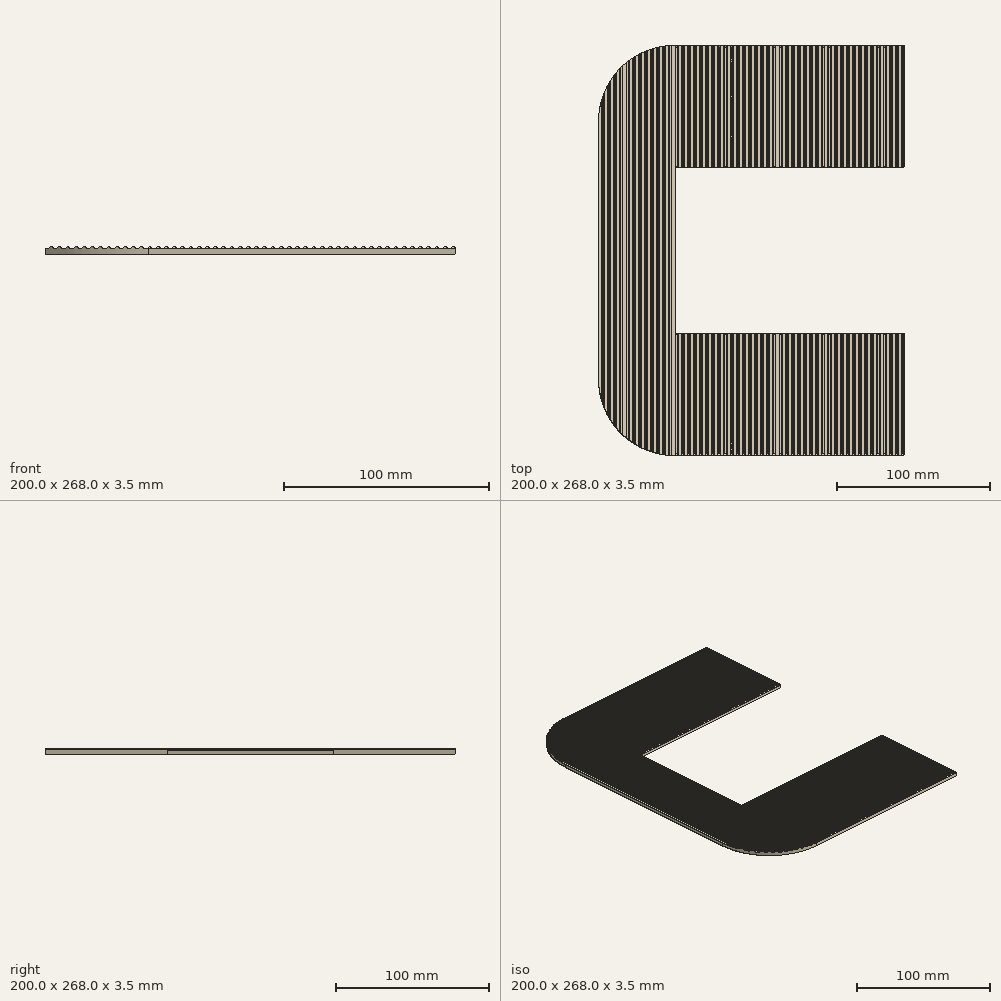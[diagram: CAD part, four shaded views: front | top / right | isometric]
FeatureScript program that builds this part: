
annotation { "Feature Type Name" : "Feature", "Feature Type Description" : "" }
export const myFeature = defineFeature(function(context is Context, id is Id, definition is map)
    precondition{}
    {
        {
            var Q0;
            Q0=qCreatedBy(makeId("Top.planeOp"),FACE);
            var sketch = newSketch(context, id + "F0", { "sketchPlane" : qUnion([Q0])});
            skLineSegment(sketch, "E0.bottom", {"start": v(-200, 134) * mm, "end": v(0, 134) * mm});
            skLineSegment(sketch, "E0.top", {"start": v(-200, -134) * mm, "end": v(0, -134) * mm});
            skLineSegment(sketch, "E0.left", {"start": v(-200, 134) * mm, "end": v(-200, -134) * mm});
            skLineSegment(sketch, "E0.right", {"start": v(0, 134) * mm, "end": v(0, -134) * mm});
            skPoint(sketch, "E1", {"position": v(0, 0) * mm});
            skLineSegment(sketch, "E2.bottom", {"start": v(-150, 54) * mm, "end": v(0, 54) * mm});
            skLineSegment(sketch, "E2.top", {"start": v(-150, -54) * mm, "end": v(0, -54) * mm});
            skLineSegment(sketch, "E2.left", {"start": v(-150, 54) * mm, "end": v(-150, -54) * mm});
            skLineSegment(sketch, "E2.right", {"start": v(0, 54) * mm, "end": v(0, -54) * mm});
            skSolve(sketch);
        }
        {
            var Q0;
            {var subQ1=sQuery(id+"F0.wireOp",EDGE,"E0.bottom");Q0=makeQuery(id+"F0.imprint","IMPRINT",FACE,{"disambiguationData":[TD([[makeQuery(id+"F0.imprint","IMPRINT",EDGE,{"derivedFrom":subQ1}),-1.0]])]});}
            extrude(context, id + "F1", {"entities" : qUnion([Q0]), "depth" : 2.5 * mm});
        }
        {
            var Q0;
            Q0=makeQuery(id+"F1.opExtrude","SWEPT_EDGE",EDGE,{"disambiguationData":[OSD([sQuery(id+"F0.wireOp",EDGE,"E0.top"),sQuery(id+"F0.wireOp",EDGE,"E0.left")])]});
            var Q1;
            Q1=makeQuery(id+"F1.opExtrude","SWEPT_EDGE",EDGE,{"disambiguationData":[OSD([sQuery(id+"F0.wireOp",EDGE,"E0.bottom"),sQuery(id+"F0.wireOp",EDGE,"E0.left")])]});
            fillet(context, id + "F2", {"entities" : qUnion([Q0, Q1]), "radius" : 50 * mm, "tangentPropagation" : true, "allowEdgeOverflow" : false});
        }
        {
            var Q0;
            Q0=makeQuery(id+"F1.opExtrude","CAP_FACE",FACE,{"disambiguationData":[OSD([sQuery(id+"F0.wireOp",EDGE,"E0.bottom"),sQuery(id+"F0.wireOp",EDGE,"E0.top"),sQuery(id+"F0.wireOp",EDGE,"E0.left"),sQuery(id+"F0.wireOp",EDGE,"E0.right"),sQuery(id+"F0.wireOp",EDGE,"E2.bottom"),sQuery(id+"F0.wireOp",EDGE,"E2.top"),sQuery(id+"F0.wireOp",EDGE,"E2.left")])],"isStart":false});
            var sketch = newSketch(context, id + "F3", { "sketchPlane" : qUnion([Q0])});
            skLineSegment(sketch, "E3.bottom", {"start": v(0, 134) * mm, "end": v(-2, 134) * mm});
            skLineSegment(sketch, "E3.top", {"start": v(0, -134) * mm, "end": v(-2, -134) * mm});
            skLineSegment(sketch, "E3.left", {"start": v(0, 134) * mm, "end": v(0, -134) * mm});
            skLineSegment(sketch, "E3.right", {"start": v(-2, 134) * mm, "end": v(-2, -134) * mm});
            skLineSegment(sketch, "E4.1.0.0", {"start": v(-4, 134) * mm, "end": v(-4, -134) * mm});
            skLineSegment(sketch, "E4.1.0.1", {"start": v(-6, 134) * mm, "end": v(-6, -134) * mm});
            skLineSegment(sketch, "E4.1.0.2", {"start": v(-4, 134) * mm, "end": v(-6, 134) * mm});
            skLineSegment(sketch, "E4.1.0.3", {"start": v(-4, -134) * mm, "end": v(-6, -134) * mm});
            skLineSegment(sketch, "E4.2.0.0", {"start": v(-8, 134) * mm, "end": v(-8, -134) * mm});
            skLineSegment(sketch, "E4.2.0.1", {"start": v(-10, 134) * mm, "end": v(-10, -134) * mm});
            skLineSegment(sketch, "E4.2.0.2", {"start": v(-8, 134) * mm, "end": v(-10, 134) * mm});
            skLineSegment(sketch, "E4.2.0.3", {"start": v(-8, -134) * mm, "end": v(-10, -134) * mm});
            skLineSegment(sketch, "E4.3.0.0", {"start": v(-12, 134) * mm, "end": v(-12, -134) * mm});
            skLineSegment(sketch, "E4.3.0.1", {"start": v(-14, 134) * mm, "end": v(-14, -134) * mm});
            skLineSegment(sketch, "E4.3.0.2", {"start": v(-12, 134) * mm, "end": v(-14, 134) * mm});
            skLineSegment(sketch, "E4.3.0.3", {"start": v(-12, -134) * mm, "end": v(-14, -134) * mm});
            skLineSegment(sketch, "E4.4.0.0", {"start": v(-16, 134) * mm, "end": v(-16, -134) * mm});
            skLineSegment(sketch, "E4.4.0.1", {"start": v(-18, 134) * mm, "end": v(-18, -134) * mm});
            skLineSegment(sketch, "E4.4.0.2", {"start": v(-16, 134) * mm, "end": v(-18, 134) * mm});
            skLineSegment(sketch, "E4.4.0.3", {"start": v(-16, -134) * mm, "end": v(-18, -134) * mm});
            skLineSegment(sketch, "E4.5.0.0", {"start": v(-20, 134) * mm, "end": v(-20, -134) * mm});
            skLineSegment(sketch, "E4.5.0.1", {"start": v(-22, 134) * mm, "end": v(-22, -134) * mm});
            skLineSegment(sketch, "E4.5.0.2", {"start": v(-20, 134) * mm, "end": v(-22, 134) * mm});
            skLineSegment(sketch, "E4.5.0.3", {"start": v(-20, -134) * mm, "end": v(-22, -134) * mm});
            skLineSegment(sketch, "E4.6.0.0", {"start": v(-24, 134) * mm, "end": v(-24, -134) * mm});
            skLineSegment(sketch, "E4.6.0.1", {"start": v(-26, 134) * mm, "end": v(-26, -134) * mm});
            skLineSegment(sketch, "E4.6.0.2", {"start": v(-24, 134) * mm, "end": v(-26, 134) * mm});
            skLineSegment(sketch, "E4.6.0.3", {"start": v(-24, -134) * mm, "end": v(-26, -134) * mm});
            skLineSegment(sketch, "E4.7.0.0", {"start": v(-28, 134) * mm, "end": v(-28, -134) * mm});
            skLineSegment(sketch, "E4.7.0.1", {"start": v(-30, 134) * mm, "end": v(-30, -134) * mm});
            skLineSegment(sketch, "E4.7.0.2", {"start": v(-28, 134) * mm, "end": v(-30, 134) * mm});
            skLineSegment(sketch, "E4.7.0.3", {"start": v(-28, -134) * mm, "end": v(-30, -134) * mm});
            skLineSegment(sketch, "E4.8.0.0", {"start": v(-32, 134) * mm, "end": v(-32, -134) * mm});
            skLineSegment(sketch, "E4.8.0.1", {"start": v(-34, 134) * mm, "end": v(-34, -134) * mm});
            skLineSegment(sketch, "E4.8.0.2", {"start": v(-32, 134) * mm, "end": v(-34, 134) * mm});
            skLineSegment(sketch, "E4.8.0.3", {"start": v(-32, -134) * mm, "end": v(-34, -134) * mm});
            skLineSegment(sketch, "E4.9.0.0", {"start": v(-36, 134) * mm, "end": v(-36, -134) * mm});
            skLineSegment(sketch, "E4.9.0.1", {"start": v(-38, 134) * mm, "end": v(-38, -134) * mm});
            skLineSegment(sketch, "E4.9.0.2", {"start": v(-36, 134) * mm, "end": v(-38, 134) * mm});
            skLineSegment(sketch, "E4.9.0.3", {"start": v(-36, -134) * mm, "end": v(-38, -134) * mm});
            skLineSegment(sketch, "E4.10.0.0", {"start": v(-40, 134) * mm, "end": v(-40, -134) * mm});
            skLineSegment(sketch, "E4.10.0.1", {"start": v(-42, 134) * mm, "end": v(-42, -134) * mm});
            skLineSegment(sketch, "E4.10.0.2", {"start": v(-40, 134) * mm, "end": v(-42, 134) * mm});
            skLineSegment(sketch, "E4.10.0.3", {"start": v(-40, -134) * mm, "end": v(-42, -134) * mm});
            skLineSegment(sketch, "E4.11.0.0", {"start": v(-44, 134) * mm, "end": v(-44, -134) * mm});
            skLineSegment(sketch, "E4.11.0.1", {"start": v(-46, 134) * mm, "end": v(-46, -134) * mm});
            skLineSegment(sketch, "E4.11.0.2", {"start": v(-44, 134) * mm, "end": v(-46, 134) * mm});
            skLineSegment(sketch, "E4.11.0.3", {"start": v(-44, -134) * mm, "end": v(-46, -134) * mm});
            skLineSegment(sketch, "E4.12.0.0", {"start": v(-48, 134) * mm, "end": v(-48, -134) * mm});
            skLineSegment(sketch, "E4.12.0.1", {"start": v(-50, 134) * mm, "end": v(-50, -134) * mm});
            skLineSegment(sketch, "E4.12.0.2", {"start": v(-48, 134) * mm, "end": v(-50, 134) * mm});
            skLineSegment(sketch, "E4.12.0.3", {"start": v(-48, -134) * mm, "end": v(-50, -134) * mm});
            skLineSegment(sketch, "E4.13.0.0", {"start": v(-52, 134) * mm, "end": v(-52, -134) * mm});
            skLineSegment(sketch, "E4.13.0.1", {"start": v(-54, 134) * mm, "end": v(-54, -134) * mm});
            skLineSegment(sketch, "E4.13.0.2", {"start": v(-52, 134) * mm, "end": v(-54, 134) * mm});
            skLineSegment(sketch, "E4.13.0.3", {"start": v(-52, -134) * mm, "end": v(-54, -134) * mm});
            skLineSegment(sketch, "E4.14.0.0", {"start": v(-56, 134) * mm, "end": v(-56, -134) * mm});
            skLineSegment(sketch, "E4.14.0.1", {"start": v(-58, 134) * mm, "end": v(-58, -134) * mm});
            skLineSegment(sketch, "E4.14.0.2", {"start": v(-56, 134) * mm, "end": v(-58, 134) * mm});
            skLineSegment(sketch, "E4.14.0.3", {"start": v(-56, -134) * mm, "end": v(-58, -134) * mm});
            skLineSegment(sketch, "E4.15.0.0", {"start": v(-60, 134) * mm, "end": v(-60, -134) * mm});
            skLineSegment(sketch, "E4.15.0.1", {"start": v(-62, 134) * mm, "end": v(-62, -134) * mm});
            skLineSegment(sketch, "E4.15.0.2", {"start": v(-60, 134) * mm, "end": v(-62, 134) * mm});
            skLineSegment(sketch, "E4.15.0.3", {"start": v(-60, -134) * mm, "end": v(-62, -134) * mm});
            skLineSegment(sketch, "E4.16.0.0", {"start": v(-64, 134) * mm, "end": v(-64, -134) * mm});
            skLineSegment(sketch, "E4.16.0.1", {"start": v(-66, 134) * mm, "end": v(-66, -134) * mm});
            skLineSegment(sketch, "E4.16.0.2", {"start": v(-64, 134) * mm, "end": v(-66, 134) * mm});
            skLineSegment(sketch, "E4.16.0.3", {"start": v(-64, -134) * mm, "end": v(-66, -134) * mm});
            skLineSegment(sketch, "E4.17.0.0", {"start": v(-68, 134) * mm, "end": v(-68, -134) * mm});
            skLineSegment(sketch, "E4.17.0.1", {"start": v(-70, 134) * mm, "end": v(-70, -134) * mm});
            skLineSegment(sketch, "E4.17.0.2", {"start": v(-68, 134) * mm, "end": v(-70, 134) * mm});
            skLineSegment(sketch, "E4.17.0.3", {"start": v(-68, -134) * mm, "end": v(-70, -134) * mm});
            skLineSegment(sketch, "E4.18.0.0", {"start": v(-72, 134) * mm, "end": v(-72, -134) * mm});
            skLineSegment(sketch, "E4.18.0.1", {"start": v(-74, 134) * mm, "end": v(-74, -134) * mm});
            skLineSegment(sketch, "E4.18.0.2", {"start": v(-72, 134) * mm, "end": v(-74, 134) * mm});
            skLineSegment(sketch, "E4.18.0.3", {"start": v(-72, -134) * mm, "end": v(-74, -134) * mm});
            skLineSegment(sketch, "E4.19.0.0", {"start": v(-76, 134) * mm, "end": v(-76, -134) * mm});
            skLineSegment(sketch, "E4.19.0.1", {"start": v(-78, 134) * mm, "end": v(-78, -134) * mm});
            skLineSegment(sketch, "E4.19.0.2", {"start": v(-76, 134) * mm, "end": v(-78, 134) * mm});
            skLineSegment(sketch, "E4.19.0.3", {"start": v(-76, -134) * mm, "end": v(-78, -134) * mm});
            skLineSegment(sketch, "E4.20.0.0", {"start": v(-80, 134) * mm, "end": v(-80, -134) * mm});
            skLineSegment(sketch, "E4.20.0.1", {"start": v(-82, 134) * mm, "end": v(-82, -134) * mm});
            skLineSegment(sketch, "E4.20.0.2", {"start": v(-80, 134) * mm, "end": v(-82, 134) * mm});
            skLineSegment(sketch, "E4.20.0.3", {"start": v(-80, -134) * mm, "end": v(-82, -134) * mm});
            skLineSegment(sketch, "E4.21.0.0", {"start": v(-84, 134) * mm, "end": v(-84, -134) * mm});
            skLineSegment(sketch, "E4.21.0.1", {"start": v(-86, 134) * mm, "end": v(-86, -134) * mm});
            skLineSegment(sketch, "E4.21.0.2", {"start": v(-84, 134) * mm, "end": v(-86, 134) * mm});
            skLineSegment(sketch, "E4.21.0.3", {"start": v(-84, -134) * mm, "end": v(-86, -134) * mm});
            skLineSegment(sketch, "E4.22.0.0", {"start": v(-88, 134) * mm, "end": v(-88, -134) * mm});
            skLineSegment(sketch, "E4.22.0.1", {"start": v(-90, 134) * mm, "end": v(-90, -134) * mm});
            skLineSegment(sketch, "E4.22.0.2", {"start": v(-88, 134) * mm, "end": v(-90, 134) * mm});
            skLineSegment(sketch, "E4.22.0.3", {"start": v(-88, -134) * mm, "end": v(-90, -134) * mm});
            skLineSegment(sketch, "E4.23.0.0", {"start": v(-92, 134) * mm, "end": v(-92, -134) * mm});
            skLineSegment(sketch, "E4.23.0.1", {"start": v(-94, 134) * mm, "end": v(-94, -134) * mm});
            skLineSegment(sketch, "E4.23.0.2", {"start": v(-92, 134) * mm, "end": v(-94, 134) * mm});
            skLineSegment(sketch, "E4.23.0.3", {"start": v(-92, -134) * mm, "end": v(-94, -134) * mm});
            skLineSegment(sketch, "E4.24.0.0", {"start": v(-96, 134) * mm, "end": v(-96, -134) * mm});
            skLineSegment(sketch, "E4.24.0.1", {"start": v(-98, 134) * mm, "end": v(-98, -134) * mm});
            skLineSegment(sketch, "E4.24.0.2", {"start": v(-96, 134) * mm, "end": v(-98, 134) * mm});
            skLineSegment(sketch, "E4.24.0.3", {"start": v(-96, -134) * mm, "end": v(-98, -134) * mm});
            skLineSegment(sketch, "E4.25.0.0", {"start": v(-100, 134) * mm, "end": v(-100, -134) * mm});
            skLineSegment(sketch, "E4.25.0.1", {"start": v(-102, 134) * mm, "end": v(-102, -134) * mm});
            skLineSegment(sketch, "E4.25.0.2", {"start": v(-100, 134) * mm, "end": v(-102, 134) * mm});
            skLineSegment(sketch, "E4.25.0.3", {"start": v(-100, -134) * mm, "end": v(-102, -134) * mm});
            skLineSegment(sketch, "E4.26.0.0", {"start": v(-104, 134) * mm, "end": v(-104, -134) * mm});
            skLineSegment(sketch, "E4.26.0.1", {"start": v(-106, 134) * mm, "end": v(-106, -134) * mm});
            skLineSegment(sketch, "E4.26.0.2", {"start": v(-104, 134) * mm, "end": v(-106, 134) * mm});
            skLineSegment(sketch, "E4.26.0.3", {"start": v(-104, -134) * mm, "end": v(-106, -134) * mm});
            skLineSegment(sketch, "E4.27.0.0", {"start": v(-108, 134) * mm, "end": v(-108, -134) * mm});
            skLineSegment(sketch, "E4.27.0.1", {"start": v(-110, 134) * mm, "end": v(-110, -134) * mm});
            skLineSegment(sketch, "E4.27.0.2", {"start": v(-108, 134) * mm, "end": v(-110, 134) * mm});
            skLineSegment(sketch, "E4.27.0.3", {"start": v(-108, -134) * mm, "end": v(-110, -134) * mm});
            skLineSegment(sketch, "E4.28.0.0", {"start": v(-112, 134) * mm, "end": v(-112, -134) * mm});
            skLineSegment(sketch, "E4.28.0.1", {"start": v(-114, 134) * mm, "end": v(-114, -134) * mm});
            skLineSegment(sketch, "E4.28.0.2", {"start": v(-112, 134) * mm, "end": v(-114, 134) * mm});
            skLineSegment(sketch, "E4.28.0.3", {"start": v(-112, -134) * mm, "end": v(-114, -134) * mm});
            skLineSegment(sketch, "E4.29.0.0", {"start": v(-116, 134) * mm, "end": v(-116, -134) * mm});
            skLineSegment(sketch, "E4.29.0.1", {"start": v(-118, 134) * mm, "end": v(-118, -134) * mm});
            skLineSegment(sketch, "E4.29.0.2", {"start": v(-116, 134) * mm, "end": v(-118, 134) * mm});
            skLineSegment(sketch, "E4.29.0.3", {"start": v(-116, -134) * mm, "end": v(-118, -134) * mm});
            skLineSegment(sketch, "E4.30.0.0", {"start": v(-120, 134) * mm, "end": v(-120, -134) * mm});
            skLineSegment(sketch, "E4.30.0.1", {"start": v(-122, 134) * mm, "end": v(-122, -134) * mm});
            skLineSegment(sketch, "E4.30.0.2", {"start": v(-120, 134) * mm, "end": v(-122, 134) * mm});
            skLineSegment(sketch, "E4.30.0.3", {"start": v(-120, -134) * mm, "end": v(-122, -134) * mm});
            skLineSegment(sketch, "E4.31.0.0", {"start": v(-124, 134) * mm, "end": v(-124, -134) * mm});
            skLineSegment(sketch, "E4.31.0.1", {"start": v(-126, 134) * mm, "end": v(-126, -134) * mm});
            skLineSegment(sketch, "E4.31.0.2", {"start": v(-124, 134) * mm, "end": v(-126, 134) * mm});
            skLineSegment(sketch, "E4.31.0.3", {"start": v(-124, -134) * mm, "end": v(-126, -134) * mm});
            skLineSegment(sketch, "E4.32.0.0", {"start": v(-128, 134) * mm, "end": v(-128, -134) * mm});
            skLineSegment(sketch, "E4.32.0.1", {"start": v(-130, 134) * mm, "end": v(-130, -134) * mm});
            skLineSegment(sketch, "E4.32.0.2", {"start": v(-128, 134) * mm, "end": v(-130, 134) * mm});
            skLineSegment(sketch, "E4.32.0.3", {"start": v(-128, -134) * mm, "end": v(-130, -134) * mm});
            skLineSegment(sketch, "E4.33.0.0", {"start": v(-132, 134) * mm, "end": v(-132, -134) * mm});
            skLineSegment(sketch, "E4.33.0.1", {"start": v(-134, 134) * mm, "end": v(-134, -134) * mm});
            skLineSegment(sketch, "E4.33.0.2", {"start": v(-132, 134) * mm, "end": v(-134, 134) * mm});
            skLineSegment(sketch, "E4.33.0.3", {"start": v(-132, -134) * mm, "end": v(-134, -134) * mm});
            skLineSegment(sketch, "E4.34.0.0", {"start": v(-136, 134) * mm, "end": v(-136, -134) * mm});
            skLineSegment(sketch, "E4.34.0.1", {"start": v(-138, 134) * mm, "end": v(-138, -134) * mm});
            skLineSegment(sketch, "E4.34.0.2", {"start": v(-136, 134) * mm, "end": v(-138, 134) * mm});
            skLineSegment(sketch, "E4.34.0.3", {"start": v(-136, -134) * mm, "end": v(-138, -134) * mm});
            skLineSegment(sketch, "E4.35.0.0", {"start": v(-140, 134) * mm, "end": v(-140, -134) * mm});
            skLineSegment(sketch, "E4.35.0.1", {"start": v(-142, 134) * mm, "end": v(-142, -134) * mm});
            skLineSegment(sketch, "E4.35.0.2", {"start": v(-140, 134) * mm, "end": v(-142, 134) * mm});
            skLineSegment(sketch, "E4.35.0.3", {"start": v(-140, -134) * mm, "end": v(-142, -134) * mm});
            skLineSegment(sketch, "E4.36.0.0", {"start": v(-144, 134) * mm, "end": v(-144, -134) * mm});
            skLineSegment(sketch, "E4.36.0.1", {"start": v(-146, 134) * mm, "end": v(-146, -134) * mm});
            skLineSegment(sketch, "E4.36.0.2", {"start": v(-144, 134) * mm, "end": v(-146, 134) * mm});
            skLineSegment(sketch, "E4.36.0.3", {"start": v(-144, -134) * mm, "end": v(-146, -134) * mm});
            skLineSegment(sketch, "E4.37.0.0", {"start": v(-148, 134) * mm, "end": v(-148, -134) * mm});
            skLineSegment(sketch, "E4.37.0.1", {"start": v(-150, 134) * mm, "end": v(-150, -134) * mm});
            skLineSegment(sketch, "E4.37.0.2", {"start": v(-148, 134) * mm, "end": v(-150, 134) * mm});
            skLineSegment(sketch, "E4.37.0.3", {"start": v(-148, -134) * mm, "end": v(-150, -134) * mm});
            skLineSegment(sketch, "E4.38.0.0", {"start": v(-152, 134) * mm, "end": v(-152, -134) * mm});
            skLineSegment(sketch, "E4.38.0.1", {"start": v(-154, 134) * mm, "end": v(-154, -134) * mm});
            skLineSegment(sketch, "E4.38.0.2", {"start": v(-152, 134) * mm, "end": v(-154, 134) * mm});
            skLineSegment(sketch, "E4.38.0.3", {"start": v(-152, -134) * mm, "end": v(-154, -134) * mm});
            skLineSegment(sketch, "E4.39.0.0", {"start": v(-156, 134) * mm, "end": v(-156, -134) * mm});
            skLineSegment(sketch, "E4.39.0.1", {"start": v(-158, 134) * mm, "end": v(-158, -134) * mm});
            skLineSegment(sketch, "E4.39.0.2", {"start": v(-156, 134) * mm, "end": v(-158, 134) * mm});
            skLineSegment(sketch, "E4.39.0.3", {"start": v(-156, -134) * mm, "end": v(-158, -134) * mm});
            skLineSegment(sketch, "E4.40.0.0", {"start": v(-160, 134) * mm, "end": v(-160, -134) * mm});
            skLineSegment(sketch, "E4.40.0.1", {"start": v(-162, 134) * mm, "end": v(-162, -134) * mm});
            skLineSegment(sketch, "E4.40.0.2", {"start": v(-160, 134) * mm, "end": v(-162, 134) * mm});
            skLineSegment(sketch, "E4.40.0.3", {"start": v(-160, -134) * mm, "end": v(-162, -134) * mm});
            skLineSegment(sketch, "E4.41.0.0", {"start": v(-164, 134) * mm, "end": v(-164, -134) * mm});
            skLineSegment(sketch, "E4.41.0.1", {"start": v(-166, 134) * mm, "end": v(-166, -134) * mm});
            skLineSegment(sketch, "E4.41.0.2", {"start": v(-164, 134) * mm, "end": v(-166, 134) * mm});
            skLineSegment(sketch, "E4.41.0.3", {"start": v(-164, -134) * mm, "end": v(-166, -134) * mm});
            skLineSegment(sketch, "E4.42.0.0", {"start": v(-168, 134) * mm, "end": v(-168, -134) * mm});
            skLineSegment(sketch, "E4.42.0.1", {"start": v(-170, 134) * mm, "end": v(-170, -134) * mm});
            skLineSegment(sketch, "E4.42.0.2", {"start": v(-168, 134) * mm, "end": v(-170, 134) * mm});
            skLineSegment(sketch, "E4.42.0.3", {"start": v(-168, -134) * mm, "end": v(-170, -134) * mm});
            skLineSegment(sketch, "E4.43.0.0", {"start": v(-172, 134) * mm, "end": v(-172, -134) * mm});
            skLineSegment(sketch, "E4.43.0.1", {"start": v(-174, 134) * mm, "end": v(-174, -134) * mm});
            skLineSegment(sketch, "E4.43.0.2", {"start": v(-172, 134) * mm, "end": v(-174, 134) * mm});
            skLineSegment(sketch, "E4.43.0.3", {"start": v(-172, -134) * mm, "end": v(-174, -134) * mm});
            skLineSegment(sketch, "E4.44.0.0", {"start": v(-176, 134) * mm, "end": v(-176, -134) * mm});
            skLineSegment(sketch, "E4.44.0.1", {"start": v(-178, 134) * mm, "end": v(-178, -134) * mm});
            skLineSegment(sketch, "E4.44.0.2", {"start": v(-176, 134) * mm, "end": v(-178, 134) * mm});
            skLineSegment(sketch, "E4.44.0.3", {"start": v(-176, -134) * mm, "end": v(-178, -134) * mm});
            skLineSegment(sketch, "E4.45.0.0", {"start": v(-180, 134) * mm, "end": v(-180, -134) * mm});
            skLineSegment(sketch, "E4.45.0.1", {"start": v(-182, 134) * mm, "end": v(-182, -134) * mm});
            skLineSegment(sketch, "E4.45.0.2", {"start": v(-180, 134) * mm, "end": v(-182, 134) * mm});
            skLineSegment(sketch, "E4.45.0.3", {"start": v(-180, -134) * mm, "end": v(-182, -134) * mm});
            skLineSegment(sketch, "E4.46.0.0", {"start": v(-184, 134) * mm, "end": v(-184, -134) * mm});
            skLineSegment(sketch, "E4.46.0.1", {"start": v(-186, 134) * mm, "end": v(-186, -134) * mm});
            skLineSegment(sketch, "E4.46.0.2", {"start": v(-184, 134) * mm, "end": v(-186, 134) * mm});
            skLineSegment(sketch, "E4.46.0.3", {"start": v(-184, -134) * mm, "end": v(-186, -134) * mm});
            skLineSegment(sketch, "E4.47.0.0", {"start": v(-188, 134) * mm, "end": v(-188, -134) * mm});
            skLineSegment(sketch, "E4.47.0.1", {"start": v(-190, 134) * mm, "end": v(-190, -134) * mm});
            skLineSegment(sketch, "E4.47.0.2", {"start": v(-188, 134) * mm, "end": v(-190, 134) * mm});
            skLineSegment(sketch, "E4.47.0.3", {"start": v(-188, -134) * mm, "end": v(-190, -134) * mm});
            skLineSegment(sketch, "E4.48.0.0", {"start": v(-192, 134) * mm, "end": v(-192, -134) * mm});
            skLineSegment(sketch, "E4.48.0.1", {"start": v(-194, 134) * mm, "end": v(-194, -134) * mm});
            skLineSegment(sketch, "E4.48.0.2", {"start": v(-192, 134) * mm, "end": v(-194, 134) * mm});
            skLineSegment(sketch, "E4.48.0.3", {"start": v(-192, -134) * mm, "end": v(-194, -134) * mm});
            skLineSegment(sketch, "E4.49.0.0", {"start": v(-196, 134) * mm, "end": v(-196, -134) * mm});
            skLineSegment(sketch, "E4.49.0.1", {"start": v(-198, 134) * mm, "end": v(-198, -134) * mm});
            skLineSegment(sketch, "E4.49.0.2", {"start": v(-196, 134) * mm, "end": v(-198, 134) * mm});
            skLineSegment(sketch, "E4.49.0.3", {"start": v(-196, -134) * mm, "end": v(-198, -134) * mm});
            skLineSegment(sketch, "E4.direction1", {"start": v(-2, -134) * mm, "end": v(-6, -134) * mm, "construction": true});
            skSolve(sketch);
        }
        {
            var Q0;
            {var subQ0=sQuery(id+"F3.wireOp",EDGE,"E4.49.0.0");var subQ1=sQuery(id+"F0.wireOp",EDGE,"E0.left");var subQ2=sQuery(id+"F0.wireOp",EDGE,"E0.top");var subQ3=sQuery(id+"F0.wireOp",EDGE,"E0.bottom");var subQ4=makeQuery(id+"F1.opExtrude","CAP_FACE",FACE,{"disambiguationData":[OSD([subQ3,subQ2,subQ1,sQuery(id+"F0.wireOp",EDGE,"E0.right"),sQuery(id+"F0.wireOp",EDGE,"E2.bottom"),sQuery(id+"F0.wireOp",EDGE,"E2.top"),sQuery(id+"F0.wireOp",EDGE,"E2.left")])],"isStart":false});var subQ5=makeQuery(id+"F2.opFillet","BLEND_EDGE",EDGE,{"blendedFrom":[makeQuery(id+"F1.opExtrude","SWEPT_EDGE",EDGE,{"disambiguationData":[OSD([subQ3,subQ1])]}),subQ4],"blendedInto":[subQ4]});var subQ6=makeQuery(id+"F3.imprint","INTERSECT",VERTEX,{"derivedFrom":[subQ5,subQ0]});Q0=makeQuery(id+"F3.imprint","IMPRINT",FACE,{"disambiguationData":[TD([[makeQuery(id+"F3.imprint","IMPRINT",EDGE,{"disambiguationData":[TD([[subQ6,-1.0]])],"derivedFrom":subQ0}),-1.0]])]});}
            var Q1;
            {var subQ0=sQuery(id+"F3.wireOp",EDGE,"E4.48.0.0");var subQ1=sQuery(id+"F0.wireOp",EDGE,"E0.left");var subQ2=sQuery(id+"F0.wireOp",EDGE,"E0.top");var subQ3=sQuery(id+"F0.wireOp",EDGE,"E0.bottom");var subQ4=makeQuery(id+"F1.opExtrude","CAP_FACE",FACE,{"disambiguationData":[OSD([subQ3,subQ2,subQ1,sQuery(id+"F0.wireOp",EDGE,"E0.right"),sQuery(id+"F0.wireOp",EDGE,"E2.bottom"),sQuery(id+"F0.wireOp",EDGE,"E2.top"),sQuery(id+"F0.wireOp",EDGE,"E2.left")])],"isStart":false});var subQ5=makeQuery(id+"F2.opFillet","BLEND_EDGE",EDGE,{"blendedFrom":[makeQuery(id+"F1.opExtrude","SWEPT_EDGE",EDGE,{"disambiguationData":[OSD([subQ3,subQ1])]}),subQ4],"blendedInto":[subQ4]});var subQ6=makeQuery(id+"F3.imprint","INTERSECT",VERTEX,{"derivedFrom":[subQ5,subQ0]});Q1=makeQuery(id+"F3.imprint","IMPRINT",FACE,{"disambiguationData":[TD([[makeQuery(id+"F3.imprint","IMPRINT",EDGE,{"disambiguationData":[TD([[subQ6,-1.0]])],"derivedFrom":subQ0}),-1.0]])]});}
            var Q2;
            {var subQ0=sQuery(id+"F3.wireOp",EDGE,"E4.47.0.0");var subQ1=sQuery(id+"F0.wireOp",EDGE,"E0.left");var subQ2=sQuery(id+"F0.wireOp",EDGE,"E0.top");var subQ3=sQuery(id+"F0.wireOp",EDGE,"E0.bottom");var subQ4=makeQuery(id+"F1.opExtrude","CAP_FACE",FACE,{"disambiguationData":[OSD([subQ3,subQ2,subQ1,sQuery(id+"F0.wireOp",EDGE,"E0.right"),sQuery(id+"F0.wireOp",EDGE,"E2.bottom"),sQuery(id+"F0.wireOp",EDGE,"E2.top"),sQuery(id+"F0.wireOp",EDGE,"E2.left")])],"isStart":false});var subQ5=makeQuery(id+"F2.opFillet","BLEND_EDGE",EDGE,{"blendedFrom":[makeQuery(id+"F1.opExtrude","SWEPT_EDGE",EDGE,{"disambiguationData":[OSD([subQ3,subQ1])]}),subQ4],"blendedInto":[subQ4]});var subQ6=makeQuery(id+"F3.imprint","INTERSECT",VERTEX,{"derivedFrom":[subQ5,subQ0]});Q2=makeQuery(id+"F3.imprint","IMPRINT",FACE,{"disambiguationData":[TD([[makeQuery(id+"F3.imprint","IMPRINT",EDGE,{"disambiguationData":[TD([[subQ6,-1.0]])],"derivedFrom":subQ0}),-1.0]])]});}
            var Q3;
            {var subQ0=sQuery(id+"F3.wireOp",EDGE,"E4.46.0.0");var subQ1=sQuery(id+"F0.wireOp",EDGE,"E0.left");var subQ2=sQuery(id+"F0.wireOp",EDGE,"E0.top");var subQ3=sQuery(id+"F0.wireOp",EDGE,"E0.bottom");var subQ4=makeQuery(id+"F1.opExtrude","CAP_FACE",FACE,{"disambiguationData":[OSD([subQ3,subQ2,subQ1,sQuery(id+"F0.wireOp",EDGE,"E0.right"),sQuery(id+"F0.wireOp",EDGE,"E2.bottom"),sQuery(id+"F0.wireOp",EDGE,"E2.top"),sQuery(id+"F0.wireOp",EDGE,"E2.left")])],"isStart":false});var subQ5=makeQuery(id+"F2.opFillet","BLEND_EDGE",EDGE,{"blendedFrom":[makeQuery(id+"F1.opExtrude","SWEPT_EDGE",EDGE,{"disambiguationData":[OSD([subQ3,subQ1])]}),subQ4],"blendedInto":[subQ4]});var subQ6=makeQuery(id+"F3.imprint","INTERSECT",VERTEX,{"derivedFrom":[subQ5,subQ0]});Q3=makeQuery(id+"F3.imprint","IMPRINT",FACE,{"disambiguationData":[TD([[makeQuery(id+"F3.imprint","IMPRINT",EDGE,{"disambiguationData":[TD([[subQ6,-1.0]])],"derivedFrom":subQ0}),-1.0]])]});}
            var Q4;
            {var subQ0=sQuery(id+"F3.wireOp",EDGE,"E4.45.0.0");var subQ1=sQuery(id+"F0.wireOp",EDGE,"E0.left");var subQ2=sQuery(id+"F0.wireOp",EDGE,"E0.top");var subQ3=sQuery(id+"F0.wireOp",EDGE,"E0.bottom");var subQ4=makeQuery(id+"F1.opExtrude","CAP_FACE",FACE,{"disambiguationData":[OSD([subQ3,subQ2,subQ1,sQuery(id+"F0.wireOp",EDGE,"E0.right"),sQuery(id+"F0.wireOp",EDGE,"E2.bottom"),sQuery(id+"F0.wireOp",EDGE,"E2.top"),sQuery(id+"F0.wireOp",EDGE,"E2.left")])],"isStart":false});var subQ5=makeQuery(id+"F2.opFillet","BLEND_EDGE",EDGE,{"blendedFrom":[makeQuery(id+"F1.opExtrude","SWEPT_EDGE",EDGE,{"disambiguationData":[OSD([subQ3,subQ1])]}),subQ4],"blendedInto":[subQ4]});var subQ6=makeQuery(id+"F3.imprint","INTERSECT",VERTEX,{"derivedFrom":[subQ5,subQ0]});Q4=makeQuery(id+"F3.imprint","IMPRINT",FACE,{"disambiguationData":[TD([[makeQuery(id+"F3.imprint","IMPRINT",EDGE,{"disambiguationData":[TD([[subQ6,-1.0]])],"derivedFrom":subQ0}),-1.0]])]});}
            var Q5;
            {var subQ0=sQuery(id+"F3.wireOp",EDGE,"E4.44.0.0");var subQ1=sQuery(id+"F0.wireOp",EDGE,"E0.left");var subQ2=sQuery(id+"F0.wireOp",EDGE,"E0.top");var subQ3=sQuery(id+"F0.wireOp",EDGE,"E0.bottom");var subQ4=makeQuery(id+"F1.opExtrude","CAP_FACE",FACE,{"disambiguationData":[OSD([subQ3,subQ2,subQ1,sQuery(id+"F0.wireOp",EDGE,"E0.right"),sQuery(id+"F0.wireOp",EDGE,"E2.bottom"),sQuery(id+"F0.wireOp",EDGE,"E2.top"),sQuery(id+"F0.wireOp",EDGE,"E2.left")])],"isStart":false});var subQ5=makeQuery(id+"F2.opFillet","BLEND_EDGE",EDGE,{"blendedFrom":[makeQuery(id+"F1.opExtrude","SWEPT_EDGE",EDGE,{"disambiguationData":[OSD([subQ3,subQ1])]}),subQ4],"blendedInto":[subQ4]});var subQ6=makeQuery(id+"F3.imprint","INTERSECT",VERTEX,{"derivedFrom":[subQ5,subQ0]});Q5=makeQuery(id+"F3.imprint","IMPRINT",FACE,{"disambiguationData":[TD([[makeQuery(id+"F3.imprint","IMPRINT",EDGE,{"disambiguationData":[TD([[subQ6,-1.0]])],"derivedFrom":subQ0}),-1.0]])]});}
            var Q6;
            {var subQ0=sQuery(id+"F3.wireOp",EDGE,"E4.43.0.0");var subQ1=sQuery(id+"F0.wireOp",EDGE,"E0.left");var subQ2=sQuery(id+"F0.wireOp",EDGE,"E0.top");var subQ3=sQuery(id+"F0.wireOp",EDGE,"E0.bottom");var subQ4=makeQuery(id+"F1.opExtrude","CAP_FACE",FACE,{"disambiguationData":[OSD([subQ3,subQ2,subQ1,sQuery(id+"F0.wireOp",EDGE,"E0.right"),sQuery(id+"F0.wireOp",EDGE,"E2.bottom"),sQuery(id+"F0.wireOp",EDGE,"E2.top"),sQuery(id+"F0.wireOp",EDGE,"E2.left")])],"isStart":false});var subQ5=makeQuery(id+"F2.opFillet","BLEND_EDGE",EDGE,{"blendedFrom":[makeQuery(id+"F1.opExtrude","SWEPT_EDGE",EDGE,{"disambiguationData":[OSD([subQ3,subQ1])]}),subQ4],"blendedInto":[subQ4]});var subQ6=makeQuery(id+"F3.imprint","INTERSECT",VERTEX,{"derivedFrom":[subQ5,subQ0]});Q6=makeQuery(id+"F3.imprint","IMPRINT",FACE,{"disambiguationData":[TD([[makeQuery(id+"F3.imprint","IMPRINT",EDGE,{"disambiguationData":[TD([[subQ6,-1.0]])],"derivedFrom":subQ0}),-1.0]])]});}
            var Q7;
            {var subQ0=sQuery(id+"F3.wireOp",EDGE,"E4.42.0.0");var subQ1=sQuery(id+"F0.wireOp",EDGE,"E0.left");var subQ2=sQuery(id+"F0.wireOp",EDGE,"E0.top");var subQ3=sQuery(id+"F0.wireOp",EDGE,"E0.bottom");var subQ4=makeQuery(id+"F1.opExtrude","CAP_FACE",FACE,{"disambiguationData":[OSD([subQ3,subQ2,subQ1,sQuery(id+"F0.wireOp",EDGE,"E0.right"),sQuery(id+"F0.wireOp",EDGE,"E2.bottom"),sQuery(id+"F0.wireOp",EDGE,"E2.top"),sQuery(id+"F0.wireOp",EDGE,"E2.left")])],"isStart":false});var subQ5=makeQuery(id+"F2.opFillet","BLEND_EDGE",EDGE,{"blendedFrom":[makeQuery(id+"F1.opExtrude","SWEPT_EDGE",EDGE,{"disambiguationData":[OSD([subQ3,subQ1])]}),subQ4],"blendedInto":[subQ4]});var subQ6=makeQuery(id+"F3.imprint","INTERSECT",VERTEX,{"derivedFrom":[subQ5,subQ0]});Q7=makeQuery(id+"F3.imprint","IMPRINT",FACE,{"disambiguationData":[TD([[makeQuery(id+"F3.imprint","IMPRINT",EDGE,{"disambiguationData":[TD([[subQ6,-1.0]])],"derivedFrom":subQ0}),-1.0]])]});}
            var Q8;
            {var subQ0=sQuery(id+"F3.wireOp",EDGE,"E4.41.0.0");var subQ1=sQuery(id+"F0.wireOp",EDGE,"E0.left");var subQ2=sQuery(id+"F0.wireOp",EDGE,"E0.top");var subQ3=sQuery(id+"F0.wireOp",EDGE,"E0.bottom");var subQ4=makeQuery(id+"F1.opExtrude","CAP_FACE",FACE,{"disambiguationData":[OSD([subQ3,subQ2,subQ1,sQuery(id+"F0.wireOp",EDGE,"E0.right"),sQuery(id+"F0.wireOp",EDGE,"E2.bottom"),sQuery(id+"F0.wireOp",EDGE,"E2.top"),sQuery(id+"F0.wireOp",EDGE,"E2.left")])],"isStart":false});var subQ5=makeQuery(id+"F2.opFillet","BLEND_EDGE",EDGE,{"blendedFrom":[makeQuery(id+"F1.opExtrude","SWEPT_EDGE",EDGE,{"disambiguationData":[OSD([subQ3,subQ1])]}),subQ4],"blendedInto":[subQ4]});var subQ6=makeQuery(id+"F3.imprint","INTERSECT",VERTEX,{"derivedFrom":[subQ5,subQ0]});Q8=makeQuery(id+"F3.imprint","IMPRINT",FACE,{"disambiguationData":[TD([[makeQuery(id+"F3.imprint","IMPRINT",EDGE,{"disambiguationData":[TD([[subQ6,-1.0]])],"derivedFrom":subQ0}),-1.0]])]});}
            var Q9;
            {var subQ0=sQuery(id+"F3.wireOp",EDGE,"E4.40.0.0");var subQ1=sQuery(id+"F0.wireOp",EDGE,"E0.left");var subQ2=sQuery(id+"F0.wireOp",EDGE,"E0.top");var subQ3=sQuery(id+"F0.wireOp",EDGE,"E0.bottom");var subQ4=makeQuery(id+"F1.opExtrude","CAP_FACE",FACE,{"disambiguationData":[OSD([subQ3,subQ2,subQ1,sQuery(id+"F0.wireOp",EDGE,"E0.right"),sQuery(id+"F0.wireOp",EDGE,"E2.bottom"),sQuery(id+"F0.wireOp",EDGE,"E2.top"),sQuery(id+"F0.wireOp",EDGE,"E2.left")])],"isStart":false});var subQ5=makeQuery(id+"F2.opFillet","BLEND_EDGE",EDGE,{"blendedFrom":[makeQuery(id+"F1.opExtrude","SWEPT_EDGE",EDGE,{"disambiguationData":[OSD([subQ3,subQ1])]}),subQ4],"blendedInto":[subQ4]});var subQ6=makeQuery(id+"F3.imprint","INTERSECT",VERTEX,{"derivedFrom":[subQ5,subQ0]});Q9=makeQuery(id+"F3.imprint","IMPRINT",FACE,{"disambiguationData":[TD([[makeQuery(id+"F3.imprint","IMPRINT",EDGE,{"disambiguationData":[TD([[subQ6,-1.0]])],"derivedFrom":subQ0}),-1.0]])]});}
            var Q10;
            {var subQ0=sQuery(id+"F3.wireOp",EDGE,"E4.39.0.0");var subQ1=sQuery(id+"F0.wireOp",EDGE,"E0.left");var subQ2=sQuery(id+"F0.wireOp",EDGE,"E0.top");var subQ3=sQuery(id+"F0.wireOp",EDGE,"E0.bottom");var subQ4=makeQuery(id+"F1.opExtrude","CAP_FACE",FACE,{"disambiguationData":[OSD([subQ3,subQ2,subQ1,sQuery(id+"F0.wireOp",EDGE,"E0.right"),sQuery(id+"F0.wireOp",EDGE,"E2.bottom"),sQuery(id+"F0.wireOp",EDGE,"E2.top"),sQuery(id+"F0.wireOp",EDGE,"E2.left")])],"isStart":false});var subQ5=makeQuery(id+"F2.opFillet","BLEND_EDGE",EDGE,{"blendedFrom":[makeQuery(id+"F1.opExtrude","SWEPT_EDGE",EDGE,{"disambiguationData":[OSD([subQ3,subQ1])]}),subQ4],"blendedInto":[subQ4]});var subQ6=makeQuery(id+"F3.imprint","INTERSECT",VERTEX,{"derivedFrom":[subQ5,subQ0]});Q10=makeQuery(id+"F3.imprint","IMPRINT",FACE,{"disambiguationData":[TD([[makeQuery(id+"F3.imprint","IMPRINT",EDGE,{"disambiguationData":[TD([[subQ6,-1.0]])],"derivedFrom":subQ0}),-1.0]])]});}
            var Q11;
            {var subQ0=sQuery(id+"F3.wireOp",EDGE,"E4.38.0.0");var subQ1=sQuery(id+"F0.wireOp",EDGE,"E0.left");var subQ2=sQuery(id+"F0.wireOp",EDGE,"E0.top");var subQ3=sQuery(id+"F0.wireOp",EDGE,"E0.bottom");var subQ4=makeQuery(id+"F1.opExtrude","CAP_FACE",FACE,{"disambiguationData":[OSD([subQ3,subQ2,subQ1,sQuery(id+"F0.wireOp",EDGE,"E0.right"),sQuery(id+"F0.wireOp",EDGE,"E2.bottom"),sQuery(id+"F0.wireOp",EDGE,"E2.top"),sQuery(id+"F0.wireOp",EDGE,"E2.left")])],"isStart":false});var subQ5=makeQuery(id+"F2.opFillet","BLEND_EDGE",EDGE,{"blendedFrom":[makeQuery(id+"F1.opExtrude","SWEPT_EDGE",EDGE,{"disambiguationData":[OSD([subQ3,subQ1])]}),subQ4],"blendedInto":[subQ4]});var subQ6=makeQuery(id+"F3.imprint","INTERSECT",VERTEX,{"derivedFrom":[subQ5,subQ0]});Q11=makeQuery(id+"F3.imprint","IMPRINT",FACE,{"disambiguationData":[TD([[makeQuery(id+"F3.imprint","IMPRINT",EDGE,{"disambiguationData":[TD([[subQ6,-1.0]])],"derivedFrom":subQ0}),-1.0]])]});}
            var Q12;
            {var subQ0=sQuery(id+"F3.wireOp",EDGE,"E4.37.0.3");Q12=makeQuery(id+"F3.imprint","IMPRINT",FACE,{"disambiguationData":[TD([[makeQuery(id+"F3.imprint","IMPRINT",EDGE,{"derivedFrom":subQ0}),1.0]])]});}
            var Q13;
            {var subQ0=sQuery(id+"F3.wireOp",EDGE,"E4.36.0.3");Q13=makeQuery(id+"F3.imprint","IMPRINT",FACE,{"disambiguationData":[TD([[makeQuery(id+"F3.imprint","IMPRINT",EDGE,{"derivedFrom":subQ0}),1.0]])]});}
            var Q14;
            {var subQ0=sQuery(id+"F3.wireOp",EDGE,"E4.35.0.3");Q14=makeQuery(id+"F3.imprint","IMPRINT",FACE,{"disambiguationData":[TD([[makeQuery(id+"F3.imprint","IMPRINT",EDGE,{"derivedFrom":subQ0}),1.0]])]});}
            var Q15;
            {var subQ0=sQuery(id+"F3.wireOp",EDGE,"E4.34.0.3");Q15=makeQuery(id+"F3.imprint","IMPRINT",FACE,{"disambiguationData":[TD([[makeQuery(id+"F3.imprint","IMPRINT",EDGE,{"derivedFrom":subQ0}),1.0]])]});}
            var Q16;
            {var subQ0=sQuery(id+"F3.wireOp",EDGE,"E4.33.0.3");Q16=makeQuery(id+"F3.imprint","IMPRINT",FACE,{"disambiguationData":[TD([[makeQuery(id+"F3.imprint","IMPRINT",EDGE,{"derivedFrom":subQ0}),1.0]])]});}
            var Q17;
            {var subQ0=sQuery(id+"F3.wireOp",EDGE,"E4.32.0.3");Q17=makeQuery(id+"F3.imprint","IMPRINT",FACE,{"disambiguationData":[TD([[makeQuery(id+"F3.imprint","IMPRINT",EDGE,{"derivedFrom":subQ0}),1.0]])]});}
            var Q18;
            {var subQ0=sQuery(id+"F3.wireOp",EDGE,"E4.31.0.3");Q18=makeQuery(id+"F3.imprint","IMPRINT",FACE,{"disambiguationData":[TD([[makeQuery(id+"F3.imprint","IMPRINT",EDGE,{"derivedFrom":subQ0}),1.0]])]});}
            var Q19;
            {var subQ0=sQuery(id+"F3.wireOp",EDGE,"E4.30.0.3");Q19=makeQuery(id+"F3.imprint","IMPRINT",FACE,{"disambiguationData":[TD([[makeQuery(id+"F3.imprint","IMPRINT",EDGE,{"derivedFrom":subQ0}),1.0]])]});}
            var Q20;
            {var subQ0=sQuery(id+"F3.wireOp",EDGE,"E4.29.0.3");Q20=makeQuery(id+"F3.imprint","IMPRINT",FACE,{"disambiguationData":[TD([[makeQuery(id+"F3.imprint","IMPRINT",EDGE,{"derivedFrom":subQ0}),1.0]])]});}
            var Q21;
            {var subQ0=sQuery(id+"F3.wireOp",EDGE,"E4.28.0.3");Q21=makeQuery(id+"F3.imprint","IMPRINT",FACE,{"disambiguationData":[TD([[makeQuery(id+"F3.imprint","IMPRINT",EDGE,{"derivedFrom":subQ0}),1.0]])]});}
            var Q22;
            {var subQ0=sQuery(id+"F3.wireOp",EDGE,"E4.27.0.3");Q22=makeQuery(id+"F3.imprint","IMPRINT",FACE,{"disambiguationData":[TD([[makeQuery(id+"F3.imprint","IMPRINT",EDGE,{"derivedFrom":subQ0}),1.0]])]});}
            var Q23;
            {var subQ0=sQuery(id+"F3.wireOp",EDGE,"E4.26.0.3");Q23=makeQuery(id+"F3.imprint","IMPRINT",FACE,{"disambiguationData":[TD([[makeQuery(id+"F3.imprint","IMPRINT",EDGE,{"derivedFrom":subQ0}),1.0]])]});}
            var Q24;
            {var subQ0=sQuery(id+"F3.wireOp",EDGE,"E4.25.0.3");Q24=makeQuery(id+"F3.imprint","IMPRINT",FACE,{"disambiguationData":[TD([[makeQuery(id+"F3.imprint","IMPRINT",EDGE,{"derivedFrom":subQ0}),1.0]])]});}
            var Q25;
            {var subQ0=sQuery(id+"F3.wireOp",EDGE,"E4.24.0.3");Q25=makeQuery(id+"F3.imprint","IMPRINT",FACE,{"disambiguationData":[TD([[makeQuery(id+"F3.imprint","IMPRINT",EDGE,{"derivedFrom":subQ0}),1.0]])]});}
            var Q26;
            {var subQ0=sQuery(id+"F3.wireOp",EDGE,"E4.23.0.3");Q26=makeQuery(id+"F3.imprint","IMPRINT",FACE,{"disambiguationData":[TD([[makeQuery(id+"F3.imprint","IMPRINT",EDGE,{"derivedFrom":subQ0}),1.0]])]});}
            var Q27;
            {var subQ0=sQuery(id+"F3.wireOp",EDGE,"E4.22.0.3");Q27=makeQuery(id+"F3.imprint","IMPRINT",FACE,{"disambiguationData":[TD([[makeQuery(id+"F3.imprint","IMPRINT",EDGE,{"derivedFrom":subQ0}),1.0]])]});}
            var Q28;
            {var subQ0=sQuery(id+"F3.wireOp",EDGE,"E4.21.0.3");Q28=makeQuery(id+"F3.imprint","IMPRINT",FACE,{"disambiguationData":[TD([[makeQuery(id+"F3.imprint","IMPRINT",EDGE,{"derivedFrom":subQ0}),1.0]])]});}
            var Q29;
            {var subQ0=sQuery(id+"F3.wireOp",EDGE,"E4.20.0.3");Q29=makeQuery(id+"F3.imprint","IMPRINT",FACE,{"disambiguationData":[TD([[makeQuery(id+"F3.imprint","IMPRINT",EDGE,{"derivedFrom":subQ0}),1.0]])]});}
            var Q30;
            {var subQ0=sQuery(id+"F3.wireOp",EDGE,"E4.19.0.3");Q30=makeQuery(id+"F3.imprint","IMPRINT",FACE,{"disambiguationData":[TD([[makeQuery(id+"F3.imprint","IMPRINT",EDGE,{"derivedFrom":subQ0}),1.0]])]});}
            var Q31;
            {var subQ0=sQuery(id+"F3.wireOp",EDGE,"E4.18.0.3");Q31=makeQuery(id+"F3.imprint","IMPRINT",FACE,{"disambiguationData":[TD([[makeQuery(id+"F3.imprint","IMPRINT",EDGE,{"derivedFrom":subQ0}),1.0]])]});}
            var Q32;
            {var subQ0=sQuery(id+"F3.wireOp",EDGE,"E4.17.0.3");Q32=makeQuery(id+"F3.imprint","IMPRINT",FACE,{"disambiguationData":[TD([[makeQuery(id+"F3.imprint","IMPRINT",EDGE,{"derivedFrom":subQ0}),1.0]])]});}
            var Q33;
            {var subQ0=sQuery(id+"F3.wireOp",EDGE,"E4.16.0.3");Q33=makeQuery(id+"F3.imprint","IMPRINT",FACE,{"disambiguationData":[TD([[makeQuery(id+"F3.imprint","IMPRINT",EDGE,{"derivedFrom":subQ0}),1.0]])]});}
            var Q34;
            {var subQ0=sQuery(id+"F3.wireOp",EDGE,"E4.15.0.3");Q34=makeQuery(id+"F3.imprint","IMPRINT",FACE,{"disambiguationData":[TD([[makeQuery(id+"F3.imprint","IMPRINT",EDGE,{"derivedFrom":subQ0}),1.0]])]});}
            var Q35;
            {var subQ0=sQuery(id+"F3.wireOp",EDGE,"E4.14.0.3");Q35=makeQuery(id+"F3.imprint","IMPRINT",FACE,{"disambiguationData":[TD([[makeQuery(id+"F3.imprint","IMPRINT",EDGE,{"derivedFrom":subQ0}),1.0]])]});}
            var Q36;
            {var subQ0=sQuery(id+"F3.wireOp",EDGE,"E4.13.0.3");Q36=makeQuery(id+"F3.imprint","IMPRINT",FACE,{"disambiguationData":[TD([[makeQuery(id+"F3.imprint","IMPRINT",EDGE,{"derivedFrom":subQ0}),1.0]])]});}
            var Q37;
            {var subQ0=sQuery(id+"F3.wireOp",EDGE,"E4.12.0.3");Q37=makeQuery(id+"F3.imprint","IMPRINT",FACE,{"disambiguationData":[TD([[makeQuery(id+"F3.imprint","IMPRINT",EDGE,{"derivedFrom":subQ0}),1.0]])]});}
            var Q38;
            {var subQ0=sQuery(id+"F3.wireOp",EDGE,"E4.11.0.3");Q38=makeQuery(id+"F3.imprint","IMPRINT",FACE,{"disambiguationData":[TD([[makeQuery(id+"F3.imprint","IMPRINT",EDGE,{"derivedFrom":subQ0}),1.0]])]});}
            var Q39;
            {var subQ0=sQuery(id+"F3.wireOp",EDGE,"E4.10.0.3");Q39=makeQuery(id+"F3.imprint","IMPRINT",FACE,{"disambiguationData":[TD([[makeQuery(id+"F3.imprint","IMPRINT",EDGE,{"derivedFrom":subQ0}),1.0]])]});}
            var Q40;
            {var subQ0=sQuery(id+"F3.wireOp",EDGE,"E4.9.0.3");Q40=makeQuery(id+"F3.imprint","IMPRINT",FACE,{"disambiguationData":[TD([[makeQuery(id+"F3.imprint","IMPRINT",EDGE,{"derivedFrom":subQ0}),1.0]])]});}
            var Q41;
            {var subQ0=sQuery(id+"F3.wireOp",EDGE,"E4.8.0.3");Q41=makeQuery(id+"F3.imprint","IMPRINT",FACE,{"disambiguationData":[TD([[makeQuery(id+"F3.imprint","IMPRINT",EDGE,{"derivedFrom":subQ0}),1.0]])]});}
            var Q42;
            {var subQ0=sQuery(id+"F3.wireOp",EDGE,"E4.7.0.3");Q42=makeQuery(id+"F3.imprint","IMPRINT",FACE,{"disambiguationData":[TD([[makeQuery(id+"F3.imprint","IMPRINT",EDGE,{"derivedFrom":subQ0}),1.0]])]});}
            var Q43;
            {var subQ0=sQuery(id+"F3.wireOp",EDGE,"E4.6.0.3");Q43=makeQuery(id+"F3.imprint","IMPRINT",FACE,{"disambiguationData":[TD([[makeQuery(id+"F3.imprint","IMPRINT",EDGE,{"derivedFrom":subQ0}),1.0]])]});}
            var Q44;
            {var subQ0=sQuery(id+"F3.wireOp",EDGE,"E4.5.0.3");Q44=makeQuery(id+"F3.imprint","IMPRINT",FACE,{"disambiguationData":[TD([[makeQuery(id+"F3.imprint","IMPRINT",EDGE,{"derivedFrom":subQ0}),1.0]])]});}
            var Q45;
            {var subQ0=sQuery(id+"F3.wireOp",EDGE,"E4.4.0.3");Q45=makeQuery(id+"F3.imprint","IMPRINT",FACE,{"disambiguationData":[TD([[makeQuery(id+"F3.imprint","IMPRINT",EDGE,{"derivedFrom":subQ0}),1.0]])]});}
            var Q46;
            {var subQ0=sQuery(id+"F3.wireOp",EDGE,"E4.3.0.3");Q46=makeQuery(id+"F3.imprint","IMPRINT",FACE,{"disambiguationData":[TD([[makeQuery(id+"F3.imprint","IMPRINT",EDGE,{"derivedFrom":subQ0}),1.0]])]});}
            var Q47;
            {var subQ0=sQuery(id+"F3.wireOp",EDGE,"E4.2.0.3");Q47=makeQuery(id+"F3.imprint","IMPRINT",FACE,{"disambiguationData":[TD([[makeQuery(id+"F3.imprint","IMPRINT",EDGE,{"derivedFrom":subQ0}),1.0]])]});}
            var Q48;
            {var subQ0=sQuery(id+"F3.wireOp",EDGE,"E4.1.0.3");Q48=makeQuery(id+"F3.imprint","IMPRINT",FACE,{"disambiguationData":[TD([[makeQuery(id+"F3.imprint","IMPRINT",EDGE,{"derivedFrom":subQ0}),1.0]])]});}
            var Q49;
            {var subQ0=sQuery(id+"F3.wireOp",EDGE,"E3.top");Q49=makeQuery(id+"F3.imprint","IMPRINT",FACE,{"disambiguationData":[TD([[makeQuery(id+"F3.imprint","IMPRINT",EDGE,{"derivedFrom":subQ0}),1.0]])]});}
            var Q50;
            {var subQ0=sQuery(id+"F3.wireOp",EDGE,"E4.37.0.2");Q50=makeQuery(id+"F3.imprint","IMPRINT",FACE,{"disambiguationData":[TD([[makeQuery(id+"F3.imprint","IMPRINT",EDGE,{"derivedFrom":subQ0}),-1.0]])]});}
            var Q51;
            {var subQ0=sQuery(id+"F3.wireOp",EDGE,"E4.36.0.2");Q51=makeQuery(id+"F3.imprint","IMPRINT",FACE,{"disambiguationData":[TD([[makeQuery(id+"F3.imprint","IMPRINT",EDGE,{"derivedFrom":subQ0}),-1.0]])]});}
            var Q52;
            {var subQ0=sQuery(id+"F3.wireOp",EDGE,"E4.35.0.2");Q52=makeQuery(id+"F3.imprint","IMPRINT",FACE,{"disambiguationData":[TD([[makeQuery(id+"F3.imprint","IMPRINT",EDGE,{"derivedFrom":subQ0}),-1.0]])]});}
            var Q53;
            {var subQ0=sQuery(id+"F3.wireOp",EDGE,"E4.34.0.2");Q53=makeQuery(id+"F3.imprint","IMPRINT",FACE,{"disambiguationData":[TD([[makeQuery(id+"F3.imprint","IMPRINT",EDGE,{"derivedFrom":subQ0}),-1.0]])]});}
            var Q54;
            {var subQ0=sQuery(id+"F3.wireOp",EDGE,"E4.33.0.2");Q54=makeQuery(id+"F3.imprint","IMPRINT",FACE,{"disambiguationData":[TD([[makeQuery(id+"F3.imprint","IMPRINT",EDGE,{"derivedFrom":subQ0}),-1.0]])]});}
            var Q55;
            {var subQ0=sQuery(id+"F3.wireOp",EDGE,"E4.32.0.2");Q55=makeQuery(id+"F3.imprint","IMPRINT",FACE,{"disambiguationData":[TD([[makeQuery(id+"F3.imprint","IMPRINT",EDGE,{"derivedFrom":subQ0}),-1.0]])]});}
            var Q56;
            {var subQ0=sQuery(id+"F3.wireOp",EDGE,"E4.31.0.2");Q56=makeQuery(id+"F3.imprint","IMPRINT",FACE,{"disambiguationData":[TD([[makeQuery(id+"F3.imprint","IMPRINT",EDGE,{"derivedFrom":subQ0}),-1.0]])]});}
            var Q57;
            {var subQ0=sQuery(id+"F3.wireOp",EDGE,"E4.33.0.2");Q57=makeQuery(id+"F3.imprint","IMPRINT",FACE,{"disambiguationData":[TD([[makeQuery(id+"F3.imprint","IMPRINT",EDGE,{"derivedFrom":subQ0}),-1.0]])]});}
            var Q58;
            {var subQ0=sQuery(id+"F3.wireOp",EDGE,"E4.30.0.2");Q58=makeQuery(id+"F3.imprint","IMPRINT",FACE,{"disambiguationData":[TD([[makeQuery(id+"F3.imprint","IMPRINT",EDGE,{"derivedFrom":subQ0}),-1.0]])]});}
            var Q59;
            {var subQ0=sQuery(id+"F3.wireOp",EDGE,"E4.29.0.2");Q59=makeQuery(id+"F3.imprint","IMPRINT",FACE,{"disambiguationData":[TD([[makeQuery(id+"F3.imprint","IMPRINT",EDGE,{"derivedFrom":subQ0}),-1.0]])]});}
            var Q60;
            {var subQ0=sQuery(id+"F3.wireOp",EDGE,"E4.28.0.2");Q60=makeQuery(id+"F3.imprint","IMPRINT",FACE,{"disambiguationData":[TD([[makeQuery(id+"F3.imprint","IMPRINT",EDGE,{"derivedFrom":subQ0}),-1.0]])]});}
            var Q61;
            {var subQ0=sQuery(id+"F3.wireOp",EDGE,"E4.27.0.2");Q61=makeQuery(id+"F3.imprint","IMPRINT",FACE,{"disambiguationData":[TD([[makeQuery(id+"F3.imprint","IMPRINT",EDGE,{"derivedFrom":subQ0}),-1.0]])]});}
            var Q62;
            {var subQ0=sQuery(id+"F3.wireOp",EDGE,"E4.26.0.2");Q62=makeQuery(id+"F3.imprint","IMPRINT",FACE,{"disambiguationData":[TD([[makeQuery(id+"F3.imprint","IMPRINT",EDGE,{"derivedFrom":subQ0}),-1.0]])]});}
            var Q63;
            {var subQ0=sQuery(id+"F3.wireOp",EDGE,"E4.25.0.2");Q63=makeQuery(id+"F3.imprint","IMPRINT",FACE,{"disambiguationData":[TD([[makeQuery(id+"F3.imprint","IMPRINT",EDGE,{"derivedFrom":subQ0}),-1.0]])]});}
            var Q64;
            {var subQ0=sQuery(id+"F3.wireOp",EDGE,"E4.24.0.2");Q64=makeQuery(id+"F3.imprint","IMPRINT",FACE,{"disambiguationData":[TD([[makeQuery(id+"F3.imprint","IMPRINT",EDGE,{"derivedFrom":subQ0}),-1.0]])]});}
            var Q65;
            {var subQ0=sQuery(id+"F3.wireOp",EDGE,"E4.23.0.2");Q65=makeQuery(id+"F3.imprint","IMPRINT",FACE,{"disambiguationData":[TD([[makeQuery(id+"F3.imprint","IMPRINT",EDGE,{"derivedFrom":subQ0}),-1.0]])]});}
            var Q66;
            {var subQ0=sQuery(id+"F3.wireOp",EDGE,"E4.22.0.2");Q66=makeQuery(id+"F3.imprint","IMPRINT",FACE,{"disambiguationData":[TD([[makeQuery(id+"F3.imprint","IMPRINT",EDGE,{"derivedFrom":subQ0}),-1.0]])]});}
            var Q67;
            {var subQ0=sQuery(id+"F3.wireOp",EDGE,"E4.21.0.2");Q67=makeQuery(id+"F3.imprint","IMPRINT",FACE,{"disambiguationData":[TD([[makeQuery(id+"F3.imprint","IMPRINT",EDGE,{"derivedFrom":subQ0}),-1.0]])]});}
            var Q68;
            {var subQ0=sQuery(id+"F3.wireOp",EDGE,"E4.20.0.2");Q68=makeQuery(id+"F3.imprint","IMPRINT",FACE,{"disambiguationData":[TD([[makeQuery(id+"F3.imprint","IMPRINT",EDGE,{"derivedFrom":subQ0}),-1.0]])]});}
            var Q69;
            {var subQ0=sQuery(id+"F3.wireOp",EDGE,"E4.19.0.2");Q69=makeQuery(id+"F3.imprint","IMPRINT",FACE,{"disambiguationData":[TD([[makeQuery(id+"F3.imprint","IMPRINT",EDGE,{"derivedFrom":subQ0}),-1.0]])]});}
            var Q70;
            {var subQ0=sQuery(id+"F3.wireOp",EDGE,"E4.18.0.2");Q70=makeQuery(id+"F3.imprint","IMPRINT",FACE,{"disambiguationData":[TD([[makeQuery(id+"F3.imprint","IMPRINT",EDGE,{"derivedFrom":subQ0}),-1.0]])]});}
            var Q71;
            {var subQ0=sQuery(id+"F3.wireOp",EDGE,"E4.17.0.2");Q71=makeQuery(id+"F3.imprint","IMPRINT",FACE,{"disambiguationData":[TD([[makeQuery(id+"F3.imprint","IMPRINT",EDGE,{"derivedFrom":subQ0}),-1.0]])]});}
            var Q72;
            {var subQ0=sQuery(id+"F3.wireOp",EDGE,"E4.16.0.2");Q72=makeQuery(id+"F3.imprint","IMPRINT",FACE,{"disambiguationData":[TD([[makeQuery(id+"F3.imprint","IMPRINT",EDGE,{"derivedFrom":subQ0}),-1.0]])]});}
            var Q73;
            {var subQ0=sQuery(id+"F3.wireOp",EDGE,"E4.15.0.2");Q73=makeQuery(id+"F3.imprint","IMPRINT",FACE,{"disambiguationData":[TD([[makeQuery(id+"F3.imprint","IMPRINT",EDGE,{"derivedFrom":subQ0}),-1.0]])]});}
            var Q74;
            {var subQ0=sQuery(id+"F3.wireOp",EDGE,"E4.14.0.2");Q74=makeQuery(id+"F3.imprint","IMPRINT",FACE,{"disambiguationData":[TD([[makeQuery(id+"F3.imprint","IMPRINT",EDGE,{"derivedFrom":subQ0}),-1.0]])]});}
            var Q75;
            {var subQ0=sQuery(id+"F3.wireOp",EDGE,"E4.13.0.2");Q75=makeQuery(id+"F3.imprint","IMPRINT",FACE,{"disambiguationData":[TD([[makeQuery(id+"F3.imprint","IMPRINT",EDGE,{"derivedFrom":subQ0}),-1.0]])]});}
            var Q76;
            {var subQ0=sQuery(id+"F3.wireOp",EDGE,"E4.12.0.2");Q76=makeQuery(id+"F3.imprint","IMPRINT",FACE,{"disambiguationData":[TD([[makeQuery(id+"F3.imprint","IMPRINT",EDGE,{"derivedFrom":subQ0}),-1.0]])]});}
            var Q77;
            {var subQ0=sQuery(id+"F3.wireOp",EDGE,"E4.11.0.2");Q77=makeQuery(id+"F3.imprint","IMPRINT",FACE,{"disambiguationData":[TD([[makeQuery(id+"F3.imprint","IMPRINT",EDGE,{"derivedFrom":subQ0}),-1.0]])]});}
            var Q78;
            {var subQ0=sQuery(id+"F3.wireOp",EDGE,"E4.10.0.2");Q78=makeQuery(id+"F3.imprint","IMPRINT",FACE,{"disambiguationData":[TD([[makeQuery(id+"F3.imprint","IMPRINT",EDGE,{"derivedFrom":subQ0}),-1.0]])]});}
            var Q79;
            {var subQ0=sQuery(id+"F3.wireOp",EDGE,"E4.9.0.2");Q79=makeQuery(id+"F3.imprint","IMPRINT",FACE,{"disambiguationData":[TD([[makeQuery(id+"F3.imprint","IMPRINT",EDGE,{"derivedFrom":subQ0}),-1.0]])]});}
            var Q80;
            {var subQ0=sQuery(id+"F3.wireOp",EDGE,"E4.8.0.2");Q80=makeQuery(id+"F3.imprint","IMPRINT",FACE,{"disambiguationData":[TD([[makeQuery(id+"F3.imprint","IMPRINT",EDGE,{"derivedFrom":subQ0}),-1.0]])]});}
            var Q81;
            {var subQ0=sQuery(id+"F3.wireOp",EDGE,"E4.7.0.2");Q81=makeQuery(id+"F3.imprint","IMPRINT",FACE,{"disambiguationData":[TD([[makeQuery(id+"F3.imprint","IMPRINT",EDGE,{"derivedFrom":subQ0}),-1.0]])]});}
            var Q82;
            {var subQ0=sQuery(id+"F3.wireOp",EDGE,"E4.6.0.2");Q82=makeQuery(id+"F3.imprint","IMPRINT",FACE,{"disambiguationData":[TD([[makeQuery(id+"F3.imprint","IMPRINT",EDGE,{"derivedFrom":subQ0}),-1.0]])]});}
            var Q83;
            {var subQ0=sQuery(id+"F3.wireOp",EDGE,"E4.5.0.2");Q83=makeQuery(id+"F3.imprint","IMPRINT",FACE,{"disambiguationData":[TD([[makeQuery(id+"F3.imprint","IMPRINT",EDGE,{"derivedFrom":subQ0}),-1.0]])]});}
            var Q84;
            {var subQ0=sQuery(id+"F3.wireOp",EDGE,"E4.4.0.2");Q84=makeQuery(id+"F3.imprint","IMPRINT",FACE,{"disambiguationData":[TD([[makeQuery(id+"F3.imprint","IMPRINT",EDGE,{"derivedFrom":subQ0}),-1.0]])]});}
            var Q85;
            {var subQ0=sQuery(id+"F3.wireOp",EDGE,"E4.3.0.2");Q85=makeQuery(id+"F3.imprint","IMPRINT",FACE,{"disambiguationData":[TD([[makeQuery(id+"F3.imprint","IMPRINT",EDGE,{"derivedFrom":subQ0}),-1.0]])]});}
            var Q86;
            {var subQ0=sQuery(id+"F3.wireOp",EDGE,"E4.2.0.2");Q86=makeQuery(id+"F3.imprint","IMPRINT",FACE,{"disambiguationData":[TD([[makeQuery(id+"F3.imprint","IMPRINT",EDGE,{"derivedFrom":subQ0}),-1.0]])]});}
            var Q87;
            {var subQ0=sQuery(id+"F3.wireOp",EDGE,"E4.1.0.2");Q87=makeQuery(id+"F3.imprint","IMPRINT",FACE,{"disambiguationData":[TD([[makeQuery(id+"F3.imprint","IMPRINT",EDGE,{"derivedFrom":subQ0}),-1.0]])]});}
            var Q88;
            {var subQ0=sQuery(id+"F3.wireOp",EDGE,"E3.bottom");Q88=makeQuery(id+"F3.imprint","IMPRINT",FACE,{"disambiguationData":[TD([[makeQuery(id+"F3.imprint","IMPRINT",EDGE,{"derivedFrom":subQ0}),-1.0]])]});}
            extrude(context, id + "F4", {"entities" : qUnion([Q0, Q1, Q2, Q3, Q4, Q5, Q6, Q7, Q8, Q9, Q10, Q11, Q12, Q13, Q14, Q15, Q16, Q17, Q18, Q19, Q20, Q21, Q22, Q23, Q24, Q25, Q26, Q27, Q28, Q29, Q30, Q31, Q32, Q33, Q34, Q35, Q36, Q37, Q38, Q39, Q40, Q41, Q42, Q43, Q44, Q45, Q46, Q47, Q48, Q49, Q50, Q51, Q52, Q53, Q54, Q55, Q56, Q57, Q58, Q59, Q60, Q61, Q62, Q63, Q64, Q65, Q66, Q67, Q68, Q69, Q70, Q71, Q72, Q73, Q74, Q75, Q76, Q77, Q78, Q79, Q80, Q81, Q82, Q83, Q84, Q85, Q86, Q87, Q88]), "operationType" : NewBodyOperationType.ADD, "depth" : 1 * mm});
        }
        {
            var Q0;
            {var subQ0=sQuery(id+"F0.wireOp",EDGE,"E2.top");var subQ1=makeQuery(id+"F1.opExtrude","CAP_EDGE",EDGE,{"disambiguationData":[OSD([subQ0])],"isStart":false});Q0=makeQuery(id+"F4.opExtrude","CAP_EDGE",EDGE,{"disambiguationData":[OSD([subQ0]),TDD([makeQuery(id+"F3.imprint","IMPRINT",EDGE,{"disambiguationData":[TD([[makeQuery(id+"F3.imprint","INTERSECT",VERTEX,{"derivedFrom":[subQ1,sQuery(id+"F3.wireOp",EDGE,"E4.1.0.0")]}),1.0]])],"derivedFrom":subQ1})])],"isStart":false});}
            var Q1;
            {var subQ0=sQuery(id+"F0.wireOp",EDGE,"E2.bottom");var subQ1=makeQuery(id+"F1.opExtrude","CAP_EDGE",EDGE,{"disambiguationData":[OSD([subQ0])],"isStart":false});Q1=makeQuery(id+"F4.opExtrude","CAP_EDGE",EDGE,{"disambiguationData":[OSD([subQ0]),TDD([makeQuery(id+"F3.imprint","IMPRINT",EDGE,{"disambiguationData":[TD([[makeQuery(id+"F3.imprint","INTERSECT",VERTEX,{"derivedFrom":[subQ1,sQuery(id+"F3.wireOp",EDGE,"E4.20.0.0")]}),1.0]])],"derivedFrom":subQ1})])],"isStart":false});}
            var Q2;
            Q2=makeQuery(id+"F4.opExtrude","CAP_EDGE",EDGE,{"disambiguationData":[OSD([sQuery(id+"F3.wireOp",EDGE,"E4.23.0.3")])],"isStart":false});
            var Q3;
            Q3=makeQuery(id+"F4.opExtrude","CAP_EDGE",EDGE,{"disambiguationData":[OSD([sQuery(id+"F3.wireOp",EDGE,"E4.21.0.2")])],"isStart":false});
            var Q4;
            Q4=makeQuery(id+"F4.opExtrude","CAP_EDGE",EDGE,{"disambiguationData":[OSD([sQuery(id+"F3.wireOp",EDGE,"E4.37.0.3")])],"isStart":false});
            var Q5;
            Q5=makeQuery(id+"F4.opExtrude","CAP_EDGE",EDGE,{"disambiguationData":[OSD([sQuery(id+"F3.wireOp",EDGE,"E4.36.0.3")])],"isStart":false});
            var Q6;
            Q6=makeQuery(id+"F4.opExtrude","CAP_EDGE",EDGE,{"disambiguationData":[OSD([sQuery(id+"F3.wireOp",EDGE,"E4.35.0.3")])],"isStart":false});
            var Q7;
            Q7=makeQuery(id+"F4.opExtrude","CAP_EDGE",EDGE,{"disambiguationData":[OSD([sQuery(id+"F3.wireOp",EDGE,"E4.34.0.3")])],"isStart":false});
            var Q8;
            Q8=makeQuery(id+"F4.opExtrude","CAP_EDGE",EDGE,{"disambiguationData":[OSD([sQuery(id+"F3.wireOp",EDGE,"E4.33.0.3")])],"isStart":false});
            var Q9;
            Q9=makeQuery(id+"F4.opExtrude","CAP_EDGE",EDGE,{"disambiguationData":[OSD([sQuery(id+"F3.wireOp",EDGE,"E4.32.0.3")])],"isStart":false});
            var Q10;
            Q10=makeQuery(id+"F4.opExtrude","CAP_EDGE",EDGE,{"disambiguationData":[OSD([sQuery(id+"F3.wireOp",EDGE,"E4.31.0.3")])],"isStart":false});
            var Q11;
            Q11=makeQuery(id+"F4.opExtrude","CAP_EDGE",EDGE,{"disambiguationData":[OSD([sQuery(id+"F3.wireOp",EDGE,"E4.30.0.3")])],"isStart":false});
            var Q12;
            Q12=makeQuery(id+"F4.opExtrude","CAP_EDGE",EDGE,{"disambiguationData":[OSD([sQuery(id+"F3.wireOp",EDGE,"E4.29.0.3")])],"isStart":false});
            var Q13;
            Q13=makeQuery(id+"F4.opExtrude","CAP_EDGE",EDGE,{"disambiguationData":[OSD([sQuery(id+"F3.wireOp",EDGE,"E4.28.0.3")])],"isStart":false});
            var Q14;
            Q14=makeQuery(id+"F4.opExtrude","CAP_EDGE",EDGE,{"disambiguationData":[OSD([sQuery(id+"F3.wireOp",EDGE,"E4.27.0.3")])],"isStart":false});
            var Q15;
            Q15=makeQuery(id+"F4.opExtrude","CAP_EDGE",EDGE,{"disambiguationData":[OSD([sQuery(id+"F3.wireOp",EDGE,"E4.26.0.3")])],"isStart":false});
            var Q16;
            Q16=makeQuery(id+"F4.opExtrude","CAP_EDGE",EDGE,{"disambiguationData":[OSD([sQuery(id+"F3.wireOp",EDGE,"E4.25.0.3")])],"isStart":false});
            var Q17;
            Q17=makeQuery(id+"F4.opExtrude","CAP_EDGE",EDGE,{"disambiguationData":[OSD([sQuery(id+"F3.wireOp",EDGE,"E4.24.0.3")])],"isStart":false});
            var Q18;
            Q18=makeQuery(id+"F4.opExtrude","CAP_EDGE",EDGE,{"disambiguationData":[OSD([sQuery(id+"F3.wireOp",EDGE,"E4.22.0.3")])],"isStart":false});
            var Q19;
            Q19=makeQuery(id+"F4.opExtrude","CAP_EDGE",EDGE,{"disambiguationData":[OSD([sQuery(id+"F3.wireOp",EDGE,"E4.21.0.3")])],"isStart":false});
            var Q20;
            Q20=makeQuery(id+"F4.opExtrude","CAP_EDGE",EDGE,{"disambiguationData":[OSD([sQuery(id+"F3.wireOp",EDGE,"E4.20.0.3")])],"isStart":false});
            var Q21;
            Q21=makeQuery(id+"F4.opExtrude","CAP_EDGE",EDGE,{"disambiguationData":[OSD([sQuery(id+"F3.wireOp",EDGE,"E4.19.0.3")])],"isStart":false});
            var Q22;
            Q22=makeQuery(id+"F4.opExtrude","CAP_EDGE",EDGE,{"disambiguationData":[OSD([sQuery(id+"F3.wireOp",EDGE,"E4.18.0.3")])],"isStart":false});
            var Q23;
            Q23=makeQuery(id+"F4.opExtrude","CAP_EDGE",EDGE,{"disambiguationData":[OSD([sQuery(id+"F3.wireOp",EDGE,"E4.17.0.3")])],"isStart":false});
            var Q24;
            Q24=makeQuery(id+"F4.opExtrude","CAP_EDGE",EDGE,{"disambiguationData":[OSD([sQuery(id+"F3.wireOp",EDGE,"E4.16.0.3")])],"isStart":false});
            var Q25;
            Q25=makeQuery(id+"F4.opExtrude","CAP_EDGE",EDGE,{"disambiguationData":[OSD([sQuery(id+"F3.wireOp",EDGE,"E4.15.0.3")])],"isStart":false});
            var Q26;
            Q26=makeQuery(id+"F4.opExtrude","CAP_EDGE",EDGE,{"disambiguationData":[OSD([sQuery(id+"F3.wireOp",EDGE,"E4.14.0.3")])],"isStart":false});
            var Q27;
            Q27=makeQuery(id+"F4.opExtrude","CAP_EDGE",EDGE,{"disambiguationData":[OSD([sQuery(id+"F3.wireOp",EDGE,"E4.13.0.3")])],"isStart":false});
            var Q28;
            Q28=makeQuery(id+"F4.opExtrude","CAP_EDGE",EDGE,{"disambiguationData":[OSD([sQuery(id+"F3.wireOp",EDGE,"E4.12.0.3")])],"isStart":false});
            var Q29;
            Q29=makeQuery(id+"F4.opExtrude","CAP_EDGE",EDGE,{"disambiguationData":[OSD([sQuery(id+"F3.wireOp",EDGE,"E4.11.0.3")])],"isStart":false});
            var Q30;
            Q30=makeQuery(id+"F4.opExtrude","CAP_EDGE",EDGE,{"disambiguationData":[OSD([sQuery(id+"F3.wireOp",EDGE,"E4.10.0.3")])],"isStart":false});
            var Q31;
            Q31=makeQuery(id+"F4.opExtrude","CAP_EDGE",EDGE,{"disambiguationData":[OSD([sQuery(id+"F3.wireOp",EDGE,"E4.9.0.3")])],"isStart":false});
            var Q32;
            Q32=makeQuery(id+"F4.opExtrude","CAP_EDGE",EDGE,{"disambiguationData":[OSD([sQuery(id+"F3.wireOp",EDGE,"E4.8.0.3")])],"isStart":false});
            var Q33;
            Q33=makeQuery(id+"F4.opExtrude","CAP_EDGE",EDGE,{"disambiguationData":[OSD([sQuery(id+"F3.wireOp",EDGE,"E4.7.0.3")])],"isStart":false});
            var Q34;
            Q34=makeQuery(id+"F4.opExtrude","CAP_EDGE",EDGE,{"disambiguationData":[OSD([sQuery(id+"F3.wireOp",EDGE,"E4.6.0.3")])],"isStart":false});
            var Q35;
            Q35=makeQuery(id+"F4.opExtrude","CAP_EDGE",EDGE,{"disambiguationData":[OSD([sQuery(id+"F3.wireOp",EDGE,"E4.5.0.3")])],"isStart":false});
            var Q36;
            Q36=makeQuery(id+"F4.opExtrude","CAP_EDGE",EDGE,{"disambiguationData":[OSD([sQuery(id+"F3.wireOp",EDGE,"E4.4.0.3")])],"isStart":false});
            var Q37;
            Q37=makeQuery(id+"F4.opExtrude","CAP_EDGE",EDGE,{"disambiguationData":[OSD([sQuery(id+"F3.wireOp",EDGE,"E4.3.0.3")])],"isStart":false});
            var Q38;
            Q38=makeQuery(id+"F4.opExtrude","CAP_EDGE",EDGE,{"disambiguationData":[OSD([sQuery(id+"F3.wireOp",EDGE,"E4.2.0.3")])],"isStart":false});
            var Q39;
            Q39=makeQuery(id+"F4.opExtrude","CAP_EDGE",EDGE,{"disambiguationData":[OSD([sQuery(id+"F3.wireOp",EDGE,"E4.1.0.3")])],"isStart":false});
            var Q40;
            Q40=makeQuery(id+"F4.opExtrude","CAP_EDGE",EDGE,{"disambiguationData":[OSD([sQuery(id+"F3.wireOp",EDGE,"E3.top")])],"isStart":false});
            var Q41;
            {var subQ0=sQuery(id+"F0.wireOp",EDGE,"E2.bottom");var subQ1=makeQuery(id+"F1.opExtrude","CAP_EDGE",EDGE,{"disambiguationData":[OSD([subQ0])],"isStart":false});Q41=makeQuery(id+"F4.opExtrude","CAP_EDGE",EDGE,{"disambiguationData":[OSD([subQ0]),TDD([makeQuery(id+"F3.imprint","IMPRINT",EDGE,{"disambiguationData":[TD([[makeQuery(id+"F3.imprint","INTERSECT",VERTEX,{"derivedFrom":[subQ1,sQuery(id+"F3.wireOp",EDGE,"E4.37.0.1")]}),-1.0]])],"derivedFrom":subQ1})])],"isStart":false});}
            var Q42;
            {var subQ0=sQuery(id+"F0.wireOp",EDGE,"E2.bottom");var subQ1=makeQuery(id+"F1.opExtrude","CAP_EDGE",EDGE,{"disambiguationData":[OSD([subQ0])],"isStart":false});Q42=makeQuery(id+"F4.opExtrude","CAP_EDGE",EDGE,{"disambiguationData":[OSD([subQ0]),TDD([makeQuery(id+"F3.imprint","IMPRINT",EDGE,{"disambiguationData":[TD([[makeQuery(id+"F3.imprint","INTERSECT",VERTEX,{"derivedFrom":[subQ1,sQuery(id+"F3.wireOp",EDGE,"E4.36.0.0")]}),1.0]])],"derivedFrom":subQ1})])],"isStart":false});}
            var Q43;
            {var subQ0=sQuery(id+"F0.wireOp",EDGE,"E2.bottom");var subQ1=makeQuery(id+"F1.opExtrude","CAP_EDGE",EDGE,{"disambiguationData":[OSD([subQ0])],"isStart":false});Q43=makeQuery(id+"F4.opExtrude","CAP_EDGE",EDGE,{"disambiguationData":[OSD([subQ0]),TDD([makeQuery(id+"F3.imprint","IMPRINT",EDGE,{"disambiguationData":[TD([[makeQuery(id+"F3.imprint","INTERSECT",VERTEX,{"derivedFrom":[subQ1,sQuery(id+"F3.wireOp",EDGE,"E4.35.0.0")]}),1.0]])],"derivedFrom":subQ1})])],"isStart":false});}
            var Q44;
            {var subQ0=sQuery(id+"F0.wireOp",EDGE,"E2.bottom");var subQ1=makeQuery(id+"F1.opExtrude","CAP_EDGE",EDGE,{"disambiguationData":[OSD([subQ0])],"isStart":false});Q44=makeQuery(id+"F4.opExtrude","CAP_EDGE",EDGE,{"disambiguationData":[OSD([subQ0]),TDD([makeQuery(id+"F3.imprint","IMPRINT",EDGE,{"disambiguationData":[TD([[makeQuery(id+"F3.imprint","INTERSECT",VERTEX,{"derivedFrom":[subQ1,sQuery(id+"F3.wireOp",EDGE,"E4.34.0.0")]}),1.0]])],"derivedFrom":subQ1})])],"isStart":false});}
            var Q45;
            {var subQ0=sQuery(id+"F0.wireOp",EDGE,"E2.bottom");var subQ1=makeQuery(id+"F1.opExtrude","CAP_EDGE",EDGE,{"disambiguationData":[OSD([subQ0])],"isStart":false});Q45=makeQuery(id+"F4.opExtrude","CAP_EDGE",EDGE,{"disambiguationData":[OSD([subQ0]),TDD([makeQuery(id+"F3.imprint","IMPRINT",EDGE,{"disambiguationData":[TD([[makeQuery(id+"F3.imprint","INTERSECT",VERTEX,{"derivedFrom":[subQ1,sQuery(id+"F3.wireOp",EDGE,"E4.33.0.0")]}),1.0]])],"derivedFrom":subQ1})])],"isStart":false});}
            var Q46;
            {var subQ0=sQuery(id+"F0.wireOp",EDGE,"E2.bottom");var subQ1=makeQuery(id+"F1.opExtrude","CAP_EDGE",EDGE,{"disambiguationData":[OSD([subQ0])],"isStart":false});Q46=makeQuery(id+"F4.opExtrude","CAP_EDGE",EDGE,{"disambiguationData":[OSD([subQ0]),TDD([makeQuery(id+"F3.imprint","IMPRINT",EDGE,{"disambiguationData":[TD([[makeQuery(id+"F3.imprint","INTERSECT",VERTEX,{"derivedFrom":[subQ1,sQuery(id+"F3.wireOp",EDGE,"E4.32.0.0")]}),1.0]])],"derivedFrom":subQ1})])],"isStart":false});}
            var Q47;
            {var subQ0=sQuery(id+"F0.wireOp",EDGE,"E2.bottom");var subQ1=makeQuery(id+"F1.opExtrude","CAP_EDGE",EDGE,{"disambiguationData":[OSD([subQ0])],"isStart":false});Q47=makeQuery(id+"F4.opExtrude","CAP_EDGE",EDGE,{"disambiguationData":[OSD([subQ0]),TDD([makeQuery(id+"F3.imprint","IMPRINT",EDGE,{"disambiguationData":[TD([[makeQuery(id+"F3.imprint","INTERSECT",VERTEX,{"derivedFrom":[subQ1,sQuery(id+"F3.wireOp",EDGE,"E4.31.0.0")]}),1.0]])],"derivedFrom":subQ1})])],"isStart":false});}
            var Q48;
            {var subQ0=sQuery(id+"F0.wireOp",EDGE,"E2.bottom");var subQ1=makeQuery(id+"F1.opExtrude","CAP_EDGE",EDGE,{"disambiguationData":[OSD([subQ0])],"isStart":false});Q48=makeQuery(id+"F4.opExtrude","CAP_EDGE",EDGE,{"disambiguationData":[OSD([subQ0]),TDD([makeQuery(id+"F3.imprint","IMPRINT",EDGE,{"disambiguationData":[TD([[makeQuery(id+"F3.imprint","INTERSECT",VERTEX,{"derivedFrom":[subQ1,sQuery(id+"F3.wireOp",EDGE,"E4.30.0.0")]}),1.0]])],"derivedFrom":subQ1})])],"isStart":false});}
            var Q49;
            {var subQ0=sQuery(id+"F0.wireOp",EDGE,"E2.bottom");var subQ1=makeQuery(id+"F1.opExtrude","CAP_EDGE",EDGE,{"disambiguationData":[OSD([subQ0])],"isStart":false});Q49=makeQuery(id+"F4.opExtrude","CAP_EDGE",EDGE,{"disambiguationData":[OSD([subQ0]),TDD([makeQuery(id+"F3.imprint","IMPRINT",EDGE,{"disambiguationData":[TD([[makeQuery(id+"F3.imprint","INTERSECT",VERTEX,{"derivedFrom":[subQ1,sQuery(id+"F3.wireOp",EDGE,"E4.29.0.0")]}),1.0]])],"derivedFrom":subQ1})])],"isStart":false});}
            var Q50;
            {var subQ0=sQuery(id+"F0.wireOp",EDGE,"E2.bottom");var subQ1=makeQuery(id+"F1.opExtrude","CAP_EDGE",EDGE,{"disambiguationData":[OSD([subQ0])],"isStart":false});Q50=makeQuery(id+"F4.opExtrude","CAP_EDGE",EDGE,{"disambiguationData":[OSD([subQ0]),TDD([makeQuery(id+"F3.imprint","IMPRINT",EDGE,{"disambiguationData":[TD([[makeQuery(id+"F3.imprint","INTERSECT",VERTEX,{"derivedFrom":[subQ1,sQuery(id+"F3.wireOp",EDGE,"E4.28.0.0")]}),1.0]])],"derivedFrom":subQ1})])],"isStart":false});}
            var Q51;
            {var subQ0=sQuery(id+"F0.wireOp",EDGE,"E2.bottom");var subQ1=makeQuery(id+"F1.opExtrude","CAP_EDGE",EDGE,{"disambiguationData":[OSD([subQ0])],"isStart":false});Q51=makeQuery(id+"F4.opExtrude","CAP_EDGE",EDGE,{"disambiguationData":[OSD([subQ0]),TDD([makeQuery(id+"F3.imprint","IMPRINT",EDGE,{"disambiguationData":[TD([[makeQuery(id+"F3.imprint","INTERSECT",VERTEX,{"derivedFrom":[subQ1,sQuery(id+"F3.wireOp",EDGE,"E4.27.0.0")]}),1.0]])],"derivedFrom":subQ1})])],"isStart":false});}
            var Q52;
            {var subQ0=sQuery(id+"F0.wireOp",EDGE,"E2.bottom");var subQ1=makeQuery(id+"F1.opExtrude","CAP_EDGE",EDGE,{"disambiguationData":[OSD([subQ0])],"isStart":false});Q52=makeQuery(id+"F4.opExtrude","CAP_EDGE",EDGE,{"disambiguationData":[OSD([subQ0]),TDD([makeQuery(id+"F3.imprint","IMPRINT",EDGE,{"disambiguationData":[TD([[makeQuery(id+"F3.imprint","INTERSECT",VERTEX,{"derivedFrom":[subQ1,sQuery(id+"F3.wireOp",EDGE,"E4.26.0.0")]}),1.0]])],"derivedFrom":subQ1})])],"isStart":false});}
            var Q53;
            {var subQ0=sQuery(id+"F0.wireOp",EDGE,"E2.bottom");var subQ1=makeQuery(id+"F1.opExtrude","CAP_EDGE",EDGE,{"disambiguationData":[OSD([subQ0])],"isStart":false});Q53=makeQuery(id+"F4.opExtrude","CAP_EDGE",EDGE,{"disambiguationData":[OSD([subQ0]),TDD([makeQuery(id+"F3.imprint","IMPRINT",EDGE,{"disambiguationData":[TD([[makeQuery(id+"F3.imprint","INTERSECT",VERTEX,{"derivedFrom":[subQ1,sQuery(id+"F3.wireOp",EDGE,"E4.25.0.0")]}),1.0]])],"derivedFrom":subQ1})])],"isStart":false});}
            var Q54;
            {var subQ0=sQuery(id+"F0.wireOp",EDGE,"E2.bottom");var subQ1=makeQuery(id+"F1.opExtrude","CAP_EDGE",EDGE,{"disambiguationData":[OSD([subQ0])],"isStart":false});Q54=makeQuery(id+"F4.opExtrude","CAP_EDGE",EDGE,{"disambiguationData":[OSD([subQ0]),TDD([makeQuery(id+"F3.imprint","IMPRINT",EDGE,{"disambiguationData":[TD([[makeQuery(id+"F3.imprint","INTERSECT",VERTEX,{"derivedFrom":[subQ1,sQuery(id+"F3.wireOp",EDGE,"E4.24.0.0")]}),1.0]])],"derivedFrom":subQ1})])],"isStart":false});}
            var Q55;
            {var subQ0=sQuery(id+"F0.wireOp",EDGE,"E2.bottom");var subQ1=makeQuery(id+"F1.opExtrude","CAP_EDGE",EDGE,{"disambiguationData":[OSD([subQ0])],"isStart":false});Q55=makeQuery(id+"F4.opExtrude","CAP_EDGE",EDGE,{"disambiguationData":[OSD([subQ0]),TDD([makeQuery(id+"F3.imprint","IMPRINT",EDGE,{"disambiguationData":[TD([[makeQuery(id+"F3.imprint","INTERSECT",VERTEX,{"derivedFrom":[subQ1,sQuery(id+"F3.wireOp",EDGE,"E4.23.0.0")]}),1.0]])],"derivedFrom":subQ1})])],"isStart":false});}
            var Q56;
            {var subQ0=sQuery(id+"F0.wireOp",EDGE,"E2.bottom");var subQ1=makeQuery(id+"F1.opExtrude","CAP_EDGE",EDGE,{"disambiguationData":[OSD([subQ0])],"isStart":false});Q56=makeQuery(id+"F4.opExtrude","CAP_EDGE",EDGE,{"disambiguationData":[OSD([subQ0]),TDD([makeQuery(id+"F3.imprint","IMPRINT",EDGE,{"disambiguationData":[TD([[makeQuery(id+"F3.imprint","INTERSECT",VERTEX,{"derivedFrom":[subQ1,sQuery(id+"F3.wireOp",EDGE,"E4.22.0.0")]}),1.0]])],"derivedFrom":subQ1})])],"isStart":false});}
            var Q57;
            {var subQ0=sQuery(id+"F0.wireOp",EDGE,"E2.bottom");var subQ1=makeQuery(id+"F1.opExtrude","CAP_EDGE",EDGE,{"disambiguationData":[OSD([subQ0])],"isStart":false});Q57=makeQuery(id+"F4.opExtrude","CAP_EDGE",EDGE,{"disambiguationData":[OSD([subQ0]),TDD([makeQuery(id+"F3.imprint","IMPRINT",EDGE,{"disambiguationData":[TD([[makeQuery(id+"F3.imprint","INTERSECT",VERTEX,{"derivedFrom":[subQ1,sQuery(id+"F3.wireOp",EDGE,"E4.21.0.0")]}),1.0]])],"derivedFrom":subQ1})])],"isStart":false});}
            var Q58;
            {var subQ0=sQuery(id+"F0.wireOp",EDGE,"E2.bottom");var subQ1=makeQuery(id+"F1.opExtrude","CAP_EDGE",EDGE,{"disambiguationData":[OSD([subQ0])],"isStart":false});Q58=makeQuery(id+"F4.opExtrude","CAP_EDGE",EDGE,{"disambiguationData":[OSD([subQ0]),TDD([makeQuery(id+"F3.imprint","IMPRINT",EDGE,{"disambiguationData":[TD([[makeQuery(id+"F3.imprint","INTERSECT",VERTEX,{"derivedFrom":[subQ1,sQuery(id+"F3.wireOp",EDGE,"E4.19.0.0")]}),1.0]])],"derivedFrom":subQ1})])],"isStart":false});}
            var Q59;
            {var subQ0=sQuery(id+"F0.wireOp",EDGE,"E2.bottom");var subQ1=makeQuery(id+"F1.opExtrude","CAP_EDGE",EDGE,{"disambiguationData":[OSD([subQ0])],"isStart":false});Q59=makeQuery(id+"F4.opExtrude","CAP_EDGE",EDGE,{"disambiguationData":[OSD([subQ0]),TDD([makeQuery(id+"F3.imprint","IMPRINT",EDGE,{"disambiguationData":[TD([[makeQuery(id+"F3.imprint","INTERSECT",VERTEX,{"derivedFrom":[subQ1,sQuery(id+"F3.wireOp",EDGE,"E4.18.0.0")]}),1.0]])],"derivedFrom":subQ1})])],"isStart":false});}
            var Q60;
            {var subQ0=sQuery(id+"F0.wireOp",EDGE,"E2.bottom");var subQ1=makeQuery(id+"F1.opExtrude","CAP_EDGE",EDGE,{"disambiguationData":[OSD([subQ0])],"isStart":false});Q60=makeQuery(id+"F4.opExtrude","CAP_EDGE",EDGE,{"disambiguationData":[OSD([subQ0]),TDD([makeQuery(id+"F3.imprint","IMPRINT",EDGE,{"disambiguationData":[TD([[makeQuery(id+"F3.imprint","INTERSECT",VERTEX,{"derivedFrom":[subQ1,sQuery(id+"F3.wireOp",EDGE,"E4.17.0.0")]}),1.0]])],"derivedFrom":subQ1})])],"isStart":false});}
            var Q61;
            {var subQ0=sQuery(id+"F0.wireOp",EDGE,"E2.bottom");var subQ1=makeQuery(id+"F1.opExtrude","CAP_EDGE",EDGE,{"disambiguationData":[OSD([subQ0])],"isStart":false});Q61=makeQuery(id+"F4.opExtrude","CAP_EDGE",EDGE,{"disambiguationData":[OSD([subQ0]),TDD([makeQuery(id+"F3.imprint","IMPRINT",EDGE,{"disambiguationData":[TD([[makeQuery(id+"F3.imprint","INTERSECT",VERTEX,{"derivedFrom":[subQ1,sQuery(id+"F3.wireOp",EDGE,"E4.16.0.0")]}),1.0]])],"derivedFrom":subQ1})])],"isStart":false});}
            var Q62;
            {var subQ0=sQuery(id+"F0.wireOp",EDGE,"E2.bottom");var subQ1=makeQuery(id+"F1.opExtrude","CAP_EDGE",EDGE,{"disambiguationData":[OSD([subQ0])],"isStart":false});Q62=makeQuery(id+"F4.opExtrude","CAP_EDGE",EDGE,{"disambiguationData":[OSD([subQ0]),TDD([makeQuery(id+"F3.imprint","IMPRINT",EDGE,{"disambiguationData":[TD([[makeQuery(id+"F3.imprint","INTERSECT",VERTEX,{"derivedFrom":[subQ1,sQuery(id+"F3.wireOp",EDGE,"E4.15.0.0")]}),1.0]])],"derivedFrom":subQ1})])],"isStart":false});}
            var Q63;
            {var subQ0=sQuery(id+"F0.wireOp",EDGE,"E2.bottom");var subQ1=makeQuery(id+"F1.opExtrude","CAP_EDGE",EDGE,{"disambiguationData":[OSD([subQ0])],"isStart":false});Q63=makeQuery(id+"F4.opExtrude","CAP_EDGE",EDGE,{"disambiguationData":[OSD([subQ0]),TDD([makeQuery(id+"F3.imprint","IMPRINT",EDGE,{"disambiguationData":[TD([[makeQuery(id+"F3.imprint","INTERSECT",VERTEX,{"derivedFrom":[subQ1,sQuery(id+"F3.wireOp",EDGE,"E4.14.0.0")]}),1.0]])],"derivedFrom":subQ1})])],"isStart":false});}
            var Q64;
            {var subQ0=sQuery(id+"F0.wireOp",EDGE,"E2.bottom");var subQ1=makeQuery(id+"F1.opExtrude","CAP_EDGE",EDGE,{"disambiguationData":[OSD([subQ0])],"isStart":false});Q64=makeQuery(id+"F4.opExtrude","CAP_EDGE",EDGE,{"disambiguationData":[OSD([subQ0]),TDD([makeQuery(id+"F3.imprint","IMPRINT",EDGE,{"disambiguationData":[TD([[makeQuery(id+"F3.imprint","INTERSECT",VERTEX,{"derivedFrom":[subQ1,sQuery(id+"F3.wireOp",EDGE,"E4.13.0.0")]}),1.0]])],"derivedFrom":subQ1})])],"isStart":false});}
            var Q65;
            {var subQ0=sQuery(id+"F0.wireOp",EDGE,"E2.bottom");var subQ1=makeQuery(id+"F1.opExtrude","CAP_EDGE",EDGE,{"disambiguationData":[OSD([subQ0])],"isStart":false});Q65=makeQuery(id+"F4.opExtrude","CAP_EDGE",EDGE,{"disambiguationData":[OSD([subQ0]),TDD([makeQuery(id+"F3.imprint","IMPRINT",EDGE,{"disambiguationData":[TD([[makeQuery(id+"F3.imprint","INTERSECT",VERTEX,{"derivedFrom":[subQ1,sQuery(id+"F3.wireOp",EDGE,"E4.12.0.0")]}),1.0]])],"derivedFrom":subQ1})])],"isStart":false});}
            var Q66;
            {var subQ0=sQuery(id+"F0.wireOp",EDGE,"E2.bottom");var subQ1=makeQuery(id+"F1.opExtrude","CAP_EDGE",EDGE,{"disambiguationData":[OSD([subQ0])],"isStart":false});Q66=makeQuery(id+"F4.opExtrude","CAP_EDGE",EDGE,{"disambiguationData":[OSD([subQ0]),TDD([makeQuery(id+"F3.imprint","IMPRINT",EDGE,{"disambiguationData":[TD([[makeQuery(id+"F3.imprint","INTERSECT",VERTEX,{"derivedFrom":[subQ1,sQuery(id+"F3.wireOp",EDGE,"E4.11.0.0")]}),1.0]])],"derivedFrom":subQ1})])],"isStart":false});}
            var Q67;
            {var subQ0=sQuery(id+"F0.wireOp",EDGE,"E2.bottom");var subQ1=makeQuery(id+"F1.opExtrude","CAP_EDGE",EDGE,{"disambiguationData":[OSD([subQ0])],"isStart":false});Q67=makeQuery(id+"F4.opExtrude","CAP_EDGE",EDGE,{"disambiguationData":[OSD([subQ0]),TDD([makeQuery(id+"F3.imprint","IMPRINT",EDGE,{"disambiguationData":[TD([[makeQuery(id+"F3.imprint","INTERSECT",VERTEX,{"derivedFrom":[subQ1,sQuery(id+"F3.wireOp",EDGE,"E4.10.0.0")]}),1.0]])],"derivedFrom":subQ1})])],"isStart":false});}
            var Q68;
            {var subQ0=sQuery(id+"F0.wireOp",EDGE,"E2.bottom");var subQ1=makeQuery(id+"F1.opExtrude","CAP_EDGE",EDGE,{"disambiguationData":[OSD([subQ0])],"isStart":false});Q68=makeQuery(id+"F4.opExtrude","CAP_EDGE",EDGE,{"disambiguationData":[OSD([subQ0]),TDD([makeQuery(id+"F3.imprint","IMPRINT",EDGE,{"disambiguationData":[TD([[makeQuery(id+"F3.imprint","INTERSECT",VERTEX,{"derivedFrom":[subQ1,sQuery(id+"F3.wireOp",EDGE,"E4.9.0.0")]}),1.0]])],"derivedFrom":subQ1})])],"isStart":false});}
            var Q69;
            {var subQ0=sQuery(id+"F0.wireOp",EDGE,"E2.bottom");var subQ1=makeQuery(id+"F1.opExtrude","CAP_EDGE",EDGE,{"disambiguationData":[OSD([subQ0])],"isStart":false});Q69=makeQuery(id+"F4.opExtrude","CAP_EDGE",EDGE,{"disambiguationData":[OSD([subQ0]),TDD([makeQuery(id+"F3.imprint","IMPRINT",EDGE,{"disambiguationData":[TD([[makeQuery(id+"F3.imprint","INTERSECT",VERTEX,{"derivedFrom":[subQ1,sQuery(id+"F3.wireOp",EDGE,"E4.8.0.0")]}),1.0]])],"derivedFrom":subQ1})])],"isStart":false});}
            var Q70;
            {var subQ0=sQuery(id+"F0.wireOp",EDGE,"E2.bottom");var subQ1=makeQuery(id+"F1.opExtrude","CAP_EDGE",EDGE,{"disambiguationData":[OSD([subQ0])],"isStart":false});Q70=makeQuery(id+"F4.opExtrude","CAP_EDGE",EDGE,{"disambiguationData":[OSD([subQ0]),TDD([makeQuery(id+"F3.imprint","IMPRINT",EDGE,{"disambiguationData":[TD([[makeQuery(id+"F3.imprint","INTERSECT",VERTEX,{"derivedFrom":[subQ1,sQuery(id+"F3.wireOp",EDGE,"E4.7.0.0")]}),1.0]])],"derivedFrom":subQ1})])],"isStart":false});}
            var Q71;
            {var subQ0=sQuery(id+"F0.wireOp",EDGE,"E2.bottom");var subQ1=makeQuery(id+"F1.opExtrude","CAP_EDGE",EDGE,{"disambiguationData":[OSD([subQ0])],"isStart":false});Q71=makeQuery(id+"F4.opExtrude","CAP_EDGE",EDGE,{"disambiguationData":[OSD([subQ0]),TDD([makeQuery(id+"F3.imprint","IMPRINT",EDGE,{"disambiguationData":[TD([[makeQuery(id+"F3.imprint","INTERSECT",VERTEX,{"derivedFrom":[subQ1,sQuery(id+"F3.wireOp",EDGE,"E4.5.0.0")]}),1.0]])],"derivedFrom":subQ1})])],"isStart":false});}
            var Q72;
            {var subQ0=sQuery(id+"F0.wireOp",EDGE,"E2.bottom");var subQ1=makeQuery(id+"F1.opExtrude","CAP_EDGE",EDGE,{"disambiguationData":[OSD([subQ0])],"isStart":false});Q72=makeQuery(id+"F4.opExtrude","CAP_EDGE",EDGE,{"disambiguationData":[OSD([subQ0]),TDD([makeQuery(id+"F3.imprint","IMPRINT",EDGE,{"disambiguationData":[TD([[makeQuery(id+"F3.imprint","INTERSECT",VERTEX,{"derivedFrom":[subQ1,sQuery(id+"F3.wireOp",EDGE,"E4.6.0.0")]}),1.0]])],"derivedFrom":subQ1})])],"isStart":false});}
            var Q73;
            {var subQ0=sQuery(id+"F0.wireOp",EDGE,"E2.bottom");var subQ1=makeQuery(id+"F1.opExtrude","CAP_EDGE",EDGE,{"disambiguationData":[OSD([subQ0])],"isStart":false});Q73=makeQuery(id+"F4.opExtrude","CAP_EDGE",EDGE,{"disambiguationData":[OSD([subQ0]),TDD([makeQuery(id+"F3.imprint","IMPRINT",EDGE,{"disambiguationData":[TD([[makeQuery(id+"F3.imprint","INTERSECT",VERTEX,{"derivedFrom":[subQ1,sQuery(id+"F3.wireOp",EDGE,"E4.4.0.0")]}),1.0]])],"derivedFrom":subQ1})])],"isStart":false});}
            var Q74;
            {var subQ0=sQuery(id+"F0.wireOp",EDGE,"E2.bottom");var subQ1=makeQuery(id+"F1.opExtrude","CAP_EDGE",EDGE,{"disambiguationData":[OSD([subQ0])],"isStart":false});Q74=makeQuery(id+"F4.opExtrude","CAP_EDGE",EDGE,{"disambiguationData":[OSD([subQ0]),TDD([makeQuery(id+"F3.imprint","IMPRINT",EDGE,{"disambiguationData":[TD([[makeQuery(id+"F3.imprint","INTERSECT",VERTEX,{"derivedFrom":[subQ1,sQuery(id+"F3.wireOp",EDGE,"E4.3.0.0")]}),1.0]])],"derivedFrom":subQ1})])],"isStart":false});}
            var Q75;
            {var subQ0=sQuery(id+"F0.wireOp",EDGE,"E2.bottom");var subQ1=makeQuery(id+"F1.opExtrude","CAP_EDGE",EDGE,{"disambiguationData":[OSD([subQ0])],"isStart":false});Q75=makeQuery(id+"F4.opExtrude","CAP_EDGE",EDGE,{"disambiguationData":[OSD([subQ0]),TDD([makeQuery(id+"F3.imprint","IMPRINT",EDGE,{"disambiguationData":[TD([[makeQuery(id+"F3.imprint","INTERSECT",VERTEX,{"derivedFrom":[subQ1,sQuery(id+"F3.wireOp",EDGE,"E4.2.0.0")]}),1.0]])],"derivedFrom":subQ1})])],"isStart":false});}
            var Q76;
            {var subQ0=sQuery(id+"F0.wireOp",EDGE,"E2.bottom");var subQ1=makeQuery(id+"F1.opExtrude","CAP_EDGE",EDGE,{"disambiguationData":[OSD([subQ0])],"isStart":false});Q76=makeQuery(id+"F4.opExtrude","CAP_EDGE",EDGE,{"disambiguationData":[OSD([subQ0]),TDD([makeQuery(id+"F3.imprint","IMPRINT",EDGE,{"disambiguationData":[TD([[makeQuery(id+"F3.imprint","INTERSECT",VERTEX,{"derivedFrom":[subQ1,sQuery(id+"F3.wireOp",EDGE,"E4.1.0.0")]}),1.0]])],"derivedFrom":subQ1})])],"isStart":false});}
            var Q77;
            {var subQ0=sQuery(id+"F0.wireOp",EDGE,"E2.bottom");var subQ1=makeQuery(id+"F1.opExtrude","CAP_EDGE",EDGE,{"disambiguationData":[OSD([subQ0])],"isStart":false});Q77=makeQuery(id+"F4.opExtrude","CAP_EDGE",EDGE,{"disambiguationData":[OSD([subQ0]),TDD([makeQuery(id+"F3.imprint","IMPRINT",EDGE,{"disambiguationData":[TD([[makeQuery(id+"F3.imprint","INTERSECT",VERTEX,{"derivedFrom":[subQ1,sQuery(id+"F3.wireOp",EDGE,"E3.left")]}),1.0]])],"derivedFrom":subQ1})])],"isStart":false});}
            var Q78;
            {var subQ0=sQuery(id+"F0.wireOp",EDGE,"E2.top");var subQ1=makeQuery(id+"F1.opExtrude","CAP_EDGE",EDGE,{"disambiguationData":[OSD([subQ0])],"isStart":false});Q78=makeQuery(id+"F4.opExtrude","CAP_EDGE",EDGE,{"disambiguationData":[OSD([subQ0]),TDD([makeQuery(id+"F3.imprint","IMPRINT",EDGE,{"disambiguationData":[TD([[makeQuery(id+"F3.imprint","INTERSECT",VERTEX,{"derivedFrom":[subQ1,sQuery(id+"F3.wireOp",EDGE,"E3.left")]}),1.0]])],"derivedFrom":subQ1})])],"isStart":false});}
            var Q79;
            {var subQ0=sQuery(id+"F0.wireOp",EDGE,"E2.top");var subQ1=makeQuery(id+"F1.opExtrude","CAP_EDGE",EDGE,{"disambiguationData":[OSD([subQ0])],"isStart":false});Q79=makeQuery(id+"F4.opExtrude","CAP_EDGE",EDGE,{"disambiguationData":[OSD([subQ0]),TDD([makeQuery(id+"F3.imprint","IMPRINT",EDGE,{"disambiguationData":[TD([[makeQuery(id+"F3.imprint","INTERSECT",VERTEX,{"derivedFrom":[subQ1,sQuery(id+"F3.wireOp",EDGE,"E4.2.0.0")]}),1.0]])],"derivedFrom":subQ1})])],"isStart":false});}
            var Q80;
            {var subQ0=sQuery(id+"F0.wireOp",EDGE,"E2.top");var subQ1=makeQuery(id+"F1.opExtrude","CAP_EDGE",EDGE,{"disambiguationData":[OSD([subQ0])],"isStart":false});Q80=makeQuery(id+"F4.opExtrude","CAP_EDGE",EDGE,{"disambiguationData":[OSD([subQ0]),TDD([makeQuery(id+"F3.imprint","IMPRINT",EDGE,{"disambiguationData":[TD([[makeQuery(id+"F3.imprint","INTERSECT",VERTEX,{"derivedFrom":[subQ1,sQuery(id+"F3.wireOp",EDGE,"E4.4.0.0")]}),1.0]])],"derivedFrom":subQ1})])],"isStart":false});}
            var Q81;
            {var subQ0=sQuery(id+"F0.wireOp",EDGE,"E2.top");var subQ1=makeQuery(id+"F1.opExtrude","CAP_EDGE",EDGE,{"disambiguationData":[OSD([subQ0])],"isStart":false});Q81=makeQuery(id+"F4.opExtrude","CAP_EDGE",EDGE,{"disambiguationData":[OSD([subQ0]),TDD([makeQuery(id+"F3.imprint","IMPRINT",EDGE,{"disambiguationData":[TD([[makeQuery(id+"F3.imprint","INTERSECT",VERTEX,{"derivedFrom":[subQ1,sQuery(id+"F3.wireOp",EDGE,"E4.5.0.0")]}),1.0]])],"derivedFrom":subQ1})])],"isStart":false});}
            var Q82;
            {var subQ0=sQuery(id+"F0.wireOp",EDGE,"E2.top");var subQ1=makeQuery(id+"F1.opExtrude","CAP_EDGE",EDGE,{"disambiguationData":[OSD([subQ0])],"isStart":false});Q82=makeQuery(id+"F4.opExtrude","CAP_EDGE",EDGE,{"disambiguationData":[OSD([subQ0]),TDD([makeQuery(id+"F3.imprint","IMPRINT",EDGE,{"disambiguationData":[TD([[makeQuery(id+"F3.imprint","INTERSECT",VERTEX,{"derivedFrom":[subQ1,sQuery(id+"F3.wireOp",EDGE,"E4.6.0.0")]}),1.0]])],"derivedFrom":subQ1})])],"isStart":false});}
            var Q83;
            {var subQ0=sQuery(id+"F0.wireOp",EDGE,"E2.top");var subQ1=makeQuery(id+"F1.opExtrude","CAP_EDGE",EDGE,{"disambiguationData":[OSD([subQ0])],"isStart":false});Q83=makeQuery(id+"F4.opExtrude","CAP_EDGE",EDGE,{"disambiguationData":[OSD([subQ0]),TDD([makeQuery(id+"F3.imprint","IMPRINT",EDGE,{"disambiguationData":[TD([[makeQuery(id+"F3.imprint","INTERSECT",VERTEX,{"derivedFrom":[subQ1,sQuery(id+"F3.wireOp",EDGE,"E4.7.0.0")]}),1.0]])],"derivedFrom":subQ1})])],"isStart":false});}
            var Q84;
            {var subQ0=sQuery(id+"F0.wireOp",EDGE,"E2.top");var subQ1=makeQuery(id+"F1.opExtrude","CAP_EDGE",EDGE,{"disambiguationData":[OSD([subQ0])],"isStart":false});Q84=makeQuery(id+"F4.opExtrude","CAP_EDGE",EDGE,{"disambiguationData":[OSD([subQ0]),TDD([makeQuery(id+"F3.imprint","IMPRINT",EDGE,{"disambiguationData":[TD([[makeQuery(id+"F3.imprint","INTERSECT",VERTEX,{"derivedFrom":[subQ1,sQuery(id+"F3.wireOp",EDGE,"E4.8.0.0")]}),1.0]])],"derivedFrom":subQ1})])],"isStart":false});}
            var Q85;
            {var subQ0=sQuery(id+"F0.wireOp",EDGE,"E2.top");var subQ1=makeQuery(id+"F1.opExtrude","CAP_EDGE",EDGE,{"disambiguationData":[OSD([subQ0])],"isStart":false});Q85=makeQuery(id+"F4.opExtrude","CAP_EDGE",EDGE,{"disambiguationData":[OSD([subQ0]),TDD([makeQuery(id+"F3.imprint","IMPRINT",EDGE,{"disambiguationData":[TD([[makeQuery(id+"F3.imprint","INTERSECT",VERTEX,{"derivedFrom":[subQ1,sQuery(id+"F3.wireOp",EDGE,"E4.9.0.0")]}),1.0]])],"derivedFrom":subQ1})])],"isStart":false});}
            var Q86;
            {var subQ0=sQuery(id+"F0.wireOp",EDGE,"E2.top");var subQ1=makeQuery(id+"F1.opExtrude","CAP_EDGE",EDGE,{"disambiguationData":[OSD([subQ0])],"isStart":false});Q86=makeQuery(id+"F4.opExtrude","CAP_EDGE",EDGE,{"disambiguationData":[OSD([subQ0]),TDD([makeQuery(id+"F3.imprint","IMPRINT",EDGE,{"disambiguationData":[TD([[makeQuery(id+"F3.imprint","INTERSECT",VERTEX,{"derivedFrom":[subQ1,sQuery(id+"F3.wireOp",EDGE,"E4.10.0.0")]}),1.0]])],"derivedFrom":subQ1})])],"isStart":false});}
            var Q87;
            {var subQ0=sQuery(id+"F0.wireOp",EDGE,"E2.top");var subQ1=makeQuery(id+"F1.opExtrude","CAP_EDGE",EDGE,{"disambiguationData":[OSD([subQ0])],"isStart":false});Q87=makeQuery(id+"F4.opExtrude","CAP_EDGE",EDGE,{"disambiguationData":[OSD([subQ0]),TDD([makeQuery(id+"F3.imprint","IMPRINT",EDGE,{"disambiguationData":[TD([[makeQuery(id+"F3.imprint","INTERSECT",VERTEX,{"derivedFrom":[subQ1,sQuery(id+"F3.wireOp",EDGE,"E4.11.0.0")]}),1.0]])],"derivedFrom":subQ1})])],"isStart":false});}
            var Q88;
            {var subQ0=sQuery(id+"F0.wireOp",EDGE,"E2.top");var subQ1=makeQuery(id+"F1.opExtrude","CAP_EDGE",EDGE,{"disambiguationData":[OSD([subQ0])],"isStart":false});Q88=makeQuery(id+"F4.opExtrude","CAP_EDGE",EDGE,{"disambiguationData":[OSD([subQ0]),TDD([makeQuery(id+"F3.imprint","IMPRINT",EDGE,{"disambiguationData":[TD([[makeQuery(id+"F3.imprint","INTERSECT",VERTEX,{"derivedFrom":[subQ1,sQuery(id+"F3.wireOp",EDGE,"E4.12.0.0")]}),1.0]])],"derivedFrom":subQ1})])],"isStart":false});}
            var Q89;
            {var subQ0=sQuery(id+"F0.wireOp",EDGE,"E2.top");var subQ1=makeQuery(id+"F1.opExtrude","CAP_EDGE",EDGE,{"disambiguationData":[OSD([subQ0])],"isStart":false});Q89=makeQuery(id+"F4.opExtrude","CAP_EDGE",EDGE,{"disambiguationData":[OSD([subQ0]),TDD([makeQuery(id+"F3.imprint","IMPRINT",EDGE,{"disambiguationData":[TD([[makeQuery(id+"F3.imprint","INTERSECT",VERTEX,{"derivedFrom":[subQ1,sQuery(id+"F3.wireOp",EDGE,"E4.13.0.0")]}),1.0]])],"derivedFrom":subQ1})])],"isStart":false});}
            var Q90;
            {var subQ0=sQuery(id+"F0.wireOp",EDGE,"E2.top");var subQ1=makeQuery(id+"F1.opExtrude","CAP_EDGE",EDGE,{"disambiguationData":[OSD([subQ0])],"isStart":false});Q90=makeQuery(id+"F4.opExtrude","CAP_EDGE",EDGE,{"disambiguationData":[OSD([subQ0]),TDD([makeQuery(id+"F3.imprint","IMPRINT",EDGE,{"disambiguationData":[TD([[makeQuery(id+"F3.imprint","INTERSECT",VERTEX,{"derivedFrom":[subQ1,sQuery(id+"F3.wireOp",EDGE,"E4.14.0.0")]}),1.0]])],"derivedFrom":subQ1})])],"isStart":false});}
            var Q91;
            {var subQ0=sQuery(id+"F0.wireOp",EDGE,"E2.top");var subQ1=makeQuery(id+"F1.opExtrude","CAP_EDGE",EDGE,{"disambiguationData":[OSD([subQ0])],"isStart":false});Q91=makeQuery(id+"F4.opExtrude","CAP_EDGE",EDGE,{"disambiguationData":[OSD([subQ0]),TDD([makeQuery(id+"F3.imprint","IMPRINT",EDGE,{"disambiguationData":[TD([[makeQuery(id+"F3.imprint","INTERSECT",VERTEX,{"derivedFrom":[subQ1,sQuery(id+"F3.wireOp",EDGE,"E4.15.0.0")]}),1.0]])],"derivedFrom":subQ1})])],"isStart":false});}
            var Q92;
            {var subQ0=sQuery(id+"F0.wireOp",EDGE,"E2.top");var subQ1=makeQuery(id+"F1.opExtrude","CAP_EDGE",EDGE,{"disambiguationData":[OSD([subQ0])],"isStart":false});Q92=makeQuery(id+"F4.opExtrude","CAP_EDGE",EDGE,{"disambiguationData":[OSD([subQ0]),TDD([makeQuery(id+"F3.imprint","IMPRINT",EDGE,{"disambiguationData":[TD([[makeQuery(id+"F3.imprint","INTERSECT",VERTEX,{"derivedFrom":[subQ1,sQuery(id+"F3.wireOp",EDGE,"E4.16.0.0")]}),1.0]])],"derivedFrom":subQ1})])],"isStart":false});}
            var Q93;
            {var subQ0=sQuery(id+"F0.wireOp",EDGE,"E2.top");var subQ1=makeQuery(id+"F1.opExtrude","CAP_EDGE",EDGE,{"disambiguationData":[OSD([subQ0])],"isStart":false});Q93=makeQuery(id+"F4.opExtrude","CAP_EDGE",EDGE,{"disambiguationData":[OSD([subQ0]),TDD([makeQuery(id+"F3.imprint","IMPRINT",EDGE,{"disambiguationData":[TD([[makeQuery(id+"F3.imprint","INTERSECT",VERTEX,{"derivedFrom":[subQ1,sQuery(id+"F3.wireOp",EDGE,"E4.17.0.0")]}),1.0]])],"derivedFrom":subQ1})])],"isStart":false});}
            var Q94;
            {var subQ0=sQuery(id+"F0.wireOp",EDGE,"E2.top");var subQ1=makeQuery(id+"F1.opExtrude","CAP_EDGE",EDGE,{"disambiguationData":[OSD([subQ0])],"isStart":false});Q94=makeQuery(id+"F4.opExtrude","CAP_EDGE",EDGE,{"disambiguationData":[OSD([subQ0]),TDD([makeQuery(id+"F3.imprint","IMPRINT",EDGE,{"disambiguationData":[TD([[makeQuery(id+"F3.imprint","INTERSECT",VERTEX,{"derivedFrom":[subQ1,sQuery(id+"F3.wireOp",EDGE,"E4.18.0.0")]}),1.0]])],"derivedFrom":subQ1})])],"isStart":false});}
            var Q95;
            {var subQ0=sQuery(id+"F0.wireOp",EDGE,"E2.top");var subQ1=makeQuery(id+"F1.opExtrude","CAP_EDGE",EDGE,{"disambiguationData":[OSD([subQ0])],"isStart":false});Q95=makeQuery(id+"F4.opExtrude","CAP_EDGE",EDGE,{"disambiguationData":[OSD([subQ0]),TDD([makeQuery(id+"F3.imprint","IMPRINT",EDGE,{"disambiguationData":[TD([[makeQuery(id+"F3.imprint","INTERSECT",VERTEX,{"derivedFrom":[subQ1,sQuery(id+"F3.wireOp",EDGE,"E4.19.0.0")]}),1.0]])],"derivedFrom":subQ1})])],"isStart":false});}
            var Q96;
            {var subQ0=sQuery(id+"F0.wireOp",EDGE,"E2.top");var subQ1=makeQuery(id+"F1.opExtrude","CAP_EDGE",EDGE,{"disambiguationData":[OSD([subQ0])],"isStart":false});Q96=makeQuery(id+"F4.opExtrude","CAP_EDGE",EDGE,{"disambiguationData":[OSD([subQ0]),TDD([makeQuery(id+"F3.imprint","IMPRINT",EDGE,{"disambiguationData":[TD([[makeQuery(id+"F3.imprint","INTERSECT",VERTEX,{"derivedFrom":[subQ1,sQuery(id+"F3.wireOp",EDGE,"E4.20.0.0")]}),1.0]])],"derivedFrom":subQ1})])],"isStart":false});}
            var Q97;
            {var subQ0=sQuery(id+"F0.wireOp",EDGE,"E2.top");var subQ1=makeQuery(id+"F1.opExtrude","CAP_EDGE",EDGE,{"disambiguationData":[OSD([subQ0])],"isStart":false});Q97=makeQuery(id+"F4.opExtrude","CAP_EDGE",EDGE,{"disambiguationData":[OSD([subQ0]),TDD([makeQuery(id+"F3.imprint","IMPRINT",EDGE,{"disambiguationData":[TD([[makeQuery(id+"F3.imprint","INTERSECT",VERTEX,{"derivedFrom":[subQ1,sQuery(id+"F3.wireOp",EDGE,"E4.21.0.0")]}),1.0]])],"derivedFrom":subQ1})])],"isStart":false});}
            var Q98;
            {var subQ0=sQuery(id+"F0.wireOp",EDGE,"E2.top");var subQ1=makeQuery(id+"F1.opExtrude","CAP_EDGE",EDGE,{"disambiguationData":[OSD([subQ0])],"isStart":false});Q98=makeQuery(id+"F4.opExtrude","CAP_EDGE",EDGE,{"disambiguationData":[OSD([subQ0]),TDD([makeQuery(id+"F3.imprint","IMPRINT",EDGE,{"disambiguationData":[TD([[makeQuery(id+"F3.imprint","INTERSECT",VERTEX,{"derivedFrom":[subQ1,sQuery(id+"F3.wireOp",EDGE,"E4.22.0.0")]}),1.0]])],"derivedFrom":subQ1})])],"isStart":false});}
            var Q99;
            {var subQ0=sQuery(id+"F0.wireOp",EDGE,"E2.top");var subQ1=makeQuery(id+"F1.opExtrude","CAP_EDGE",EDGE,{"disambiguationData":[OSD([subQ0])],"isStart":false});Q99=makeQuery(id+"F4.opExtrude","CAP_EDGE",EDGE,{"disambiguationData":[OSD([subQ0]),TDD([makeQuery(id+"F3.imprint","IMPRINT",EDGE,{"disambiguationData":[TD([[makeQuery(id+"F3.imprint","INTERSECT",VERTEX,{"derivedFrom":[subQ1,sQuery(id+"F3.wireOp",EDGE,"E4.23.0.0")]}),1.0]])],"derivedFrom":subQ1})])],"isStart":false});}
            var Q100;
            {var subQ0=sQuery(id+"F0.wireOp",EDGE,"E2.top");var subQ1=makeQuery(id+"F1.opExtrude","CAP_EDGE",EDGE,{"disambiguationData":[OSD([subQ0])],"isStart":false});Q100=makeQuery(id+"F4.opExtrude","CAP_EDGE",EDGE,{"disambiguationData":[OSD([subQ0]),TDD([makeQuery(id+"F3.imprint","IMPRINT",EDGE,{"disambiguationData":[TD([[makeQuery(id+"F3.imprint","INTERSECT",VERTEX,{"derivedFrom":[subQ1,sQuery(id+"F3.wireOp",EDGE,"E4.24.0.0")]}),1.0]])],"derivedFrom":subQ1})])],"isStart":false});}
            var Q101;
            {var subQ0=sQuery(id+"F0.wireOp",EDGE,"E2.top");var subQ1=makeQuery(id+"F1.opExtrude","CAP_EDGE",EDGE,{"disambiguationData":[OSD([subQ0])],"isStart":false});Q101=makeQuery(id+"F4.opExtrude","CAP_EDGE",EDGE,{"disambiguationData":[OSD([subQ0]),TDD([makeQuery(id+"F3.imprint","IMPRINT",EDGE,{"disambiguationData":[TD([[makeQuery(id+"F3.imprint","INTERSECT",VERTEX,{"derivedFrom":[subQ1,sQuery(id+"F3.wireOp",EDGE,"E4.25.0.0")]}),1.0]])],"derivedFrom":subQ1})])],"isStart":false});}
            var Q102;
            {var subQ0=sQuery(id+"F0.wireOp",EDGE,"E2.top");var subQ1=makeQuery(id+"F1.opExtrude","CAP_EDGE",EDGE,{"disambiguationData":[OSD([subQ0])],"isStart":false});Q102=makeQuery(id+"F4.opExtrude","CAP_EDGE",EDGE,{"disambiguationData":[OSD([subQ0]),TDD([makeQuery(id+"F3.imprint","IMPRINT",EDGE,{"disambiguationData":[TD([[makeQuery(id+"F3.imprint","INTERSECT",VERTEX,{"derivedFrom":[subQ1,sQuery(id+"F3.wireOp",EDGE,"E4.26.0.0")]}),1.0]])],"derivedFrom":subQ1})])],"isStart":false});}
            var Q103;
            {var subQ0=sQuery(id+"F0.wireOp",EDGE,"E2.top");var subQ1=makeQuery(id+"F1.opExtrude","CAP_EDGE",EDGE,{"disambiguationData":[OSD([subQ0])],"isStart":false});Q103=makeQuery(id+"F4.opExtrude","CAP_EDGE",EDGE,{"disambiguationData":[OSD([subQ0]),TDD([makeQuery(id+"F3.imprint","IMPRINT",EDGE,{"disambiguationData":[TD([[makeQuery(id+"F3.imprint","INTERSECT",VERTEX,{"derivedFrom":[subQ1,sQuery(id+"F3.wireOp",EDGE,"E4.27.0.0")]}),1.0]])],"derivedFrom":subQ1})])],"isStart":false});}
            var Q104;
            {var subQ0=sQuery(id+"F0.wireOp",EDGE,"E2.top");var subQ1=makeQuery(id+"F1.opExtrude","CAP_EDGE",EDGE,{"disambiguationData":[OSD([subQ0])],"isStart":false});Q104=makeQuery(id+"F4.opExtrude","CAP_EDGE",EDGE,{"disambiguationData":[OSD([subQ0]),TDD([makeQuery(id+"F3.imprint","IMPRINT",EDGE,{"disambiguationData":[TD([[makeQuery(id+"F3.imprint","INTERSECT",VERTEX,{"derivedFrom":[subQ1,sQuery(id+"F3.wireOp",EDGE,"E4.28.0.0")]}),1.0]])],"derivedFrom":subQ1})])],"isStart":false});}
            var Q105;
            {var subQ0=sQuery(id+"F0.wireOp",EDGE,"E2.top");var subQ1=makeQuery(id+"F1.opExtrude","CAP_EDGE",EDGE,{"disambiguationData":[OSD([subQ0])],"isStart":false});Q105=makeQuery(id+"F4.opExtrude","CAP_EDGE",EDGE,{"disambiguationData":[OSD([subQ0]),TDD([makeQuery(id+"F3.imprint","IMPRINT",EDGE,{"disambiguationData":[TD([[makeQuery(id+"F3.imprint","INTERSECT",VERTEX,{"derivedFrom":[subQ1,sQuery(id+"F3.wireOp",EDGE,"E4.29.0.0")]}),1.0]])],"derivedFrom":subQ1})])],"isStart":false});}
            var Q106;
            {var subQ0=sQuery(id+"F0.wireOp",EDGE,"E2.top");var subQ1=makeQuery(id+"F1.opExtrude","CAP_EDGE",EDGE,{"disambiguationData":[OSD([subQ0])],"isStart":false});Q106=makeQuery(id+"F4.opExtrude","CAP_EDGE",EDGE,{"disambiguationData":[OSD([subQ0]),TDD([makeQuery(id+"F3.imprint","IMPRINT",EDGE,{"disambiguationData":[TD([[makeQuery(id+"F3.imprint","INTERSECT",VERTEX,{"derivedFrom":[subQ1,sQuery(id+"F3.wireOp",EDGE,"E4.30.0.0")]}),1.0]])],"derivedFrom":subQ1})])],"isStart":false});}
            var Q107;
            {var subQ0=sQuery(id+"F0.wireOp",EDGE,"E2.top");var subQ1=makeQuery(id+"F1.opExtrude","CAP_EDGE",EDGE,{"disambiguationData":[OSD([subQ0])],"isStart":false});Q107=makeQuery(id+"F4.opExtrude","CAP_EDGE",EDGE,{"disambiguationData":[OSD([subQ0]),TDD([makeQuery(id+"F3.imprint","IMPRINT",EDGE,{"disambiguationData":[TD([[makeQuery(id+"F3.imprint","INTERSECT",VERTEX,{"derivedFrom":[subQ1,sQuery(id+"F3.wireOp",EDGE,"E4.31.0.0")]}),1.0]])],"derivedFrom":subQ1})])],"isStart":false});}
            var Q108;
            {var subQ0=sQuery(id+"F0.wireOp",EDGE,"E2.top");var subQ1=makeQuery(id+"F1.opExtrude","CAP_EDGE",EDGE,{"disambiguationData":[OSD([subQ0])],"isStart":false});Q108=makeQuery(id+"F4.opExtrude","CAP_EDGE",EDGE,{"disambiguationData":[OSD([subQ0]),TDD([makeQuery(id+"F3.imprint","IMPRINT",EDGE,{"disambiguationData":[TD([[makeQuery(id+"F3.imprint","INTERSECT",VERTEX,{"derivedFrom":[subQ1,sQuery(id+"F3.wireOp",EDGE,"E4.32.0.0")]}),1.0]])],"derivedFrom":subQ1})])],"isStart":false});}
            var Q109;
            {var subQ0=sQuery(id+"F0.wireOp",EDGE,"E2.top");var subQ1=makeQuery(id+"F1.opExtrude","CAP_EDGE",EDGE,{"disambiguationData":[OSD([subQ0])],"isStart":false});Q109=makeQuery(id+"F4.opExtrude","CAP_EDGE",EDGE,{"disambiguationData":[OSD([subQ0]),TDD([makeQuery(id+"F3.imprint","IMPRINT",EDGE,{"disambiguationData":[TD([[makeQuery(id+"F3.imprint","INTERSECT",VERTEX,{"derivedFrom":[subQ1,sQuery(id+"F3.wireOp",EDGE,"E4.33.0.0")]}),1.0]])],"derivedFrom":subQ1})])],"isStart":false});}
            var Q110;
            {var subQ0=sQuery(id+"F0.wireOp",EDGE,"E2.top");var subQ1=makeQuery(id+"F1.opExtrude","CAP_EDGE",EDGE,{"disambiguationData":[OSD([subQ0])],"isStart":false});Q110=makeQuery(id+"F4.opExtrude","CAP_EDGE",EDGE,{"disambiguationData":[OSD([subQ0]),TDD([makeQuery(id+"F3.imprint","IMPRINT",EDGE,{"disambiguationData":[TD([[makeQuery(id+"F3.imprint","INTERSECT",VERTEX,{"derivedFrom":[subQ1,sQuery(id+"F3.wireOp",EDGE,"E4.34.0.0")]}),1.0]])],"derivedFrom":subQ1})])],"isStart":false});}
            var Q111;
            {var subQ0=sQuery(id+"F0.wireOp",EDGE,"E2.top");var subQ1=makeQuery(id+"F1.opExtrude","CAP_EDGE",EDGE,{"disambiguationData":[OSD([subQ0])],"isStart":false});Q111=makeQuery(id+"F4.opExtrude","CAP_EDGE",EDGE,{"disambiguationData":[OSD([subQ0]),TDD([makeQuery(id+"F3.imprint","IMPRINT",EDGE,{"disambiguationData":[TD([[makeQuery(id+"F3.imprint","INTERSECT",VERTEX,{"derivedFrom":[subQ1,sQuery(id+"F3.wireOp",EDGE,"E4.35.0.0")]}),1.0]])],"derivedFrom":subQ1})])],"isStart":false});}
            var Q112;
            {var subQ0=sQuery(id+"F0.wireOp",EDGE,"E2.top");var subQ1=makeQuery(id+"F1.opExtrude","CAP_EDGE",EDGE,{"disambiguationData":[OSD([subQ0])],"isStart":false});Q112=makeQuery(id+"F4.opExtrude","CAP_EDGE",EDGE,{"disambiguationData":[OSD([subQ0]),TDD([makeQuery(id+"F3.imprint","IMPRINT",EDGE,{"disambiguationData":[TD([[makeQuery(id+"F3.imprint","INTERSECT",VERTEX,{"derivedFrom":[subQ1,sQuery(id+"F3.wireOp",EDGE,"E4.36.0.0")]}),1.0]])],"derivedFrom":subQ1})])],"isStart":false});}
            var Q113;
            {var subQ0=sQuery(id+"F0.wireOp",EDGE,"E2.top");var subQ1=makeQuery(id+"F1.opExtrude","CAP_EDGE",EDGE,{"disambiguationData":[OSD([subQ0])],"isStart":false});Q113=makeQuery(id+"F4.opExtrude","CAP_EDGE",EDGE,{"disambiguationData":[OSD([subQ0]),TDD([makeQuery(id+"F3.imprint","IMPRINT",EDGE,{"disambiguationData":[TD([[makeQuery(id+"F3.imprint","INTERSECT",VERTEX,{"derivedFrom":[subQ1,sQuery(id+"F3.wireOp",EDGE,"E4.37.0.1")]}),-1.0]])],"derivedFrom":subQ1})])],"isStart":false});}
            var Q114;
            {var subQ0=sQuery(id+"F0.wireOp",EDGE,"E2.top");var subQ1=makeQuery(id+"F1.opExtrude","CAP_EDGE",EDGE,{"disambiguationData":[OSD([subQ0])],"isStart":false});Q114=makeQuery(id+"F4.opExtrude","CAP_EDGE",EDGE,{"disambiguationData":[OSD([subQ0]),TDD([makeQuery(id+"F3.imprint","IMPRINT",EDGE,{"disambiguationData":[TD([[makeQuery(id+"F3.imprint","INTERSECT",VERTEX,{"derivedFrom":[subQ1,sQuery(id+"F3.wireOp",EDGE,"E4.3.0.0")]}),1.0]])],"derivedFrom":subQ1})])],"isStart":false});}
            var Q115;
            Q115=makeQuery(id+"F4.opExtrude","CAP_EDGE",EDGE,{"disambiguationData":[OSD([sQuery(id+"F3.wireOp",EDGE,"E4.37.0.2")])],"isStart":false});
            var Q116;
            Q116=makeQuery(id+"F4.opExtrude","CAP_EDGE",EDGE,{"disambiguationData":[OSD([sQuery(id+"F3.wireOp",EDGE,"E4.36.0.2")])],"isStart":false});
            var Q117;
            Q117=makeQuery(id+"F4.opExtrude","CAP_EDGE",EDGE,{"disambiguationData":[OSD([sQuery(id+"F3.wireOp",EDGE,"E4.35.0.2")])],"isStart":false});
            var Q118;
            Q118=makeQuery(id+"F4.opExtrude","CAP_EDGE",EDGE,{"disambiguationData":[OSD([sQuery(id+"F3.wireOp",EDGE,"E4.34.0.2")])],"isStart":false});
            var Q119;
            Q119=makeQuery(id+"F4.opExtrude","CAP_EDGE",EDGE,{"disambiguationData":[OSD([sQuery(id+"F3.wireOp",EDGE,"E4.33.0.2")])],"isStart":false});
            var Q120;
            Q120=makeQuery(id+"F4.opExtrude","CAP_EDGE",EDGE,{"disambiguationData":[OSD([sQuery(id+"F3.wireOp",EDGE,"E4.32.0.2")])],"isStart":false});
            var Q121;
            Q121=makeQuery(id+"F4.opExtrude","CAP_EDGE",EDGE,{"disambiguationData":[OSD([sQuery(id+"F3.wireOp",EDGE,"E4.31.0.2")])],"isStart":false});
            var Q122;
            Q122=makeQuery(id+"F4.opExtrude","CAP_EDGE",EDGE,{"disambiguationData":[OSD([sQuery(id+"F3.wireOp",EDGE,"E4.30.0.2")])],"isStart":false});
            var Q123;
            Q123=makeQuery(id+"F4.opExtrude","CAP_EDGE",EDGE,{"disambiguationData":[OSD([sQuery(id+"F3.wireOp",EDGE,"E4.29.0.2")])],"isStart":false});
            var Q124;
            Q124=makeQuery(id+"F4.opExtrude","CAP_EDGE",EDGE,{"disambiguationData":[OSD([sQuery(id+"F3.wireOp",EDGE,"E4.28.0.2")])],"isStart":false});
            var Q125;
            Q125=makeQuery(id+"F4.opExtrude","CAP_EDGE",EDGE,{"disambiguationData":[OSD([sQuery(id+"F3.wireOp",EDGE,"E4.27.0.2")])],"isStart":false});
            var Q126;
            Q126=makeQuery(id+"F4.opExtrude","CAP_EDGE",EDGE,{"disambiguationData":[OSD([sQuery(id+"F3.wireOp",EDGE,"E4.26.0.2")])],"isStart":false});
            var Q127;
            Q127=makeQuery(id+"F4.opExtrude","CAP_EDGE",EDGE,{"disambiguationData":[OSD([sQuery(id+"F3.wireOp",EDGE,"E4.25.0.2")])],"isStart":false});
            var Q128;
            Q128=makeQuery(id+"F4.opExtrude","CAP_EDGE",EDGE,{"disambiguationData":[OSD([sQuery(id+"F3.wireOp",EDGE,"E4.24.0.2")])],"isStart":false});
            var Q129;
            Q129=makeQuery(id+"F4.opExtrude","CAP_EDGE",EDGE,{"disambiguationData":[OSD([sQuery(id+"F3.wireOp",EDGE,"E4.23.0.2")])],"isStart":false});
            var Q130;
            Q130=makeQuery(id+"F4.opExtrude","CAP_EDGE",EDGE,{"disambiguationData":[OSD([sQuery(id+"F3.wireOp",EDGE,"E4.22.0.2")])],"isStart":false});
            var Q131;
            Q131=makeQuery(id+"F4.opExtrude","CAP_EDGE",EDGE,{"disambiguationData":[OSD([sQuery(id+"F3.wireOp",EDGE,"E4.20.0.2")])],"isStart":false});
            var Q132;
            Q132=makeQuery(id+"F4.opExtrude","CAP_EDGE",EDGE,{"disambiguationData":[OSD([sQuery(id+"F3.wireOp",EDGE,"E4.19.0.2")])],"isStart":false});
            var Q133;
            Q133=makeQuery(id+"F4.opExtrude","CAP_EDGE",EDGE,{"disambiguationData":[OSD([sQuery(id+"F3.wireOp",EDGE,"E4.18.0.2")])],"isStart":false});
            var Q134;
            Q134=makeQuery(id+"F4.opExtrude","CAP_EDGE",EDGE,{"disambiguationData":[OSD([sQuery(id+"F3.wireOp",EDGE,"E4.16.0.2")])],"isStart":false});
            var Q135;
            Q135=makeQuery(id+"F4.opExtrude","CAP_EDGE",EDGE,{"disambiguationData":[OSD([sQuery(id+"F3.wireOp",EDGE,"E4.15.0.2")])],"isStart":false});
            var Q136;
            Q136=makeQuery(id+"F4.opExtrude","CAP_EDGE",EDGE,{"disambiguationData":[OSD([sQuery(id+"F3.wireOp",EDGE,"E4.14.0.2")])],"isStart":false});
            var Q137;
            Q137=makeQuery(id+"F4.opExtrude","CAP_EDGE",EDGE,{"disambiguationData":[OSD([sQuery(id+"F3.wireOp",EDGE,"E4.13.0.2")])],"isStart":false});
            var Q138;
            Q138=makeQuery(id+"F4.opExtrude","CAP_EDGE",EDGE,{"disambiguationData":[OSD([sQuery(id+"F3.wireOp",EDGE,"E4.12.0.2")])],"isStart":false});
            var Q139;
            Q139=makeQuery(id+"F4.opExtrude","CAP_EDGE",EDGE,{"disambiguationData":[OSD([sQuery(id+"F3.wireOp",EDGE,"E4.11.0.2")])],"isStart":false});
            var Q140;
            Q140=makeQuery(id+"F4.opExtrude","CAP_EDGE",EDGE,{"disambiguationData":[OSD([sQuery(id+"F3.wireOp",EDGE,"E4.17.0.2")])],"isStart":false});
            var Q141;
            Q141=makeQuery(id+"F4.opExtrude","CAP_EDGE",EDGE,{"disambiguationData":[OSD([sQuery(id+"F3.wireOp",EDGE,"E4.10.0.2")])],"isStart":false});
            var Q142;
            Q142=makeQuery(id+"F4.opExtrude","CAP_EDGE",EDGE,{"disambiguationData":[OSD([sQuery(id+"F3.wireOp",EDGE,"E4.9.0.2")])],"isStart":false});
            var Q143;
            Q143=makeQuery(id+"F4.opExtrude","CAP_EDGE",EDGE,{"disambiguationData":[OSD([sQuery(id+"F3.wireOp",EDGE,"E4.8.0.2")])],"isStart":false});
            var Q144;
            Q144=makeQuery(id+"F4.opExtrude","CAP_EDGE",EDGE,{"disambiguationData":[OSD([sQuery(id+"F3.wireOp",EDGE,"E4.7.0.2")])],"isStart":false});
            var Q145;
            Q145=makeQuery(id+"F4.opExtrude","CAP_EDGE",EDGE,{"disambiguationData":[OSD([sQuery(id+"F3.wireOp",EDGE,"E4.6.0.2")])],"isStart":false});
            var Q146;
            Q146=makeQuery(id+"F4.opExtrude","CAP_EDGE",EDGE,{"disambiguationData":[OSD([sQuery(id+"F3.wireOp",EDGE,"E4.5.0.2")])],"isStart":false});
            var Q147;
            Q147=makeQuery(id+"F4.opExtrude","CAP_EDGE",EDGE,{"disambiguationData":[OSD([sQuery(id+"F3.wireOp",EDGE,"E4.4.0.2")])],"isStart":false});
            var Q148;
            Q148=makeQuery(id+"F4.opExtrude","CAP_EDGE",EDGE,{"disambiguationData":[OSD([sQuery(id+"F3.wireOp",EDGE,"E4.3.0.2")])],"isStart":false});
            var Q149;
            Q149=makeQuery(id+"F4.opExtrude","CAP_EDGE",EDGE,{"disambiguationData":[OSD([sQuery(id+"F3.wireOp",EDGE,"E4.2.0.2")])],"isStart":false});
            var Q150;
            Q150=makeQuery(id+"F4.opExtrude","CAP_EDGE",EDGE,{"disambiguationData":[OSD([sQuery(id+"F3.wireOp",EDGE,"E4.1.0.2")])],"isStart":false});
            var Q151;
            Q151=makeQuery(id+"F4.opExtrude","CAP_EDGE",EDGE,{"disambiguationData":[OSD([sQuery(id+"F3.wireOp",EDGE,"E3.bottom")])],"isStart":false});
            chamfer(context, id + "F5", {"entities" : qUnion([Q0, Q1, Q2, Q3, Q4, Q5, Q6, Q7, Q8, Q9, Q10, Q11, Q12, Q13, Q14, Q15, Q16, Q17, Q18, Q19, Q20, Q21, Q22, Q23, Q24, Q25, Q26, Q27, Q28, Q29, Q30, Q31, Q32, Q33, Q34, Q35, Q36, Q37, Q38, Q39, Q40, Q41, Q42, Q43, Q44, Q45, Q46, Q47, Q48, Q49, Q50, Q51, Q52, Q53, Q54, Q55, Q56, Q57, Q58, Q59, Q60, Q61, Q62, Q63, Q64, Q65, Q66, Q67, Q68, Q69, Q70, Q71, Q72, Q73, Q74, Q75, Q76, Q77, Q78, Q79, Q80, Q81, Q82, Q83, Q84, Q85, Q86, Q87, Q88, Q89, Q90, Q91, Q92, Q93, Q94, Q95, Q96, Q97, Q98, Q99, Q100, Q101, Q102, Q103, Q104, Q105, Q106, Q107, Q108, Q109, Q110, Q111, Q112, Q113, Q114, Q115, Q116, Q117, Q118, Q119, Q120, Q121, Q122, Q123, Q124, Q125, Q126, Q127, Q128, Q129, Q130, Q131, Q132, Q133, Q134, Q135, Q136, Q137, Q138, Q139, Q140, Q141, Q142, Q143, Q144, Q145, Q146, Q147, Q148, Q149, Q150, Q151]), "width" : 1 * mm, "tangentPropagation" : true});
        }
        {
            var Q0;
            {var subQ0=sQuery(id+"F3.wireOp",EDGE,"E4.37.0.0");Q0=makeQuery(id+"F4.opExtrude","CAP_EDGE",EDGE,{"disambiguationData":[OSD([subQ0]),TDD([makeQuery(id+"F3.imprint","IMPRINT",EDGE,{"disambiguationData":[TD([[makeQuery(id+"F3.imprint","INTERSECT",VERTEX,{"derivedFrom":[makeQuery(id+"F1.opExtrude","CAP_EDGE",EDGE,{"disambiguationData":[OSD([sQuery(id+"F0.wireOp",EDGE,"E2.bottom")])],"isStart":false}),subQ0]}),1.0]])],"derivedFrom":subQ0})])],"isStart":false});}
            var Q1;
            {var subQ0=sQuery(id+"F3.wireOp",EDGE,"E4.37.0.1");var subQ1=sQuery(id+"F0.wireOp",EDGE,"E2.bottom");Q1=makeQuery(id+"F4.opExtrude","CAP_EDGE",EDGE,{"disambiguationData":[OSD([subQ0]),TDD([makeQuery(id+"F3.imprint","IMPRINT",EDGE,{"disambiguationData":[TD([[makeQuery(id+"F3.imprint","INTERSECT",VERTEX,{"derivedFrom":[makeQuery(id+"F1.opExtrude","CAP_EDGE",EDGE,{"disambiguationData":[OSD([subQ1])],"isStart":false}),subQ0]}),1.0]])],"derivedFrom":subQ0})])],"isStart":false});}
            var Q2;
            {var subQ0=sQuery(id+"F3.wireOp",EDGE,"E4.36.0.1");Q2=makeQuery(id+"F4.opExtrude","CAP_EDGE",EDGE,{"disambiguationData":[OSD([subQ0]),TDD([makeQuery(id+"F3.imprint","IMPRINT",EDGE,{"disambiguationData":[TD([[makeQuery(id+"F3.imprint","INTERSECT",VERTEX,{"derivedFrom":[makeQuery(id+"F1.opExtrude","CAP_EDGE",EDGE,{"disambiguationData":[OSD([sQuery(id+"F0.wireOp",EDGE,"E2.bottom")])],"isStart":false}),subQ0]}),1.0]])],"derivedFrom":subQ0})])],"isStart":false});}
            var Q3;
            {var subQ0=sQuery(id+"F3.wireOp",EDGE,"E4.36.0.0");Q3=makeQuery(id+"F4.opExtrude","CAP_EDGE",EDGE,{"disambiguationData":[OSD([subQ0]),TDD([makeQuery(id+"F3.imprint","IMPRINT",EDGE,{"disambiguationData":[TD([[makeQuery(id+"F3.imprint","INTERSECT",VERTEX,{"derivedFrom":[makeQuery(id+"F1.opExtrude","CAP_EDGE",EDGE,{"disambiguationData":[OSD([sQuery(id+"F0.wireOp",EDGE,"E2.bottom")])],"isStart":false}),subQ0]}),1.0]])],"derivedFrom":subQ0})])],"isStart":false});}
            var Q4;
            {var subQ0=sQuery(id+"F3.wireOp",EDGE,"E4.35.0.1");Q4=makeQuery(id+"F4.opExtrude","CAP_EDGE",EDGE,{"disambiguationData":[OSD([subQ0]),TDD([makeQuery(id+"F3.imprint","IMPRINT",EDGE,{"disambiguationData":[TD([[makeQuery(id+"F3.imprint","INTERSECT",VERTEX,{"derivedFrom":[makeQuery(id+"F1.opExtrude","CAP_EDGE",EDGE,{"disambiguationData":[OSD([sQuery(id+"F0.wireOp",EDGE,"E2.bottom")])],"isStart":false}),subQ0]}),1.0]])],"derivedFrom":subQ0})])],"isStart":false});}
            var Q5;
            {var subQ0=sQuery(id+"F3.wireOp",EDGE,"E4.35.0.0");Q5=makeQuery(id+"F4.opExtrude","CAP_EDGE",EDGE,{"disambiguationData":[OSD([subQ0]),TDD([makeQuery(id+"F3.imprint","IMPRINT",EDGE,{"disambiguationData":[TD([[makeQuery(id+"F3.imprint","INTERSECT",VERTEX,{"derivedFrom":[makeQuery(id+"F1.opExtrude","CAP_EDGE",EDGE,{"disambiguationData":[OSD([sQuery(id+"F0.wireOp",EDGE,"E2.bottom")])],"isStart":false}),subQ0]}),1.0]])],"derivedFrom":subQ0})])],"isStart":false});}
            var Q6;
            {var subQ0=sQuery(id+"F3.wireOp",EDGE,"E4.34.0.1");Q6=makeQuery(id+"F4.opExtrude","CAP_EDGE",EDGE,{"disambiguationData":[OSD([subQ0]),TDD([makeQuery(id+"F3.imprint","IMPRINT",EDGE,{"disambiguationData":[TD([[makeQuery(id+"F3.imprint","INTERSECT",VERTEX,{"derivedFrom":[makeQuery(id+"F1.opExtrude","CAP_EDGE",EDGE,{"disambiguationData":[OSD([sQuery(id+"F0.wireOp",EDGE,"E2.bottom")])],"isStart":false}),subQ0]}),1.0]])],"derivedFrom":subQ0})])],"isStart":false});}
            var Q7;
            {var subQ0=sQuery(id+"F3.wireOp",EDGE,"E4.34.0.0");Q7=makeQuery(id+"F4.opExtrude","CAP_EDGE",EDGE,{"disambiguationData":[OSD([subQ0]),TDD([makeQuery(id+"F3.imprint","IMPRINT",EDGE,{"disambiguationData":[TD([[makeQuery(id+"F3.imprint","INTERSECT",VERTEX,{"derivedFrom":[makeQuery(id+"F1.opExtrude","CAP_EDGE",EDGE,{"disambiguationData":[OSD([sQuery(id+"F0.wireOp",EDGE,"E2.bottom")])],"isStart":false}),subQ0]}),1.0]])],"derivedFrom":subQ0})])],"isStart":false});}
            var Q8;
            {var subQ0=sQuery(id+"F3.wireOp",EDGE,"E4.33.0.1");Q8=makeQuery(id+"F4.opExtrude","CAP_EDGE",EDGE,{"disambiguationData":[OSD([subQ0]),TDD([makeQuery(id+"F3.imprint","IMPRINT",EDGE,{"disambiguationData":[TD([[makeQuery(id+"F3.imprint","INTERSECT",VERTEX,{"derivedFrom":[makeQuery(id+"F1.opExtrude","CAP_EDGE",EDGE,{"disambiguationData":[OSD([sQuery(id+"F0.wireOp",EDGE,"E2.bottom")])],"isStart":false}),subQ0]}),1.0]])],"derivedFrom":subQ0})])],"isStart":false});}
            var Q9;
            {var subQ0=sQuery(id+"F3.wireOp",EDGE,"E4.33.0.0");Q9=makeQuery(id+"F4.opExtrude","CAP_EDGE",EDGE,{"disambiguationData":[OSD([subQ0]),TDD([makeQuery(id+"F3.imprint","IMPRINT",EDGE,{"disambiguationData":[TD([[makeQuery(id+"F3.imprint","INTERSECT",VERTEX,{"derivedFrom":[makeQuery(id+"F1.opExtrude","CAP_EDGE",EDGE,{"disambiguationData":[OSD([sQuery(id+"F0.wireOp",EDGE,"E2.bottom")])],"isStart":false}),subQ0]}),1.0]])],"derivedFrom":subQ0})])],"isStart":false});}
            var Q10;
            {var subQ0=sQuery(id+"F3.wireOp",EDGE,"E4.32.0.1");Q10=makeQuery(id+"F4.opExtrude","CAP_EDGE",EDGE,{"disambiguationData":[OSD([subQ0]),TDD([makeQuery(id+"F3.imprint","IMPRINT",EDGE,{"disambiguationData":[TD([[makeQuery(id+"F3.imprint","INTERSECT",VERTEX,{"derivedFrom":[makeQuery(id+"F1.opExtrude","CAP_EDGE",EDGE,{"disambiguationData":[OSD([sQuery(id+"F0.wireOp",EDGE,"E2.bottom")])],"isStart":false}),subQ0]}),1.0]])],"derivedFrom":subQ0})])],"isStart":false});}
            var Q11;
            {var subQ0=sQuery(id+"F3.wireOp",EDGE,"E4.32.0.0");Q11=makeQuery(id+"F4.opExtrude","CAP_EDGE",EDGE,{"disambiguationData":[OSD([subQ0]),TDD([makeQuery(id+"F3.imprint","IMPRINT",EDGE,{"disambiguationData":[TD([[makeQuery(id+"F3.imprint","INTERSECT",VERTEX,{"derivedFrom":[makeQuery(id+"F1.opExtrude","CAP_EDGE",EDGE,{"disambiguationData":[OSD([sQuery(id+"F0.wireOp",EDGE,"E2.bottom")])],"isStart":false}),subQ0]}),1.0]])],"derivedFrom":subQ0})])],"isStart":false});}
            var Q12;
            {var subQ0=sQuery(id+"F3.wireOp",EDGE,"E4.31.0.1");Q12=makeQuery(id+"F4.opExtrude","CAP_EDGE",EDGE,{"disambiguationData":[OSD([subQ0]),TDD([makeQuery(id+"F3.imprint","IMPRINT",EDGE,{"disambiguationData":[TD([[makeQuery(id+"F3.imprint","INTERSECT",VERTEX,{"derivedFrom":[makeQuery(id+"F1.opExtrude","CAP_EDGE",EDGE,{"disambiguationData":[OSD([sQuery(id+"F0.wireOp",EDGE,"E2.bottom")])],"isStart":false}),subQ0]}),1.0]])],"derivedFrom":subQ0})])],"isStart":false});}
            var Q13;
            {var subQ0=sQuery(id+"F3.wireOp",EDGE,"E4.31.0.0");Q13=makeQuery(id+"F4.opExtrude","CAP_EDGE",EDGE,{"disambiguationData":[OSD([subQ0]),TDD([makeQuery(id+"F3.imprint","IMPRINT",EDGE,{"disambiguationData":[TD([[makeQuery(id+"F3.imprint","INTERSECT",VERTEX,{"derivedFrom":[makeQuery(id+"F1.opExtrude","CAP_EDGE",EDGE,{"disambiguationData":[OSD([sQuery(id+"F0.wireOp",EDGE,"E2.bottom")])],"isStart":false}),subQ0]}),1.0]])],"derivedFrom":subQ0})])],"isStart":false});}
            var Q14;
            {var subQ0=sQuery(id+"F3.wireOp",EDGE,"E4.30.0.1");Q14=makeQuery(id+"F4.opExtrude","CAP_EDGE",EDGE,{"disambiguationData":[OSD([subQ0]),TDD([makeQuery(id+"F3.imprint","IMPRINT",EDGE,{"disambiguationData":[TD([[makeQuery(id+"F3.imprint","INTERSECT",VERTEX,{"derivedFrom":[makeQuery(id+"F1.opExtrude","CAP_EDGE",EDGE,{"disambiguationData":[OSD([sQuery(id+"F0.wireOp",EDGE,"E2.bottom")])],"isStart":false}),subQ0]}),1.0]])],"derivedFrom":subQ0})])],"isStart":false});}
            var Q15;
            {var subQ0=sQuery(id+"F3.wireOp",EDGE,"E4.30.0.0");Q15=makeQuery(id+"F4.opExtrude","CAP_EDGE",EDGE,{"disambiguationData":[OSD([subQ0]),TDD([makeQuery(id+"F3.imprint","IMPRINT",EDGE,{"disambiguationData":[TD([[makeQuery(id+"F3.imprint","INTERSECT",VERTEX,{"derivedFrom":[makeQuery(id+"F1.opExtrude","CAP_EDGE",EDGE,{"disambiguationData":[OSD([sQuery(id+"F0.wireOp",EDGE,"E2.bottom")])],"isStart":false}),subQ0]}),1.0]])],"derivedFrom":subQ0})])],"isStart":false});}
            var Q16;
            {var subQ0=sQuery(id+"F3.wireOp",EDGE,"E4.29.0.1");Q16=makeQuery(id+"F4.opExtrude","CAP_EDGE",EDGE,{"disambiguationData":[OSD([subQ0]),TDD([makeQuery(id+"F3.imprint","IMPRINT",EDGE,{"disambiguationData":[TD([[makeQuery(id+"F3.imprint","INTERSECT",VERTEX,{"derivedFrom":[makeQuery(id+"F1.opExtrude","CAP_EDGE",EDGE,{"disambiguationData":[OSD([sQuery(id+"F0.wireOp",EDGE,"E2.bottom")])],"isStart":false}),subQ0]}),1.0]])],"derivedFrom":subQ0})])],"isStart":false});}
            var Q17;
            {var subQ0=sQuery(id+"F3.wireOp",EDGE,"E4.29.0.0");Q17=makeQuery(id+"F4.opExtrude","CAP_EDGE",EDGE,{"disambiguationData":[OSD([subQ0]),TDD([makeQuery(id+"F3.imprint","IMPRINT",EDGE,{"disambiguationData":[TD([[makeQuery(id+"F3.imprint","INTERSECT",VERTEX,{"derivedFrom":[makeQuery(id+"F1.opExtrude","CAP_EDGE",EDGE,{"disambiguationData":[OSD([sQuery(id+"F0.wireOp",EDGE,"E2.bottom")])],"isStart":false}),subQ0]}),1.0]])],"derivedFrom":subQ0})])],"isStart":false});}
            var Q18;
            {var subQ0=sQuery(id+"F3.wireOp",EDGE,"E4.28.0.1");Q18=makeQuery(id+"F4.opExtrude","CAP_EDGE",EDGE,{"disambiguationData":[OSD([subQ0]),TDD([makeQuery(id+"F3.imprint","IMPRINT",EDGE,{"disambiguationData":[TD([[makeQuery(id+"F3.imprint","INTERSECT",VERTEX,{"derivedFrom":[makeQuery(id+"F1.opExtrude","CAP_EDGE",EDGE,{"disambiguationData":[OSD([sQuery(id+"F0.wireOp",EDGE,"E2.bottom")])],"isStart":false}),subQ0]}),1.0]])],"derivedFrom":subQ0})])],"isStart":false});}
            var Q19;
            {var subQ0=sQuery(id+"F3.wireOp",EDGE,"E4.28.0.0");Q19=makeQuery(id+"F4.opExtrude","CAP_EDGE",EDGE,{"disambiguationData":[OSD([subQ0]),TDD([makeQuery(id+"F3.imprint","IMPRINT",EDGE,{"disambiguationData":[TD([[makeQuery(id+"F3.imprint","INTERSECT",VERTEX,{"derivedFrom":[makeQuery(id+"F1.opExtrude","CAP_EDGE",EDGE,{"disambiguationData":[OSD([sQuery(id+"F0.wireOp",EDGE,"E2.bottom")])],"isStart":false}),subQ0]}),1.0]])],"derivedFrom":subQ0})])],"isStart":false});}
            var Q20;
            {var subQ0=sQuery(id+"F3.wireOp",EDGE,"E4.27.0.1");Q20=makeQuery(id+"F4.opExtrude","CAP_EDGE",EDGE,{"disambiguationData":[OSD([subQ0]),TDD([makeQuery(id+"F3.imprint","IMPRINT",EDGE,{"disambiguationData":[TD([[makeQuery(id+"F3.imprint","INTERSECT",VERTEX,{"derivedFrom":[makeQuery(id+"F1.opExtrude","CAP_EDGE",EDGE,{"disambiguationData":[OSD([sQuery(id+"F0.wireOp",EDGE,"E2.bottom")])],"isStart":false}),subQ0]}),1.0]])],"derivedFrom":subQ0})])],"isStart":false});}
            var Q21;
            {var subQ0=sQuery(id+"F3.wireOp",EDGE,"E4.27.0.0");Q21=makeQuery(id+"F4.opExtrude","CAP_EDGE",EDGE,{"disambiguationData":[OSD([subQ0]),TDD([makeQuery(id+"F3.imprint","IMPRINT",EDGE,{"disambiguationData":[TD([[makeQuery(id+"F3.imprint","INTERSECT",VERTEX,{"derivedFrom":[makeQuery(id+"F1.opExtrude","CAP_EDGE",EDGE,{"disambiguationData":[OSD([sQuery(id+"F0.wireOp",EDGE,"E2.bottom")])],"isStart":false}),subQ0]}),1.0]])],"derivedFrom":subQ0})])],"isStart":false});}
            var Q22;
            {var subQ0=sQuery(id+"F3.wireOp",EDGE,"E4.26.0.1");Q22=makeQuery(id+"F4.opExtrude","CAP_EDGE",EDGE,{"disambiguationData":[OSD([subQ0]),TDD([makeQuery(id+"F3.imprint","IMPRINT",EDGE,{"disambiguationData":[TD([[makeQuery(id+"F3.imprint","INTERSECT",VERTEX,{"derivedFrom":[makeQuery(id+"F1.opExtrude","CAP_EDGE",EDGE,{"disambiguationData":[OSD([sQuery(id+"F0.wireOp",EDGE,"E2.bottom")])],"isStart":false}),subQ0]}),1.0]])],"derivedFrom":subQ0})])],"isStart":false});}
            var Q23;
            {var subQ0=sQuery(id+"F3.wireOp",EDGE,"E4.26.0.0");Q23=makeQuery(id+"F4.opExtrude","CAP_EDGE",EDGE,{"disambiguationData":[OSD([subQ0]),TDD([makeQuery(id+"F3.imprint","IMPRINT",EDGE,{"disambiguationData":[TD([[makeQuery(id+"F3.imprint","INTERSECT",VERTEX,{"derivedFrom":[makeQuery(id+"F1.opExtrude","CAP_EDGE",EDGE,{"disambiguationData":[OSD([sQuery(id+"F0.wireOp",EDGE,"E2.bottom")])],"isStart":false}),subQ0]}),1.0]])],"derivedFrom":subQ0})])],"isStart":false});}
            var Q24;
            {var subQ0=sQuery(id+"F3.wireOp",EDGE,"E4.25.0.0");Q24=makeQuery(id+"F4.opExtrude","CAP_EDGE",EDGE,{"disambiguationData":[OSD([subQ0]),TDD([makeQuery(id+"F3.imprint","IMPRINT",EDGE,{"disambiguationData":[TD([[makeQuery(id+"F3.imprint","INTERSECT",VERTEX,{"derivedFrom":[makeQuery(id+"F1.opExtrude","CAP_EDGE",EDGE,{"disambiguationData":[OSD([sQuery(id+"F0.wireOp",EDGE,"E2.bottom")])],"isStart":false}),subQ0]}),1.0]])],"derivedFrom":subQ0})])],"isStart":false});}
            var Q25;
            {var subQ0=sQuery(id+"F3.wireOp",EDGE,"E4.25.0.1");Q25=makeQuery(id+"F4.opExtrude","CAP_EDGE",EDGE,{"disambiguationData":[OSD([subQ0]),TDD([makeQuery(id+"F3.imprint","IMPRINT",EDGE,{"disambiguationData":[TD([[makeQuery(id+"F3.imprint","INTERSECT",VERTEX,{"derivedFrom":[makeQuery(id+"F1.opExtrude","CAP_EDGE",EDGE,{"disambiguationData":[OSD([sQuery(id+"F0.wireOp",EDGE,"E2.bottom")])],"isStart":false}),subQ0]}),1.0]])],"derivedFrom":subQ0})])],"isStart":false});}
            var Q26;
            {var subQ0=sQuery(id+"F3.wireOp",EDGE,"E4.24.0.1");Q26=makeQuery(id+"F4.opExtrude","CAP_EDGE",EDGE,{"disambiguationData":[OSD([subQ0]),TDD([makeQuery(id+"F3.imprint","IMPRINT",EDGE,{"disambiguationData":[TD([[makeQuery(id+"F3.imprint","INTERSECT",VERTEX,{"derivedFrom":[makeQuery(id+"F1.opExtrude","CAP_EDGE",EDGE,{"disambiguationData":[OSD([sQuery(id+"F0.wireOp",EDGE,"E2.bottom")])],"isStart":false}),subQ0]}),1.0]])],"derivedFrom":subQ0})])],"isStart":false});}
            var Q27;
            {var subQ0=sQuery(id+"F3.wireOp",EDGE,"E4.24.0.0");Q27=makeQuery(id+"F4.opExtrude","CAP_EDGE",EDGE,{"disambiguationData":[OSD([subQ0]),TDD([makeQuery(id+"F3.imprint","IMPRINT",EDGE,{"disambiguationData":[TD([[makeQuery(id+"F3.imprint","INTERSECT",VERTEX,{"derivedFrom":[makeQuery(id+"F1.opExtrude","CAP_EDGE",EDGE,{"disambiguationData":[OSD([sQuery(id+"F0.wireOp",EDGE,"E2.bottom")])],"isStart":false}),subQ0]}),1.0]])],"derivedFrom":subQ0})])],"isStart":false});}
            var Q28;
            {var subQ0=sQuery(id+"F3.wireOp",EDGE,"E4.23.0.1");Q28=makeQuery(id+"F4.opExtrude","CAP_EDGE",EDGE,{"disambiguationData":[OSD([subQ0]),TDD([makeQuery(id+"F3.imprint","IMPRINT",EDGE,{"disambiguationData":[TD([[makeQuery(id+"F3.imprint","INTERSECT",VERTEX,{"derivedFrom":[makeQuery(id+"F1.opExtrude","CAP_EDGE",EDGE,{"disambiguationData":[OSD([sQuery(id+"F0.wireOp",EDGE,"E2.bottom")])],"isStart":false}),subQ0]}),1.0]])],"derivedFrom":subQ0})])],"isStart":false});}
            var Q29;
            {var subQ0=sQuery(id+"F3.wireOp",EDGE,"E4.23.0.0");Q29=makeQuery(id+"F4.opExtrude","CAP_EDGE",EDGE,{"disambiguationData":[OSD([subQ0]),TDD([makeQuery(id+"F3.imprint","IMPRINT",EDGE,{"disambiguationData":[TD([[makeQuery(id+"F3.imprint","INTERSECT",VERTEX,{"derivedFrom":[makeQuery(id+"F1.opExtrude","CAP_EDGE",EDGE,{"disambiguationData":[OSD([sQuery(id+"F0.wireOp",EDGE,"E2.bottom")])],"isStart":false}),subQ0]}),1.0]])],"derivedFrom":subQ0})])],"isStart":false});}
            var Q30;
            {var subQ0=sQuery(id+"F3.wireOp",EDGE,"E4.22.0.1");Q30=makeQuery(id+"F4.opExtrude","CAP_EDGE",EDGE,{"disambiguationData":[OSD([subQ0]),TDD([makeQuery(id+"F3.imprint","IMPRINT",EDGE,{"disambiguationData":[TD([[makeQuery(id+"F3.imprint","INTERSECT",VERTEX,{"derivedFrom":[makeQuery(id+"F1.opExtrude","CAP_EDGE",EDGE,{"disambiguationData":[OSD([sQuery(id+"F0.wireOp",EDGE,"E2.bottom")])],"isStart":false}),subQ0]}),1.0]])],"derivedFrom":subQ0})])],"isStart":false});}
            var Q31;
            {var subQ0=sQuery(id+"F3.wireOp",EDGE,"E4.22.0.0");Q31=makeQuery(id+"F4.opExtrude","CAP_EDGE",EDGE,{"disambiguationData":[OSD([subQ0]),TDD([makeQuery(id+"F3.imprint","IMPRINT",EDGE,{"disambiguationData":[TD([[makeQuery(id+"F3.imprint","INTERSECT",VERTEX,{"derivedFrom":[makeQuery(id+"F1.opExtrude","CAP_EDGE",EDGE,{"disambiguationData":[OSD([sQuery(id+"F0.wireOp",EDGE,"E2.bottom")])],"isStart":false}),subQ0]}),1.0]])],"derivedFrom":subQ0})])],"isStart":false});}
            var Q32;
            {var subQ0=sQuery(id+"F3.wireOp",EDGE,"E4.21.0.1");Q32=makeQuery(id+"F4.opExtrude","CAP_EDGE",EDGE,{"disambiguationData":[OSD([subQ0]),TDD([makeQuery(id+"F3.imprint","IMPRINT",EDGE,{"disambiguationData":[TD([[makeQuery(id+"F3.imprint","INTERSECT",VERTEX,{"derivedFrom":[makeQuery(id+"F1.opExtrude","CAP_EDGE",EDGE,{"disambiguationData":[OSD([sQuery(id+"F0.wireOp",EDGE,"E2.bottom")])],"isStart":false}),subQ0]}),1.0]])],"derivedFrom":subQ0})])],"isStart":false});}
            var Q33;
            {var subQ0=sQuery(id+"F3.wireOp",EDGE,"E4.21.0.0");Q33=makeQuery(id+"F4.opExtrude","CAP_EDGE",EDGE,{"disambiguationData":[OSD([subQ0]),TDD([makeQuery(id+"F3.imprint","IMPRINT",EDGE,{"disambiguationData":[TD([[makeQuery(id+"F3.imprint","INTERSECT",VERTEX,{"derivedFrom":[makeQuery(id+"F1.opExtrude","CAP_EDGE",EDGE,{"disambiguationData":[OSD([sQuery(id+"F0.wireOp",EDGE,"E2.bottom")])],"isStart":false}),subQ0]}),1.0]])],"derivedFrom":subQ0})])],"isStart":false});}
            var Q34;
            {var subQ0=sQuery(id+"F3.wireOp",EDGE,"E4.20.0.1");Q34=makeQuery(id+"F4.opExtrude","CAP_EDGE",EDGE,{"disambiguationData":[OSD([subQ0]),TDD([makeQuery(id+"F3.imprint","IMPRINT",EDGE,{"disambiguationData":[TD([[makeQuery(id+"F3.imprint","INTERSECT",VERTEX,{"derivedFrom":[makeQuery(id+"F1.opExtrude","CAP_EDGE",EDGE,{"disambiguationData":[OSD([sQuery(id+"F0.wireOp",EDGE,"E2.bottom")])],"isStart":false}),subQ0]}),1.0]])],"derivedFrom":subQ0})])],"isStart":false});}
            var Q35;
            {var subQ0=sQuery(id+"F3.wireOp",EDGE,"E4.20.0.0");Q35=makeQuery(id+"F4.opExtrude","CAP_EDGE",EDGE,{"disambiguationData":[OSD([subQ0]),TDD([makeQuery(id+"F3.imprint","IMPRINT",EDGE,{"disambiguationData":[TD([[makeQuery(id+"F3.imprint","INTERSECT",VERTEX,{"derivedFrom":[makeQuery(id+"F1.opExtrude","CAP_EDGE",EDGE,{"disambiguationData":[OSD([sQuery(id+"F0.wireOp",EDGE,"E2.bottom")])],"isStart":false}),subQ0]}),1.0]])],"derivedFrom":subQ0})])],"isStart":false});}
            var Q36;
            {var subQ0=sQuery(id+"F3.wireOp",EDGE,"E4.19.0.1");Q36=makeQuery(id+"F4.opExtrude","CAP_EDGE",EDGE,{"disambiguationData":[OSD([subQ0]),TDD([makeQuery(id+"F3.imprint","IMPRINT",EDGE,{"disambiguationData":[TD([[makeQuery(id+"F3.imprint","INTERSECT",VERTEX,{"derivedFrom":[makeQuery(id+"F1.opExtrude","CAP_EDGE",EDGE,{"disambiguationData":[OSD([sQuery(id+"F0.wireOp",EDGE,"E2.bottom")])],"isStart":false}),subQ0]}),1.0]])],"derivedFrom":subQ0})])],"isStart":false});}
            var Q37;
            {var subQ0=sQuery(id+"F3.wireOp",EDGE,"E4.19.0.0");Q37=makeQuery(id+"F4.opExtrude","CAP_EDGE",EDGE,{"disambiguationData":[OSD([subQ0]),TDD([makeQuery(id+"F3.imprint","IMPRINT",EDGE,{"disambiguationData":[TD([[makeQuery(id+"F3.imprint","INTERSECT",VERTEX,{"derivedFrom":[makeQuery(id+"F1.opExtrude","CAP_EDGE",EDGE,{"disambiguationData":[OSD([sQuery(id+"F0.wireOp",EDGE,"E2.bottom")])],"isStart":false}),subQ0]}),1.0]])],"derivedFrom":subQ0})])],"isStart":false});}
            var Q38;
            {var subQ0=sQuery(id+"F3.wireOp",EDGE,"E4.18.0.1");Q38=makeQuery(id+"F4.opExtrude","CAP_EDGE",EDGE,{"disambiguationData":[OSD([subQ0]),TDD([makeQuery(id+"F3.imprint","IMPRINT",EDGE,{"disambiguationData":[TD([[makeQuery(id+"F3.imprint","INTERSECT",VERTEX,{"derivedFrom":[makeQuery(id+"F1.opExtrude","CAP_EDGE",EDGE,{"disambiguationData":[OSD([sQuery(id+"F0.wireOp",EDGE,"E2.bottom")])],"isStart":false}),subQ0]}),1.0]])],"derivedFrom":subQ0})])],"isStart":false});}
            var Q39;
            {var subQ0=sQuery(id+"F3.wireOp",EDGE,"E4.18.0.0");Q39=makeQuery(id+"F4.opExtrude","CAP_EDGE",EDGE,{"disambiguationData":[OSD([subQ0]),TDD([makeQuery(id+"F3.imprint","IMPRINT",EDGE,{"disambiguationData":[TD([[makeQuery(id+"F3.imprint","INTERSECT",VERTEX,{"derivedFrom":[makeQuery(id+"F1.opExtrude","CAP_EDGE",EDGE,{"disambiguationData":[OSD([sQuery(id+"F0.wireOp",EDGE,"E2.bottom")])],"isStart":false}),subQ0]}),1.0]])],"derivedFrom":subQ0})])],"isStart":false});}
            var Q40;
            {var subQ0=sQuery(id+"F3.wireOp",EDGE,"E4.17.0.1");Q40=makeQuery(id+"F4.opExtrude","CAP_EDGE",EDGE,{"disambiguationData":[OSD([subQ0]),TDD([makeQuery(id+"F3.imprint","IMPRINT",EDGE,{"disambiguationData":[TD([[makeQuery(id+"F3.imprint","INTERSECT",VERTEX,{"derivedFrom":[makeQuery(id+"F1.opExtrude","CAP_EDGE",EDGE,{"disambiguationData":[OSD([sQuery(id+"F0.wireOp",EDGE,"E2.bottom")])],"isStart":false}),subQ0]}),1.0]])],"derivedFrom":subQ0})])],"isStart":false});}
            var Q41;
            {var subQ0=sQuery(id+"F3.wireOp",EDGE,"E4.17.0.0");Q41=makeQuery(id+"F4.opExtrude","CAP_EDGE",EDGE,{"disambiguationData":[OSD([subQ0]),TDD([makeQuery(id+"F3.imprint","IMPRINT",EDGE,{"disambiguationData":[TD([[makeQuery(id+"F3.imprint","INTERSECT",VERTEX,{"derivedFrom":[makeQuery(id+"F1.opExtrude","CAP_EDGE",EDGE,{"disambiguationData":[OSD([sQuery(id+"F0.wireOp",EDGE,"E2.bottom")])],"isStart":false}),subQ0]}),1.0]])],"derivedFrom":subQ0})])],"isStart":false});}
            var Q42;
            {var subQ0=sQuery(id+"F3.wireOp",EDGE,"E4.16.0.1");Q42=makeQuery(id+"F4.opExtrude","CAP_EDGE",EDGE,{"disambiguationData":[OSD([subQ0]),TDD([makeQuery(id+"F3.imprint","IMPRINT",EDGE,{"disambiguationData":[TD([[makeQuery(id+"F3.imprint","INTERSECT",VERTEX,{"derivedFrom":[makeQuery(id+"F1.opExtrude","CAP_EDGE",EDGE,{"disambiguationData":[OSD([sQuery(id+"F0.wireOp",EDGE,"E2.bottom")])],"isStart":false}),subQ0]}),1.0]])],"derivedFrom":subQ0})])],"isStart":false});}
            var Q43;
            {var subQ0=sQuery(id+"F3.wireOp",EDGE,"E4.16.0.0");Q43=makeQuery(id+"F4.opExtrude","CAP_EDGE",EDGE,{"disambiguationData":[OSD([subQ0]),TDD([makeQuery(id+"F3.imprint","IMPRINT",EDGE,{"disambiguationData":[TD([[makeQuery(id+"F3.imprint","INTERSECT",VERTEX,{"derivedFrom":[makeQuery(id+"F1.opExtrude","CAP_EDGE",EDGE,{"disambiguationData":[OSD([sQuery(id+"F0.wireOp",EDGE,"E2.bottom")])],"isStart":false}),subQ0]}),1.0]])],"derivedFrom":subQ0})])],"isStart":false});}
            var Q44;
            {var subQ0=sQuery(id+"F3.wireOp",EDGE,"E4.15.0.1");Q44=makeQuery(id+"F4.opExtrude","CAP_EDGE",EDGE,{"disambiguationData":[OSD([subQ0]),TDD([makeQuery(id+"F3.imprint","IMPRINT",EDGE,{"disambiguationData":[TD([[makeQuery(id+"F3.imprint","INTERSECT",VERTEX,{"derivedFrom":[makeQuery(id+"F1.opExtrude","CAP_EDGE",EDGE,{"disambiguationData":[OSD([sQuery(id+"F0.wireOp",EDGE,"E2.bottom")])],"isStart":false}),subQ0]}),1.0]])],"derivedFrom":subQ0})])],"isStart":false});}
            var Q45;
            {var subQ0=sQuery(id+"F3.wireOp",EDGE,"E4.15.0.0");Q45=makeQuery(id+"F4.opExtrude","CAP_EDGE",EDGE,{"disambiguationData":[OSD([subQ0]),TDD([makeQuery(id+"F3.imprint","IMPRINT",EDGE,{"disambiguationData":[TD([[makeQuery(id+"F3.imprint","INTERSECT",VERTEX,{"derivedFrom":[makeQuery(id+"F1.opExtrude","CAP_EDGE",EDGE,{"disambiguationData":[OSD([sQuery(id+"F0.wireOp",EDGE,"E2.bottom")])],"isStart":false}),subQ0]}),1.0]])],"derivedFrom":subQ0})])],"isStart":false});}
            var Q46;
            {var subQ0=sQuery(id+"F3.wireOp",EDGE,"E4.14.0.1");Q46=makeQuery(id+"F4.opExtrude","CAP_EDGE",EDGE,{"disambiguationData":[OSD([subQ0]),TDD([makeQuery(id+"F3.imprint","IMPRINT",EDGE,{"disambiguationData":[TD([[makeQuery(id+"F3.imprint","INTERSECT",VERTEX,{"derivedFrom":[makeQuery(id+"F1.opExtrude","CAP_EDGE",EDGE,{"disambiguationData":[OSD([sQuery(id+"F0.wireOp",EDGE,"E2.bottom")])],"isStart":false}),subQ0]}),1.0]])],"derivedFrom":subQ0})])],"isStart":false});}
            var Q47;
            {var subQ0=sQuery(id+"F3.wireOp",EDGE,"E4.14.0.0");Q47=makeQuery(id+"F4.opExtrude","CAP_EDGE",EDGE,{"disambiguationData":[OSD([subQ0]),TDD([makeQuery(id+"F3.imprint","IMPRINT",EDGE,{"disambiguationData":[TD([[makeQuery(id+"F3.imprint","INTERSECT",VERTEX,{"derivedFrom":[makeQuery(id+"F1.opExtrude","CAP_EDGE",EDGE,{"disambiguationData":[OSD([sQuery(id+"F0.wireOp",EDGE,"E2.bottom")])],"isStart":false}),subQ0]}),1.0]])],"derivedFrom":subQ0})])],"isStart":false});}
            var Q48;
            {var subQ0=sQuery(id+"F3.wireOp",EDGE,"E4.13.0.1");Q48=makeQuery(id+"F4.opExtrude","CAP_EDGE",EDGE,{"disambiguationData":[OSD([subQ0]),TDD([makeQuery(id+"F3.imprint","IMPRINT",EDGE,{"disambiguationData":[TD([[makeQuery(id+"F3.imprint","INTERSECT",VERTEX,{"derivedFrom":[makeQuery(id+"F1.opExtrude","CAP_EDGE",EDGE,{"disambiguationData":[OSD([sQuery(id+"F0.wireOp",EDGE,"E2.bottom")])],"isStart":false}),subQ0]}),1.0]])],"derivedFrom":subQ0})])],"isStart":false});}
            var Q49;
            {var subQ0=sQuery(id+"F3.wireOp",EDGE,"E4.13.0.0");Q49=makeQuery(id+"F4.opExtrude","CAP_EDGE",EDGE,{"disambiguationData":[OSD([subQ0]),TDD([makeQuery(id+"F3.imprint","IMPRINT",EDGE,{"disambiguationData":[TD([[makeQuery(id+"F3.imprint","INTERSECT",VERTEX,{"derivedFrom":[makeQuery(id+"F1.opExtrude","CAP_EDGE",EDGE,{"disambiguationData":[OSD([sQuery(id+"F0.wireOp",EDGE,"E2.bottom")])],"isStart":false}),subQ0]}),1.0]])],"derivedFrom":subQ0})])],"isStart":false});}
            var Q50;
            {var subQ0=sQuery(id+"F3.wireOp",EDGE,"E4.12.0.1");Q50=makeQuery(id+"F4.opExtrude","CAP_EDGE",EDGE,{"disambiguationData":[OSD([subQ0]),TDD([makeQuery(id+"F3.imprint","IMPRINT",EDGE,{"disambiguationData":[TD([[makeQuery(id+"F3.imprint","INTERSECT",VERTEX,{"derivedFrom":[makeQuery(id+"F1.opExtrude","CAP_EDGE",EDGE,{"disambiguationData":[OSD([sQuery(id+"F0.wireOp",EDGE,"E2.bottom")])],"isStart":false}),subQ0]}),1.0]])],"derivedFrom":subQ0})])],"isStart":false});}
            var Q51;
            {var subQ0=sQuery(id+"F3.wireOp",EDGE,"E4.12.0.0");Q51=makeQuery(id+"F4.opExtrude","CAP_EDGE",EDGE,{"disambiguationData":[OSD([subQ0]),TDD([makeQuery(id+"F3.imprint","IMPRINT",EDGE,{"disambiguationData":[TD([[makeQuery(id+"F3.imprint","INTERSECT",VERTEX,{"derivedFrom":[makeQuery(id+"F1.opExtrude","CAP_EDGE",EDGE,{"disambiguationData":[OSD([sQuery(id+"F0.wireOp",EDGE,"E2.bottom")])],"isStart":false}),subQ0]}),1.0]])],"derivedFrom":subQ0})])],"isStart":false});}
            var Q52;
            {var subQ0=sQuery(id+"F3.wireOp",EDGE,"E4.11.0.1");Q52=makeQuery(id+"F4.opExtrude","CAP_EDGE",EDGE,{"disambiguationData":[OSD([subQ0]),TDD([makeQuery(id+"F3.imprint","IMPRINT",EDGE,{"disambiguationData":[TD([[makeQuery(id+"F3.imprint","INTERSECT",VERTEX,{"derivedFrom":[makeQuery(id+"F1.opExtrude","CAP_EDGE",EDGE,{"disambiguationData":[OSD([sQuery(id+"F0.wireOp",EDGE,"E2.bottom")])],"isStart":false}),subQ0]}),1.0]])],"derivedFrom":subQ0})])],"isStart":false});}
            var Q53;
            {var subQ0=sQuery(id+"F3.wireOp",EDGE,"E4.11.0.0");Q53=makeQuery(id+"F4.opExtrude","CAP_EDGE",EDGE,{"disambiguationData":[OSD([subQ0]),TDD([makeQuery(id+"F3.imprint","IMPRINT",EDGE,{"disambiguationData":[TD([[makeQuery(id+"F3.imprint","INTERSECT",VERTEX,{"derivedFrom":[makeQuery(id+"F1.opExtrude","CAP_EDGE",EDGE,{"disambiguationData":[OSD([sQuery(id+"F0.wireOp",EDGE,"E2.bottom")])],"isStart":false}),subQ0]}),1.0]])],"derivedFrom":subQ0})])],"isStart":false});}
            var Q54;
            {var subQ0=sQuery(id+"F3.wireOp",EDGE,"E4.10.0.1");Q54=makeQuery(id+"F4.opExtrude","CAP_EDGE",EDGE,{"disambiguationData":[OSD([subQ0]),TDD([makeQuery(id+"F3.imprint","IMPRINT",EDGE,{"disambiguationData":[TD([[makeQuery(id+"F3.imprint","INTERSECT",VERTEX,{"derivedFrom":[makeQuery(id+"F1.opExtrude","CAP_EDGE",EDGE,{"disambiguationData":[OSD([sQuery(id+"F0.wireOp",EDGE,"E2.bottom")])],"isStart":false}),subQ0]}),1.0]])],"derivedFrom":subQ0})])],"isStart":false});}
            var Q55;
            {var subQ0=sQuery(id+"F3.wireOp",EDGE,"E4.10.0.0");Q55=makeQuery(id+"F4.opExtrude","CAP_EDGE",EDGE,{"disambiguationData":[OSD([subQ0]),TDD([makeQuery(id+"F3.imprint","IMPRINT",EDGE,{"disambiguationData":[TD([[makeQuery(id+"F3.imprint","INTERSECT",VERTEX,{"derivedFrom":[makeQuery(id+"F1.opExtrude","CAP_EDGE",EDGE,{"disambiguationData":[OSD([sQuery(id+"F0.wireOp",EDGE,"E2.bottom")])],"isStart":false}),subQ0]}),1.0]])],"derivedFrom":subQ0})])],"isStart":false});}
            var Q56;
            {var subQ0=sQuery(id+"F3.wireOp",EDGE,"E4.9.0.1");Q56=makeQuery(id+"F4.opExtrude","CAP_EDGE",EDGE,{"disambiguationData":[OSD([subQ0]),TDD([makeQuery(id+"F3.imprint","IMPRINT",EDGE,{"disambiguationData":[TD([[makeQuery(id+"F3.imprint","INTERSECT",VERTEX,{"derivedFrom":[makeQuery(id+"F1.opExtrude","CAP_EDGE",EDGE,{"disambiguationData":[OSD([sQuery(id+"F0.wireOp",EDGE,"E2.bottom")])],"isStart":false}),subQ0]}),1.0]])],"derivedFrom":subQ0})])],"isStart":false});}
            var Q57;
            {var subQ0=sQuery(id+"F3.wireOp",EDGE,"E4.9.0.0");Q57=makeQuery(id+"F4.opExtrude","CAP_EDGE",EDGE,{"disambiguationData":[OSD([subQ0]),TDD([makeQuery(id+"F3.imprint","IMPRINT",EDGE,{"disambiguationData":[TD([[makeQuery(id+"F3.imprint","INTERSECT",VERTEX,{"derivedFrom":[makeQuery(id+"F1.opExtrude","CAP_EDGE",EDGE,{"disambiguationData":[OSD([sQuery(id+"F0.wireOp",EDGE,"E2.bottom")])],"isStart":false}),subQ0]}),1.0]])],"derivedFrom":subQ0})])],"isStart":false});}
            var Q58;
            {var subQ0=sQuery(id+"F3.wireOp",EDGE,"E4.8.0.1");Q58=makeQuery(id+"F4.opExtrude","CAP_EDGE",EDGE,{"disambiguationData":[OSD([subQ0]),TDD([makeQuery(id+"F3.imprint","IMPRINT",EDGE,{"disambiguationData":[TD([[makeQuery(id+"F3.imprint","INTERSECT",VERTEX,{"derivedFrom":[makeQuery(id+"F1.opExtrude","CAP_EDGE",EDGE,{"disambiguationData":[OSD([sQuery(id+"F0.wireOp",EDGE,"E2.bottom")])],"isStart":false}),subQ0]}),1.0]])],"derivedFrom":subQ0})])],"isStart":false});}
            var Q59;
            {var subQ0=sQuery(id+"F3.wireOp",EDGE,"E4.8.0.0");Q59=makeQuery(id+"F4.opExtrude","CAP_EDGE",EDGE,{"disambiguationData":[OSD([subQ0]),TDD([makeQuery(id+"F3.imprint","IMPRINT",EDGE,{"disambiguationData":[TD([[makeQuery(id+"F3.imprint","INTERSECT",VERTEX,{"derivedFrom":[makeQuery(id+"F1.opExtrude","CAP_EDGE",EDGE,{"disambiguationData":[OSD([sQuery(id+"F0.wireOp",EDGE,"E2.bottom")])],"isStart":false}),subQ0]}),1.0]])],"derivedFrom":subQ0})])],"isStart":false});}
            var Q60;
            {var subQ0=sQuery(id+"F3.wireOp",EDGE,"E4.7.0.1");Q60=makeQuery(id+"F4.opExtrude","CAP_EDGE",EDGE,{"disambiguationData":[OSD([subQ0]),TDD([makeQuery(id+"F3.imprint","IMPRINT",EDGE,{"disambiguationData":[TD([[makeQuery(id+"F3.imprint","INTERSECT",VERTEX,{"derivedFrom":[makeQuery(id+"F1.opExtrude","CAP_EDGE",EDGE,{"disambiguationData":[OSD([sQuery(id+"F0.wireOp",EDGE,"E2.bottom")])],"isStart":false}),subQ0]}),1.0]])],"derivedFrom":subQ0})])],"isStart":false});}
            var Q61;
            {var subQ0=sQuery(id+"F3.wireOp",EDGE,"E4.7.0.0");Q61=makeQuery(id+"F4.opExtrude","CAP_EDGE",EDGE,{"disambiguationData":[OSD([subQ0]),TDD([makeQuery(id+"F3.imprint","IMPRINT",EDGE,{"disambiguationData":[TD([[makeQuery(id+"F3.imprint","INTERSECT",VERTEX,{"derivedFrom":[makeQuery(id+"F1.opExtrude","CAP_EDGE",EDGE,{"disambiguationData":[OSD([sQuery(id+"F0.wireOp",EDGE,"E2.bottom")])],"isStart":false}),subQ0]}),1.0]])],"derivedFrom":subQ0})])],"isStart":false});}
            var Q62;
            {var subQ0=sQuery(id+"F3.wireOp",EDGE,"E4.6.0.1");Q62=makeQuery(id+"F4.opExtrude","CAP_EDGE",EDGE,{"disambiguationData":[OSD([subQ0]),TDD([makeQuery(id+"F3.imprint","IMPRINT",EDGE,{"disambiguationData":[TD([[makeQuery(id+"F3.imprint","INTERSECT",VERTEX,{"derivedFrom":[makeQuery(id+"F1.opExtrude","CAP_EDGE",EDGE,{"disambiguationData":[OSD([sQuery(id+"F0.wireOp",EDGE,"E2.bottom")])],"isStart":false}),subQ0]}),1.0]])],"derivedFrom":subQ0})])],"isStart":false});}
            var Q63;
            {var subQ0=sQuery(id+"F3.wireOp",EDGE,"E4.6.0.0");Q63=makeQuery(id+"F4.opExtrude","CAP_EDGE",EDGE,{"disambiguationData":[OSD([subQ0]),TDD([makeQuery(id+"F3.imprint","IMPRINT",EDGE,{"disambiguationData":[TD([[makeQuery(id+"F3.imprint","INTERSECT",VERTEX,{"derivedFrom":[makeQuery(id+"F1.opExtrude","CAP_EDGE",EDGE,{"disambiguationData":[OSD([sQuery(id+"F0.wireOp",EDGE,"E2.bottom")])],"isStart":false}),subQ0]}),1.0]])],"derivedFrom":subQ0})])],"isStart":false});}
            var Q64;
            {var subQ0=sQuery(id+"F3.wireOp",EDGE,"E4.5.0.1");Q64=makeQuery(id+"F4.opExtrude","CAP_EDGE",EDGE,{"disambiguationData":[OSD([subQ0]),TDD([makeQuery(id+"F3.imprint","IMPRINT",EDGE,{"disambiguationData":[TD([[makeQuery(id+"F3.imprint","INTERSECT",VERTEX,{"derivedFrom":[makeQuery(id+"F1.opExtrude","CAP_EDGE",EDGE,{"disambiguationData":[OSD([sQuery(id+"F0.wireOp",EDGE,"E2.bottom")])],"isStart":false}),subQ0]}),1.0]])],"derivedFrom":subQ0})])],"isStart":false});}
            var Q65;
            {var subQ0=sQuery(id+"F3.wireOp",EDGE,"E4.5.0.0");Q65=makeQuery(id+"F4.opExtrude","CAP_EDGE",EDGE,{"disambiguationData":[OSD([subQ0]),TDD([makeQuery(id+"F3.imprint","IMPRINT",EDGE,{"disambiguationData":[TD([[makeQuery(id+"F3.imprint","INTERSECT",VERTEX,{"derivedFrom":[makeQuery(id+"F1.opExtrude","CAP_EDGE",EDGE,{"disambiguationData":[OSD([sQuery(id+"F0.wireOp",EDGE,"E2.bottom")])],"isStart":false}),subQ0]}),1.0]])],"derivedFrom":subQ0})])],"isStart":false});}
            var Q66;
            {var subQ0=sQuery(id+"F3.wireOp",EDGE,"E4.4.0.1");Q66=makeQuery(id+"F4.opExtrude","CAP_EDGE",EDGE,{"disambiguationData":[OSD([subQ0]),TDD([makeQuery(id+"F3.imprint","IMPRINT",EDGE,{"disambiguationData":[TD([[makeQuery(id+"F3.imprint","INTERSECT",VERTEX,{"derivedFrom":[makeQuery(id+"F1.opExtrude","CAP_EDGE",EDGE,{"disambiguationData":[OSD([sQuery(id+"F0.wireOp",EDGE,"E2.bottom")])],"isStart":false}),subQ0]}),1.0]])],"derivedFrom":subQ0})])],"isStart":false});}
            var Q67;
            {var subQ0=sQuery(id+"F3.wireOp",EDGE,"E4.4.0.0");Q67=makeQuery(id+"F4.opExtrude","CAP_EDGE",EDGE,{"disambiguationData":[OSD([subQ0]),TDD([makeQuery(id+"F3.imprint","IMPRINT",EDGE,{"disambiguationData":[TD([[makeQuery(id+"F3.imprint","INTERSECT",VERTEX,{"derivedFrom":[makeQuery(id+"F1.opExtrude","CAP_EDGE",EDGE,{"disambiguationData":[OSD([sQuery(id+"F0.wireOp",EDGE,"E2.bottom")])],"isStart":false}),subQ0]}),1.0]])],"derivedFrom":subQ0})])],"isStart":false});}
            var Q68;
            {var subQ0=sQuery(id+"F3.wireOp",EDGE,"E4.3.0.1");Q68=makeQuery(id+"F4.opExtrude","CAP_EDGE",EDGE,{"disambiguationData":[OSD([subQ0]),TDD([makeQuery(id+"F3.imprint","IMPRINT",EDGE,{"disambiguationData":[TD([[makeQuery(id+"F3.imprint","INTERSECT",VERTEX,{"derivedFrom":[makeQuery(id+"F1.opExtrude","CAP_EDGE",EDGE,{"disambiguationData":[OSD([sQuery(id+"F0.wireOp",EDGE,"E2.bottom")])],"isStart":false}),subQ0]}),1.0]])],"derivedFrom":subQ0})])],"isStart":false});}
            var Q69;
            {var subQ0=sQuery(id+"F3.wireOp",EDGE,"E4.3.0.0");Q69=makeQuery(id+"F4.opExtrude","CAP_EDGE",EDGE,{"disambiguationData":[OSD([subQ0]),TDD([makeQuery(id+"F3.imprint","IMPRINT",EDGE,{"disambiguationData":[TD([[makeQuery(id+"F3.imprint","INTERSECT",VERTEX,{"derivedFrom":[makeQuery(id+"F1.opExtrude","CAP_EDGE",EDGE,{"disambiguationData":[OSD([sQuery(id+"F0.wireOp",EDGE,"E2.bottom")])],"isStart":false}),subQ0]}),1.0]])],"derivedFrom":subQ0})])],"isStart":false});}
            var Q70;
            {var subQ0=sQuery(id+"F3.wireOp",EDGE,"E4.2.0.1");Q70=makeQuery(id+"F4.opExtrude","CAP_EDGE",EDGE,{"disambiguationData":[OSD([subQ0]),TDD([makeQuery(id+"F3.imprint","IMPRINT",EDGE,{"disambiguationData":[TD([[makeQuery(id+"F3.imprint","INTERSECT",VERTEX,{"derivedFrom":[makeQuery(id+"F1.opExtrude","CAP_EDGE",EDGE,{"disambiguationData":[OSD([sQuery(id+"F0.wireOp",EDGE,"E2.bottom")])],"isStart":false}),subQ0]}),1.0]])],"derivedFrom":subQ0})])],"isStart":false});}
            var Q71;
            {var subQ0=sQuery(id+"F3.wireOp",EDGE,"E4.2.0.0");Q71=makeQuery(id+"F4.opExtrude","CAP_EDGE",EDGE,{"disambiguationData":[OSD([subQ0]),TDD([makeQuery(id+"F3.imprint","IMPRINT",EDGE,{"disambiguationData":[TD([[makeQuery(id+"F3.imprint","INTERSECT",VERTEX,{"derivedFrom":[makeQuery(id+"F1.opExtrude","CAP_EDGE",EDGE,{"disambiguationData":[OSD([sQuery(id+"F0.wireOp",EDGE,"E2.bottom")])],"isStart":false}),subQ0]}),1.0]])],"derivedFrom":subQ0})])],"isStart":false});}
            var Q72;
            {var subQ0=sQuery(id+"F3.wireOp",EDGE,"E4.1.0.1");Q72=makeQuery(id+"F4.opExtrude","CAP_EDGE",EDGE,{"disambiguationData":[OSD([subQ0]),TDD([makeQuery(id+"F3.imprint","IMPRINT",EDGE,{"disambiguationData":[TD([[makeQuery(id+"F3.imprint","INTERSECT",VERTEX,{"derivedFrom":[makeQuery(id+"F1.opExtrude","CAP_EDGE",EDGE,{"disambiguationData":[OSD([sQuery(id+"F0.wireOp",EDGE,"E2.bottom")])],"isStart":false}),subQ0]}),1.0]])],"derivedFrom":subQ0})])],"isStart":false});}
            var Q73;
            {var subQ0=sQuery(id+"F3.wireOp",EDGE,"E4.1.0.0");Q73=makeQuery(id+"F4.opExtrude","CAP_EDGE",EDGE,{"disambiguationData":[OSD([subQ0]),TDD([makeQuery(id+"F3.imprint","IMPRINT",EDGE,{"disambiguationData":[TD([[makeQuery(id+"F3.imprint","INTERSECT",VERTEX,{"derivedFrom":[makeQuery(id+"F1.opExtrude","CAP_EDGE",EDGE,{"disambiguationData":[OSD([sQuery(id+"F0.wireOp",EDGE,"E2.bottom")])],"isStart":false}),subQ0]}),1.0]])],"derivedFrom":subQ0})])],"isStart":false});}
            var Q74;
            {var subQ0=sQuery(id+"F3.wireOp",EDGE,"E3.right");Q74=makeQuery(id+"F4.opExtrude","CAP_EDGE",EDGE,{"disambiguationData":[OSD([subQ0]),TDD([makeQuery(id+"F3.imprint","IMPRINT",EDGE,{"disambiguationData":[TD([[makeQuery(id+"F3.imprint","INTERSECT",VERTEX,{"derivedFrom":[makeQuery(id+"F1.opExtrude","CAP_EDGE",EDGE,{"disambiguationData":[OSD([sQuery(id+"F0.wireOp",EDGE,"E2.bottom")])],"isStart":false}),subQ0]}),1.0]])],"derivedFrom":subQ0})])],"isStart":false});}
            var Q75;
            {var subQ0=sQuery(id+"F3.wireOp",EDGE,"E3.left");Q75=makeQuery(id+"F4.opExtrude","CAP_EDGE",EDGE,{"disambiguationData":[OSD([subQ0]),TDD([makeQuery(id+"F3.imprint","IMPRINT",EDGE,{"disambiguationData":[TD([[makeQuery(id+"F3.imprint","INTERSECT",VERTEX,{"derivedFrom":[sQuery(id+"F3.wireOp",EDGE,"E3.bottom"),subQ0]}),-1.0]])],"derivedFrom":subQ0})])],"isStart":false});}
            var Q76;
            {var subQ0=sQuery(id+"F3.wireOp",EDGE,"E3.right");Q76=makeQuery(id+"F4.opExtrude","CAP_EDGE",EDGE,{"disambiguationData":[OSD([subQ0]),TDD([makeQuery(id+"F3.imprint","IMPRINT",EDGE,{"disambiguationData":[TD([[makeQuery(id+"F3.imprint","INTERSECT",VERTEX,{"derivedFrom":[makeQuery(id+"F1.opExtrude","CAP_EDGE",EDGE,{"disambiguationData":[OSD([sQuery(id+"F0.wireOp",EDGE,"E2.top")])],"isStart":false}),subQ0]}),-1.0]])],"derivedFrom":subQ0})])],"isStart":false});}
            var Q77;
            {var subQ0=sQuery(id+"F3.wireOp",EDGE,"E3.left");Q77=makeQuery(id+"F4.opExtrude","CAP_EDGE",EDGE,{"disambiguationData":[OSD([subQ0]),TDD([makeQuery(id+"F3.imprint","IMPRINT",EDGE,{"disambiguationData":[TD([[makeQuery(id+"F3.imprint","INTERSECT",VERTEX,{"derivedFrom":[sQuery(id+"F3.wireOp",EDGE,"E3.top"),subQ0]}),1.0]])],"derivedFrom":subQ0})])],"isStart":false});}
            var Q78;
            {var subQ0=sQuery(id+"F3.wireOp",EDGE,"E4.1.0.1");Q78=makeQuery(id+"F4.opExtrude","CAP_EDGE",EDGE,{"disambiguationData":[OSD([subQ0]),TDD([makeQuery(id+"F3.imprint","IMPRINT",EDGE,{"disambiguationData":[TD([[makeQuery(id+"F3.imprint","INTERSECT",VERTEX,{"derivedFrom":[makeQuery(id+"F1.opExtrude","CAP_EDGE",EDGE,{"disambiguationData":[OSD([sQuery(id+"F0.wireOp",EDGE,"E2.top")])],"isStart":false}),subQ0]}),-1.0]])],"derivedFrom":subQ0})])],"isStart":false});}
            var Q79;
            {var subQ0=sQuery(id+"F3.wireOp",EDGE,"E4.1.0.0");Q79=makeQuery(id+"F4.opExtrude","CAP_EDGE",EDGE,{"disambiguationData":[OSD([subQ0]),TDD([makeQuery(id+"F3.imprint","IMPRINT",EDGE,{"disambiguationData":[TD([[makeQuery(id+"F3.imprint","INTERSECT",VERTEX,{"derivedFrom":[makeQuery(id+"F1.opExtrude","CAP_EDGE",EDGE,{"disambiguationData":[OSD([sQuery(id+"F0.wireOp",EDGE,"E2.top")])],"isStart":false}),subQ0]}),-1.0]])],"derivedFrom":subQ0})])],"isStart":false});}
            var Q80;
            {var subQ0=sQuery(id+"F3.wireOp",EDGE,"E4.2.0.0");Q80=makeQuery(id+"F4.opExtrude","CAP_EDGE",EDGE,{"disambiguationData":[OSD([subQ0]),TDD([makeQuery(id+"F3.imprint","IMPRINT",EDGE,{"disambiguationData":[TD([[makeQuery(id+"F3.imprint","INTERSECT",VERTEX,{"derivedFrom":[makeQuery(id+"F1.opExtrude","CAP_EDGE",EDGE,{"disambiguationData":[OSD([sQuery(id+"F0.wireOp",EDGE,"E2.top")])],"isStart":false}),subQ0]}),-1.0]])],"derivedFrom":subQ0})])],"isStart":false});}
            var Q81;
            {var subQ0=sQuery(id+"F3.wireOp",EDGE,"E4.2.0.1");Q81=makeQuery(id+"F4.opExtrude","CAP_EDGE",EDGE,{"disambiguationData":[OSD([subQ0]),TDD([makeQuery(id+"F3.imprint","IMPRINT",EDGE,{"disambiguationData":[TD([[makeQuery(id+"F3.imprint","INTERSECT",VERTEX,{"derivedFrom":[makeQuery(id+"F1.opExtrude","CAP_EDGE",EDGE,{"disambiguationData":[OSD([sQuery(id+"F0.wireOp",EDGE,"E2.top")])],"isStart":false}),subQ0]}),-1.0]])],"derivedFrom":subQ0})])],"isStart":false});}
            var Q82;
            {var subQ0=sQuery(id+"F3.wireOp",EDGE,"E4.3.0.0");Q82=makeQuery(id+"F4.opExtrude","CAP_EDGE",EDGE,{"disambiguationData":[OSD([subQ0]),TDD([makeQuery(id+"F3.imprint","IMPRINT",EDGE,{"disambiguationData":[TD([[makeQuery(id+"F3.imprint","INTERSECT",VERTEX,{"derivedFrom":[makeQuery(id+"F1.opExtrude","CAP_EDGE",EDGE,{"disambiguationData":[OSD([sQuery(id+"F0.wireOp",EDGE,"E2.top")])],"isStart":false}),subQ0]}),-1.0]])],"derivedFrom":subQ0})])],"isStart":false});}
            var Q83;
            {var subQ0=sQuery(id+"F3.wireOp",EDGE,"E4.3.0.1");Q83=makeQuery(id+"F4.opExtrude","CAP_EDGE",EDGE,{"disambiguationData":[OSD([subQ0]),TDD([makeQuery(id+"F3.imprint","IMPRINT",EDGE,{"disambiguationData":[TD([[makeQuery(id+"F3.imprint","INTERSECT",VERTEX,{"derivedFrom":[makeQuery(id+"F1.opExtrude","CAP_EDGE",EDGE,{"disambiguationData":[OSD([sQuery(id+"F0.wireOp",EDGE,"E2.top")])],"isStart":false}),subQ0]}),-1.0]])],"derivedFrom":subQ0})])],"isStart":false});}
            var Q84;
            {var subQ0=sQuery(id+"F3.wireOp",EDGE,"E4.4.0.0");Q84=makeQuery(id+"F4.opExtrude","CAP_EDGE",EDGE,{"disambiguationData":[OSD([subQ0]),TDD([makeQuery(id+"F3.imprint","IMPRINT",EDGE,{"disambiguationData":[TD([[makeQuery(id+"F3.imprint","INTERSECT",VERTEX,{"derivedFrom":[makeQuery(id+"F1.opExtrude","CAP_EDGE",EDGE,{"disambiguationData":[OSD([sQuery(id+"F0.wireOp",EDGE,"E2.top")])],"isStart":false}),subQ0]}),-1.0]])],"derivedFrom":subQ0})])],"isStart":false});}
            var Q85;
            {var subQ0=sQuery(id+"F3.wireOp",EDGE,"E4.4.0.1");Q85=makeQuery(id+"F4.opExtrude","CAP_EDGE",EDGE,{"disambiguationData":[OSD([subQ0]),TDD([makeQuery(id+"F3.imprint","IMPRINT",EDGE,{"disambiguationData":[TD([[makeQuery(id+"F3.imprint","INTERSECT",VERTEX,{"derivedFrom":[makeQuery(id+"F1.opExtrude","CAP_EDGE",EDGE,{"disambiguationData":[OSD([sQuery(id+"F0.wireOp",EDGE,"E2.top")])],"isStart":false}),subQ0]}),-1.0]])],"derivedFrom":subQ0})])],"isStart":false});}
            var Q86;
            {var subQ0=sQuery(id+"F3.wireOp",EDGE,"E4.5.0.0");Q86=makeQuery(id+"F4.opExtrude","CAP_EDGE",EDGE,{"disambiguationData":[OSD([subQ0]),TDD([makeQuery(id+"F3.imprint","IMPRINT",EDGE,{"disambiguationData":[TD([[makeQuery(id+"F3.imprint","INTERSECT",VERTEX,{"derivedFrom":[makeQuery(id+"F1.opExtrude","CAP_EDGE",EDGE,{"disambiguationData":[OSD([sQuery(id+"F0.wireOp",EDGE,"E2.top")])],"isStart":false}),subQ0]}),-1.0]])],"derivedFrom":subQ0})])],"isStart":false});}
            var Q87;
            {var subQ0=sQuery(id+"F3.wireOp",EDGE,"E4.5.0.1");Q87=makeQuery(id+"F4.opExtrude","CAP_EDGE",EDGE,{"disambiguationData":[OSD([subQ0]),TDD([makeQuery(id+"F3.imprint","IMPRINT",EDGE,{"disambiguationData":[TD([[makeQuery(id+"F3.imprint","INTERSECT",VERTEX,{"derivedFrom":[makeQuery(id+"F1.opExtrude","CAP_EDGE",EDGE,{"disambiguationData":[OSD([sQuery(id+"F0.wireOp",EDGE,"E2.top")])],"isStart":false}),subQ0]}),-1.0]])],"derivedFrom":subQ0})])],"isStart":false});}
            var Q88;
            {var subQ0=sQuery(id+"F3.wireOp",EDGE,"E4.6.0.1");Q88=makeQuery(id+"F4.opExtrude","CAP_EDGE",EDGE,{"disambiguationData":[OSD([subQ0]),TDD([makeQuery(id+"F3.imprint","IMPRINT",EDGE,{"disambiguationData":[TD([[makeQuery(id+"F3.imprint","INTERSECT",VERTEX,{"derivedFrom":[makeQuery(id+"F1.opExtrude","CAP_EDGE",EDGE,{"disambiguationData":[OSD([sQuery(id+"F0.wireOp",EDGE,"E2.top")])],"isStart":false}),subQ0]}),-1.0]])],"derivedFrom":subQ0})])],"isStart":false});}
            var Q89;
            {var subQ0=sQuery(id+"F3.wireOp",EDGE,"E4.6.0.0");Q89=makeQuery(id+"F4.opExtrude","CAP_EDGE",EDGE,{"disambiguationData":[OSD([subQ0]),TDD([makeQuery(id+"F3.imprint","IMPRINT",EDGE,{"disambiguationData":[TD([[makeQuery(id+"F3.imprint","INTERSECT",VERTEX,{"derivedFrom":[makeQuery(id+"F1.opExtrude","CAP_EDGE",EDGE,{"disambiguationData":[OSD([sQuery(id+"F0.wireOp",EDGE,"E2.top")])],"isStart":false}),subQ0]}),-1.0]])],"derivedFrom":subQ0})])],"isStart":false});}
            var Q90;
            {var subQ0=sQuery(id+"F3.wireOp",EDGE,"E4.7.0.1");Q90=makeQuery(id+"F4.opExtrude","CAP_EDGE",EDGE,{"disambiguationData":[OSD([subQ0]),TDD([makeQuery(id+"F3.imprint","IMPRINT",EDGE,{"disambiguationData":[TD([[makeQuery(id+"F3.imprint","INTERSECT",VERTEX,{"derivedFrom":[makeQuery(id+"F1.opExtrude","CAP_EDGE",EDGE,{"disambiguationData":[OSD([sQuery(id+"F0.wireOp",EDGE,"E2.top")])],"isStart":false}),subQ0]}),-1.0]])],"derivedFrom":subQ0})])],"isStart":false});}
            var Q91;
            {var subQ0=sQuery(id+"F3.wireOp",EDGE,"E4.7.0.0");Q91=makeQuery(id+"F4.opExtrude","CAP_EDGE",EDGE,{"disambiguationData":[OSD([subQ0]),TDD([makeQuery(id+"F3.imprint","IMPRINT",EDGE,{"disambiguationData":[TD([[makeQuery(id+"F3.imprint","INTERSECT",VERTEX,{"derivedFrom":[makeQuery(id+"F1.opExtrude","CAP_EDGE",EDGE,{"disambiguationData":[OSD([sQuery(id+"F0.wireOp",EDGE,"E2.top")])],"isStart":false}),subQ0]}),-1.0]])],"derivedFrom":subQ0})])],"isStart":false});}
            var Q92;
            {var subQ0=sQuery(id+"F3.wireOp",EDGE,"E4.8.0.1");Q92=makeQuery(id+"F4.opExtrude","CAP_EDGE",EDGE,{"disambiguationData":[OSD([subQ0]),TDD([makeQuery(id+"F3.imprint","IMPRINT",EDGE,{"disambiguationData":[TD([[makeQuery(id+"F3.imprint","INTERSECT",VERTEX,{"derivedFrom":[makeQuery(id+"F1.opExtrude","CAP_EDGE",EDGE,{"disambiguationData":[OSD([sQuery(id+"F0.wireOp",EDGE,"E2.top")])],"isStart":false}),subQ0]}),-1.0]])],"derivedFrom":subQ0})])],"isStart":false});}
            var Q93;
            {var subQ0=sQuery(id+"F3.wireOp",EDGE,"E4.8.0.0");Q93=makeQuery(id+"F4.opExtrude","CAP_EDGE",EDGE,{"disambiguationData":[OSD([subQ0]),TDD([makeQuery(id+"F3.imprint","IMPRINT",EDGE,{"disambiguationData":[TD([[makeQuery(id+"F3.imprint","INTERSECT",VERTEX,{"derivedFrom":[makeQuery(id+"F1.opExtrude","CAP_EDGE",EDGE,{"disambiguationData":[OSD([sQuery(id+"F0.wireOp",EDGE,"E2.top")])],"isStart":false}),subQ0]}),-1.0]])],"derivedFrom":subQ0})])],"isStart":false});}
            var Q94;
            {var subQ0=sQuery(id+"F3.wireOp",EDGE,"E4.9.0.1");Q94=makeQuery(id+"F4.opExtrude","CAP_EDGE",EDGE,{"disambiguationData":[OSD([subQ0]),TDD([makeQuery(id+"F3.imprint","IMPRINT",EDGE,{"disambiguationData":[TD([[makeQuery(id+"F3.imprint","INTERSECT",VERTEX,{"derivedFrom":[makeQuery(id+"F1.opExtrude","CAP_EDGE",EDGE,{"disambiguationData":[OSD([sQuery(id+"F0.wireOp",EDGE,"E2.top")])],"isStart":false}),subQ0]}),-1.0]])],"derivedFrom":subQ0})])],"isStart":false});}
            var Q95;
            {var subQ0=sQuery(id+"F3.wireOp",EDGE,"E4.9.0.0");Q95=makeQuery(id+"F4.opExtrude","CAP_EDGE",EDGE,{"disambiguationData":[OSD([subQ0]),TDD([makeQuery(id+"F3.imprint","IMPRINT",EDGE,{"disambiguationData":[TD([[makeQuery(id+"F3.imprint","INTERSECT",VERTEX,{"derivedFrom":[makeQuery(id+"F1.opExtrude","CAP_EDGE",EDGE,{"disambiguationData":[OSD([sQuery(id+"F0.wireOp",EDGE,"E2.top")])],"isStart":false}),subQ0]}),-1.0]])],"derivedFrom":subQ0})])],"isStart":false});}
            var Q96;
            {var subQ0=sQuery(id+"F3.wireOp",EDGE,"E4.10.0.0");Q96=makeQuery(id+"F4.opExtrude","CAP_EDGE",EDGE,{"disambiguationData":[OSD([subQ0]),TDD([makeQuery(id+"F3.imprint","IMPRINT",EDGE,{"disambiguationData":[TD([[makeQuery(id+"F3.imprint","INTERSECT",VERTEX,{"derivedFrom":[makeQuery(id+"F1.opExtrude","CAP_EDGE",EDGE,{"disambiguationData":[OSD([sQuery(id+"F0.wireOp",EDGE,"E2.top")])],"isStart":false}),subQ0]}),-1.0]])],"derivedFrom":subQ0})])],"isStart":false});}
            var Q97;
            {var subQ0=sQuery(id+"F3.wireOp",EDGE,"E4.10.0.1");Q97=makeQuery(id+"F4.opExtrude","CAP_EDGE",EDGE,{"disambiguationData":[OSD([subQ0]),TDD([makeQuery(id+"F3.imprint","IMPRINT",EDGE,{"disambiguationData":[TD([[makeQuery(id+"F3.imprint","INTERSECT",VERTEX,{"derivedFrom":[makeQuery(id+"F1.opExtrude","CAP_EDGE",EDGE,{"disambiguationData":[OSD([sQuery(id+"F0.wireOp",EDGE,"E2.top")])],"isStart":false}),subQ0]}),-1.0]])],"derivedFrom":subQ0})])],"isStart":false});}
            var Q98;
            {var subQ0=sQuery(id+"F3.wireOp",EDGE,"E4.11.0.0");Q98=makeQuery(id+"F4.opExtrude","CAP_EDGE",EDGE,{"disambiguationData":[OSD([subQ0]),TDD([makeQuery(id+"F3.imprint","IMPRINT",EDGE,{"disambiguationData":[TD([[makeQuery(id+"F3.imprint","INTERSECT",VERTEX,{"derivedFrom":[makeQuery(id+"F1.opExtrude","CAP_EDGE",EDGE,{"disambiguationData":[OSD([sQuery(id+"F0.wireOp",EDGE,"E2.top")])],"isStart":false}),subQ0]}),-1.0]])],"derivedFrom":subQ0})])],"isStart":false});}
            var Q99;
            {var subQ0=sQuery(id+"F3.wireOp",EDGE,"E4.11.0.1");Q99=makeQuery(id+"F4.opExtrude","CAP_EDGE",EDGE,{"disambiguationData":[OSD([subQ0]),TDD([makeQuery(id+"F3.imprint","IMPRINT",EDGE,{"disambiguationData":[TD([[makeQuery(id+"F3.imprint","INTERSECT",VERTEX,{"derivedFrom":[makeQuery(id+"F1.opExtrude","CAP_EDGE",EDGE,{"disambiguationData":[OSD([sQuery(id+"F0.wireOp",EDGE,"E2.top")])],"isStart":false}),subQ0]}),-1.0]])],"derivedFrom":subQ0})])],"isStart":false});}
            var Q100;
            {var subQ0=sQuery(id+"F3.wireOp",EDGE,"E4.12.0.0");Q100=makeQuery(id+"F4.opExtrude","CAP_EDGE",EDGE,{"disambiguationData":[OSD([subQ0]),TDD([makeQuery(id+"F3.imprint","IMPRINT",EDGE,{"disambiguationData":[TD([[makeQuery(id+"F3.imprint","INTERSECT",VERTEX,{"derivedFrom":[makeQuery(id+"F1.opExtrude","CAP_EDGE",EDGE,{"disambiguationData":[OSD([sQuery(id+"F0.wireOp",EDGE,"E2.top")])],"isStart":false}),subQ0]}),-1.0]])],"derivedFrom":subQ0})])],"isStart":false});}
            var Q101;
            {var subQ0=sQuery(id+"F3.wireOp",EDGE,"E4.12.0.1");Q101=makeQuery(id+"F4.opExtrude","CAP_EDGE",EDGE,{"disambiguationData":[OSD([subQ0]),TDD([makeQuery(id+"F3.imprint","IMPRINT",EDGE,{"disambiguationData":[TD([[makeQuery(id+"F3.imprint","INTERSECT",VERTEX,{"derivedFrom":[makeQuery(id+"F1.opExtrude","CAP_EDGE",EDGE,{"disambiguationData":[OSD([sQuery(id+"F0.wireOp",EDGE,"E2.top")])],"isStart":false}),subQ0]}),-1.0]])],"derivedFrom":subQ0})])],"isStart":false});}
            var Q102;
            {var subQ0=sQuery(id+"F3.wireOp",EDGE,"E4.13.0.0");Q102=makeQuery(id+"F4.opExtrude","CAP_EDGE",EDGE,{"disambiguationData":[OSD([subQ0]),TDD([makeQuery(id+"F3.imprint","IMPRINT",EDGE,{"disambiguationData":[TD([[makeQuery(id+"F3.imprint","INTERSECT",VERTEX,{"derivedFrom":[makeQuery(id+"F1.opExtrude","CAP_EDGE",EDGE,{"disambiguationData":[OSD([sQuery(id+"F0.wireOp",EDGE,"E2.top")])],"isStart":false}),subQ0]}),-1.0]])],"derivedFrom":subQ0})])],"isStart":false});}
            var Q103;
            {var subQ0=sQuery(id+"F3.wireOp",EDGE,"E4.13.0.1");Q103=makeQuery(id+"F4.opExtrude","CAP_EDGE",EDGE,{"disambiguationData":[OSD([subQ0]),TDD([makeQuery(id+"F3.imprint","IMPRINT",EDGE,{"disambiguationData":[TD([[makeQuery(id+"F3.imprint","INTERSECT",VERTEX,{"derivedFrom":[makeQuery(id+"F1.opExtrude","CAP_EDGE",EDGE,{"disambiguationData":[OSD([sQuery(id+"F0.wireOp",EDGE,"E2.top")])],"isStart":false}),subQ0]}),-1.0]])],"derivedFrom":subQ0})])],"isStart":false});}
            var Q104;
            {var subQ0=sQuery(id+"F3.wireOp",EDGE,"E4.14.0.0");Q104=makeQuery(id+"F4.opExtrude","CAP_EDGE",EDGE,{"disambiguationData":[OSD([subQ0]),TDD([makeQuery(id+"F3.imprint","IMPRINT",EDGE,{"disambiguationData":[TD([[makeQuery(id+"F3.imprint","INTERSECT",VERTEX,{"derivedFrom":[makeQuery(id+"F1.opExtrude","CAP_EDGE",EDGE,{"disambiguationData":[OSD([sQuery(id+"F0.wireOp",EDGE,"E2.top")])],"isStart":false}),subQ0]}),-1.0]])],"derivedFrom":subQ0})])],"isStart":false});}
            var Q105;
            {var subQ0=sQuery(id+"F3.wireOp",EDGE,"E4.14.0.1");Q105=makeQuery(id+"F4.opExtrude","CAP_EDGE",EDGE,{"disambiguationData":[OSD([subQ0]),TDD([makeQuery(id+"F3.imprint","IMPRINT",EDGE,{"disambiguationData":[TD([[makeQuery(id+"F3.imprint","INTERSECT",VERTEX,{"derivedFrom":[makeQuery(id+"F1.opExtrude","CAP_EDGE",EDGE,{"disambiguationData":[OSD([sQuery(id+"F0.wireOp",EDGE,"E2.top")])],"isStart":false}),subQ0]}),-1.0]])],"derivedFrom":subQ0})])],"isStart":false});}
            var Q106;
            {var subQ0=sQuery(id+"F3.wireOp",EDGE,"E4.15.0.0");Q106=makeQuery(id+"F4.opExtrude","CAP_EDGE",EDGE,{"disambiguationData":[OSD([subQ0]),TDD([makeQuery(id+"F3.imprint","IMPRINT",EDGE,{"disambiguationData":[TD([[makeQuery(id+"F3.imprint","INTERSECT",VERTEX,{"derivedFrom":[makeQuery(id+"F1.opExtrude","CAP_EDGE",EDGE,{"disambiguationData":[OSD([sQuery(id+"F0.wireOp",EDGE,"E2.top")])],"isStart":false}),subQ0]}),-1.0]])],"derivedFrom":subQ0})])],"isStart":false});}
            var Q107;
            {var subQ0=sQuery(id+"F3.wireOp",EDGE,"E4.15.0.1");Q107=makeQuery(id+"F4.opExtrude","CAP_EDGE",EDGE,{"disambiguationData":[OSD([subQ0]),TDD([makeQuery(id+"F3.imprint","IMPRINT",EDGE,{"disambiguationData":[TD([[makeQuery(id+"F3.imprint","INTERSECT",VERTEX,{"derivedFrom":[makeQuery(id+"F1.opExtrude","CAP_EDGE",EDGE,{"disambiguationData":[OSD([sQuery(id+"F0.wireOp",EDGE,"E2.top")])],"isStart":false}),subQ0]}),-1.0]])],"derivedFrom":subQ0})])],"isStart":false});}
            var Q108;
            {var subQ0=sQuery(id+"F3.wireOp",EDGE,"E4.16.0.0");Q108=makeQuery(id+"F4.opExtrude","CAP_EDGE",EDGE,{"disambiguationData":[OSD([subQ0]),TDD([makeQuery(id+"F3.imprint","IMPRINT",EDGE,{"disambiguationData":[TD([[makeQuery(id+"F3.imprint","INTERSECT",VERTEX,{"derivedFrom":[makeQuery(id+"F1.opExtrude","CAP_EDGE",EDGE,{"disambiguationData":[OSD([sQuery(id+"F0.wireOp",EDGE,"E2.top")])],"isStart":false}),subQ0]}),-1.0]])],"derivedFrom":subQ0})])],"isStart":false});}
            var Q109;
            {var subQ0=sQuery(id+"F3.wireOp",EDGE,"E4.16.0.1");Q109=makeQuery(id+"F4.opExtrude","CAP_EDGE",EDGE,{"disambiguationData":[OSD([subQ0]),TDD([makeQuery(id+"F3.imprint","IMPRINT",EDGE,{"disambiguationData":[TD([[makeQuery(id+"F3.imprint","INTERSECT",VERTEX,{"derivedFrom":[makeQuery(id+"F1.opExtrude","CAP_EDGE",EDGE,{"disambiguationData":[OSD([sQuery(id+"F0.wireOp",EDGE,"E2.top")])],"isStart":false}),subQ0]}),-1.0]])],"derivedFrom":subQ0})])],"isStart":false});}
            var Q110;
            {var subQ0=sQuery(id+"F3.wireOp",EDGE,"E4.17.0.0");Q110=makeQuery(id+"F4.opExtrude","CAP_EDGE",EDGE,{"disambiguationData":[OSD([subQ0]),TDD([makeQuery(id+"F3.imprint","IMPRINT",EDGE,{"disambiguationData":[TD([[makeQuery(id+"F3.imprint","INTERSECT",VERTEX,{"derivedFrom":[makeQuery(id+"F1.opExtrude","CAP_EDGE",EDGE,{"disambiguationData":[OSD([sQuery(id+"F0.wireOp",EDGE,"E2.top")])],"isStart":false}),subQ0]}),-1.0]])],"derivedFrom":subQ0})])],"isStart":false});}
            var Q111;
            {var subQ0=sQuery(id+"F3.wireOp",EDGE,"E4.17.0.1");Q111=makeQuery(id+"F4.opExtrude","CAP_EDGE",EDGE,{"disambiguationData":[OSD([subQ0]),TDD([makeQuery(id+"F3.imprint","IMPRINT",EDGE,{"disambiguationData":[TD([[makeQuery(id+"F3.imprint","INTERSECT",VERTEX,{"derivedFrom":[makeQuery(id+"F1.opExtrude","CAP_EDGE",EDGE,{"disambiguationData":[OSD([sQuery(id+"F0.wireOp",EDGE,"E2.top")])],"isStart":false}),subQ0]}),-1.0]])],"derivedFrom":subQ0})])],"isStart":false});}
            var Q112;
            {var subQ0=sQuery(id+"F3.wireOp",EDGE,"E4.18.0.0");Q112=makeQuery(id+"F4.opExtrude","CAP_EDGE",EDGE,{"disambiguationData":[OSD([subQ0]),TDD([makeQuery(id+"F3.imprint","IMPRINT",EDGE,{"disambiguationData":[TD([[makeQuery(id+"F3.imprint","INTERSECT",VERTEX,{"derivedFrom":[makeQuery(id+"F1.opExtrude","CAP_EDGE",EDGE,{"disambiguationData":[OSD([sQuery(id+"F0.wireOp",EDGE,"E2.top")])],"isStart":false}),subQ0]}),-1.0]])],"derivedFrom":subQ0})])],"isStart":false});}
            var Q113;
            {var subQ0=sQuery(id+"F3.wireOp",EDGE,"E4.18.0.1");Q113=makeQuery(id+"F4.opExtrude","CAP_EDGE",EDGE,{"disambiguationData":[OSD([subQ0]),TDD([makeQuery(id+"F3.imprint","IMPRINT",EDGE,{"disambiguationData":[TD([[makeQuery(id+"F3.imprint","INTERSECT",VERTEX,{"derivedFrom":[makeQuery(id+"F1.opExtrude","CAP_EDGE",EDGE,{"disambiguationData":[OSD([sQuery(id+"F0.wireOp",EDGE,"E2.top")])],"isStart":false}),subQ0]}),-1.0]])],"derivedFrom":subQ0})])],"isStart":false});}
            var Q114;
            {var subQ0=sQuery(id+"F3.wireOp",EDGE,"E4.19.0.0");Q114=makeQuery(id+"F4.opExtrude","CAP_EDGE",EDGE,{"disambiguationData":[OSD([subQ0]),TDD([makeQuery(id+"F3.imprint","IMPRINT",EDGE,{"disambiguationData":[TD([[makeQuery(id+"F3.imprint","INTERSECT",VERTEX,{"derivedFrom":[makeQuery(id+"F1.opExtrude","CAP_EDGE",EDGE,{"disambiguationData":[OSD([sQuery(id+"F0.wireOp",EDGE,"E2.top")])],"isStart":false}),subQ0]}),-1.0]])],"derivedFrom":subQ0})])],"isStart":false});}
            var Q115;
            {var subQ0=sQuery(id+"F3.wireOp",EDGE,"E4.19.0.1");Q115=makeQuery(id+"F4.opExtrude","CAP_EDGE",EDGE,{"disambiguationData":[OSD([subQ0]),TDD([makeQuery(id+"F3.imprint","IMPRINT",EDGE,{"disambiguationData":[TD([[makeQuery(id+"F3.imprint","INTERSECT",VERTEX,{"derivedFrom":[makeQuery(id+"F1.opExtrude","CAP_EDGE",EDGE,{"disambiguationData":[OSD([sQuery(id+"F0.wireOp",EDGE,"E2.top")])],"isStart":false}),subQ0]}),-1.0]])],"derivedFrom":subQ0})])],"isStart":false});}
            var Q116;
            {var subQ0=sQuery(id+"F3.wireOp",EDGE,"E4.20.0.0");Q116=makeQuery(id+"F4.opExtrude","CAP_EDGE",EDGE,{"disambiguationData":[OSD([subQ0]),TDD([makeQuery(id+"F3.imprint","IMPRINT",EDGE,{"disambiguationData":[TD([[makeQuery(id+"F3.imprint","INTERSECT",VERTEX,{"derivedFrom":[makeQuery(id+"F1.opExtrude","CAP_EDGE",EDGE,{"disambiguationData":[OSD([sQuery(id+"F0.wireOp",EDGE,"E2.top")])],"isStart":false}),subQ0]}),-1.0]])],"derivedFrom":subQ0})])],"isStart":false});}
            var Q117;
            {var subQ0=sQuery(id+"F3.wireOp",EDGE,"E4.20.0.1");Q117=makeQuery(id+"F4.opExtrude","CAP_EDGE",EDGE,{"disambiguationData":[OSD([subQ0]),TDD([makeQuery(id+"F3.imprint","IMPRINT",EDGE,{"disambiguationData":[TD([[makeQuery(id+"F3.imprint","INTERSECT",VERTEX,{"derivedFrom":[makeQuery(id+"F1.opExtrude","CAP_EDGE",EDGE,{"disambiguationData":[OSD([sQuery(id+"F0.wireOp",EDGE,"E2.top")])],"isStart":false}),subQ0]}),-1.0]])],"derivedFrom":subQ0})])],"isStart":false});}
            var Q118;
            {var subQ0=sQuery(id+"F3.wireOp",EDGE,"E4.21.0.0");Q118=makeQuery(id+"F4.opExtrude","CAP_EDGE",EDGE,{"disambiguationData":[OSD([subQ0]),TDD([makeQuery(id+"F3.imprint","IMPRINT",EDGE,{"disambiguationData":[TD([[makeQuery(id+"F3.imprint","INTERSECT",VERTEX,{"derivedFrom":[makeQuery(id+"F1.opExtrude","CAP_EDGE",EDGE,{"disambiguationData":[OSD([sQuery(id+"F0.wireOp",EDGE,"E2.top")])],"isStart":false}),subQ0]}),-1.0]])],"derivedFrom":subQ0})])],"isStart":false});}
            var Q119;
            {var subQ0=sQuery(id+"F3.wireOp",EDGE,"E4.21.0.1");Q119=makeQuery(id+"F4.opExtrude","CAP_EDGE",EDGE,{"disambiguationData":[OSD([subQ0]),TDD([makeQuery(id+"F3.imprint","IMPRINT",EDGE,{"disambiguationData":[TD([[makeQuery(id+"F3.imprint","INTERSECT",VERTEX,{"derivedFrom":[makeQuery(id+"F1.opExtrude","CAP_EDGE",EDGE,{"disambiguationData":[OSD([sQuery(id+"F0.wireOp",EDGE,"E2.top")])],"isStart":false}),subQ0]}),-1.0]])],"derivedFrom":subQ0})])],"isStart":false});}
            var Q120;
            {var subQ0=sQuery(id+"F3.wireOp",EDGE,"E4.22.0.0");Q120=makeQuery(id+"F4.opExtrude","CAP_EDGE",EDGE,{"disambiguationData":[OSD([subQ0]),TDD([makeQuery(id+"F3.imprint","IMPRINT",EDGE,{"disambiguationData":[TD([[makeQuery(id+"F3.imprint","INTERSECT",VERTEX,{"derivedFrom":[makeQuery(id+"F1.opExtrude","CAP_EDGE",EDGE,{"disambiguationData":[OSD([sQuery(id+"F0.wireOp",EDGE,"E2.top")])],"isStart":false}),subQ0]}),-1.0]])],"derivedFrom":subQ0})])],"isStart":false});}
            var Q121;
            {var subQ0=sQuery(id+"F3.wireOp",EDGE,"E4.22.0.1");Q121=makeQuery(id+"F4.opExtrude","CAP_EDGE",EDGE,{"disambiguationData":[OSD([subQ0]),TDD([makeQuery(id+"F3.imprint","IMPRINT",EDGE,{"disambiguationData":[TD([[makeQuery(id+"F3.imprint","INTERSECT",VERTEX,{"derivedFrom":[makeQuery(id+"F1.opExtrude","CAP_EDGE",EDGE,{"disambiguationData":[OSD([sQuery(id+"F0.wireOp",EDGE,"E2.top")])],"isStart":false}),subQ0]}),-1.0]])],"derivedFrom":subQ0})])],"isStart":false});}
            var Q122;
            {var subQ0=sQuery(id+"F3.wireOp",EDGE,"E4.23.0.0");Q122=makeQuery(id+"F4.opExtrude","CAP_EDGE",EDGE,{"disambiguationData":[OSD([subQ0]),TDD([makeQuery(id+"F3.imprint","IMPRINT",EDGE,{"disambiguationData":[TD([[makeQuery(id+"F3.imprint","INTERSECT",VERTEX,{"derivedFrom":[makeQuery(id+"F1.opExtrude","CAP_EDGE",EDGE,{"disambiguationData":[OSD([sQuery(id+"F0.wireOp",EDGE,"E2.top")])],"isStart":false}),subQ0]}),-1.0]])],"derivedFrom":subQ0})])],"isStart":false});}
            var Q123;
            {var subQ0=sQuery(id+"F3.wireOp",EDGE,"E4.23.0.1");Q123=makeQuery(id+"F4.opExtrude","CAP_EDGE",EDGE,{"disambiguationData":[OSD([subQ0]),TDD([makeQuery(id+"F3.imprint","IMPRINT",EDGE,{"disambiguationData":[TD([[makeQuery(id+"F3.imprint","INTERSECT",VERTEX,{"derivedFrom":[makeQuery(id+"F1.opExtrude","CAP_EDGE",EDGE,{"disambiguationData":[OSD([sQuery(id+"F0.wireOp",EDGE,"E2.top")])],"isStart":false}),subQ0]}),-1.0]])],"derivedFrom":subQ0})])],"isStart":false});}
            var Q124;
            {var subQ0=sQuery(id+"F3.wireOp",EDGE,"E4.24.0.0");Q124=makeQuery(id+"F4.opExtrude","CAP_EDGE",EDGE,{"disambiguationData":[OSD([subQ0]),TDD([makeQuery(id+"F3.imprint","IMPRINT",EDGE,{"disambiguationData":[TD([[makeQuery(id+"F3.imprint","INTERSECT",VERTEX,{"derivedFrom":[makeQuery(id+"F1.opExtrude","CAP_EDGE",EDGE,{"disambiguationData":[OSD([sQuery(id+"F0.wireOp",EDGE,"E2.top")])],"isStart":false}),subQ0]}),-1.0]])],"derivedFrom":subQ0})])],"isStart":false});}
            var Q125;
            {var subQ0=sQuery(id+"F3.wireOp",EDGE,"E4.24.0.1");Q125=makeQuery(id+"F4.opExtrude","CAP_EDGE",EDGE,{"disambiguationData":[OSD([subQ0]),TDD([makeQuery(id+"F3.imprint","IMPRINT",EDGE,{"disambiguationData":[TD([[makeQuery(id+"F3.imprint","INTERSECT",VERTEX,{"derivedFrom":[makeQuery(id+"F1.opExtrude","CAP_EDGE",EDGE,{"disambiguationData":[OSD([sQuery(id+"F0.wireOp",EDGE,"E2.top")])],"isStart":false}),subQ0]}),-1.0]])],"derivedFrom":subQ0})])],"isStart":false});}
            var Q126;
            {var subQ0=sQuery(id+"F3.wireOp",EDGE,"E4.25.0.0");Q126=makeQuery(id+"F4.opExtrude","CAP_EDGE",EDGE,{"disambiguationData":[OSD([subQ0]),TDD([makeQuery(id+"F3.imprint","IMPRINT",EDGE,{"disambiguationData":[TD([[makeQuery(id+"F3.imprint","INTERSECT",VERTEX,{"derivedFrom":[makeQuery(id+"F1.opExtrude","CAP_EDGE",EDGE,{"disambiguationData":[OSD([sQuery(id+"F0.wireOp",EDGE,"E2.top")])],"isStart":false}),subQ0]}),-1.0]])],"derivedFrom":subQ0})])],"isStart":false});}
            var Q127;
            {var subQ0=sQuery(id+"F3.wireOp",EDGE,"E4.25.0.1");Q127=makeQuery(id+"F4.opExtrude","CAP_EDGE",EDGE,{"disambiguationData":[OSD([subQ0]),TDD([makeQuery(id+"F3.imprint","IMPRINT",EDGE,{"disambiguationData":[TD([[makeQuery(id+"F3.imprint","INTERSECT",VERTEX,{"derivedFrom":[makeQuery(id+"F1.opExtrude","CAP_EDGE",EDGE,{"disambiguationData":[OSD([sQuery(id+"F0.wireOp",EDGE,"E2.top")])],"isStart":false}),subQ0]}),-1.0]])],"derivedFrom":subQ0})])],"isStart":false});}
            var Q128;
            {var subQ0=sQuery(id+"F3.wireOp",EDGE,"E4.26.0.0");Q128=makeQuery(id+"F4.opExtrude","CAP_EDGE",EDGE,{"disambiguationData":[OSD([subQ0]),TDD([makeQuery(id+"F3.imprint","IMPRINT",EDGE,{"disambiguationData":[TD([[makeQuery(id+"F3.imprint","INTERSECT",VERTEX,{"derivedFrom":[makeQuery(id+"F1.opExtrude","CAP_EDGE",EDGE,{"disambiguationData":[OSD([sQuery(id+"F0.wireOp",EDGE,"E2.top")])],"isStart":false}),subQ0]}),-1.0]])],"derivedFrom":subQ0})])],"isStart":false});}
            var Q129;
            {var subQ0=sQuery(id+"F3.wireOp",EDGE,"E4.26.0.1");Q129=makeQuery(id+"F4.opExtrude","CAP_EDGE",EDGE,{"disambiguationData":[OSD([subQ0]),TDD([makeQuery(id+"F3.imprint","IMPRINT",EDGE,{"disambiguationData":[TD([[makeQuery(id+"F3.imprint","INTERSECT",VERTEX,{"derivedFrom":[makeQuery(id+"F1.opExtrude","CAP_EDGE",EDGE,{"disambiguationData":[OSD([sQuery(id+"F0.wireOp",EDGE,"E2.top")])],"isStart":false}),subQ0]}),-1.0]])],"derivedFrom":subQ0})])],"isStart":false});}
            var Q130;
            {var subQ0=sQuery(id+"F3.wireOp",EDGE,"E4.27.0.0");Q130=makeQuery(id+"F4.opExtrude","CAP_EDGE",EDGE,{"disambiguationData":[OSD([subQ0]),TDD([makeQuery(id+"F3.imprint","IMPRINT",EDGE,{"disambiguationData":[TD([[makeQuery(id+"F3.imprint","INTERSECT",VERTEX,{"derivedFrom":[makeQuery(id+"F1.opExtrude","CAP_EDGE",EDGE,{"disambiguationData":[OSD([sQuery(id+"F0.wireOp",EDGE,"E2.top")])],"isStart":false}),subQ0]}),-1.0]])],"derivedFrom":subQ0})])],"isStart":false});}
            var Q131;
            {var subQ0=sQuery(id+"F3.wireOp",EDGE,"E4.27.0.1");Q131=makeQuery(id+"F4.opExtrude","CAP_EDGE",EDGE,{"disambiguationData":[OSD([subQ0]),TDD([makeQuery(id+"F3.imprint","IMPRINT",EDGE,{"disambiguationData":[TD([[makeQuery(id+"F3.imprint","INTERSECT",VERTEX,{"derivedFrom":[makeQuery(id+"F1.opExtrude","CAP_EDGE",EDGE,{"disambiguationData":[OSD([sQuery(id+"F0.wireOp",EDGE,"E2.top")])],"isStart":false}),subQ0]}),-1.0]])],"derivedFrom":subQ0})])],"isStart":false});}
            var Q132;
            {var subQ0=sQuery(id+"F3.wireOp",EDGE,"E4.28.0.0");Q132=makeQuery(id+"F4.opExtrude","CAP_EDGE",EDGE,{"disambiguationData":[OSD([subQ0]),TDD([makeQuery(id+"F3.imprint","IMPRINT",EDGE,{"disambiguationData":[TD([[makeQuery(id+"F3.imprint","INTERSECT",VERTEX,{"derivedFrom":[makeQuery(id+"F1.opExtrude","CAP_EDGE",EDGE,{"disambiguationData":[OSD([sQuery(id+"F0.wireOp",EDGE,"E2.top")])],"isStart":false}),subQ0]}),-1.0]])],"derivedFrom":subQ0})])],"isStart":false});}
            var Q133;
            {var subQ0=sQuery(id+"F3.wireOp",EDGE,"E4.28.0.1");Q133=makeQuery(id+"F4.opExtrude","CAP_EDGE",EDGE,{"disambiguationData":[OSD([subQ0]),TDD([makeQuery(id+"F3.imprint","IMPRINT",EDGE,{"disambiguationData":[TD([[makeQuery(id+"F3.imprint","INTERSECT",VERTEX,{"derivedFrom":[makeQuery(id+"F1.opExtrude","CAP_EDGE",EDGE,{"disambiguationData":[OSD([sQuery(id+"F0.wireOp",EDGE,"E2.top")])],"isStart":false}),subQ0]}),-1.0]])],"derivedFrom":subQ0})])],"isStart":false});}
            var Q134;
            {var subQ0=sQuery(id+"F3.wireOp",EDGE,"E4.29.0.0");Q134=makeQuery(id+"F4.opExtrude","CAP_EDGE",EDGE,{"disambiguationData":[OSD([subQ0]),TDD([makeQuery(id+"F3.imprint","IMPRINT",EDGE,{"disambiguationData":[TD([[makeQuery(id+"F3.imprint","INTERSECT",VERTEX,{"derivedFrom":[makeQuery(id+"F1.opExtrude","CAP_EDGE",EDGE,{"disambiguationData":[OSD([sQuery(id+"F0.wireOp",EDGE,"E2.top")])],"isStart":false}),subQ0]}),-1.0]])],"derivedFrom":subQ0})])],"isStart":false});}
            var Q135;
            {var subQ0=sQuery(id+"F3.wireOp",EDGE,"E4.29.0.1");Q135=makeQuery(id+"F4.opExtrude","CAP_EDGE",EDGE,{"disambiguationData":[OSD([subQ0]),TDD([makeQuery(id+"F3.imprint","IMPRINT",EDGE,{"disambiguationData":[TD([[makeQuery(id+"F3.imprint","INTERSECT",VERTEX,{"derivedFrom":[makeQuery(id+"F1.opExtrude","CAP_EDGE",EDGE,{"disambiguationData":[OSD([sQuery(id+"F0.wireOp",EDGE,"E2.top")])],"isStart":false}),subQ0]}),-1.0]])],"derivedFrom":subQ0})])],"isStart":false});}
            var Q136;
            {var subQ0=sQuery(id+"F3.wireOp",EDGE,"E4.30.0.0");Q136=makeQuery(id+"F4.opExtrude","CAP_EDGE",EDGE,{"disambiguationData":[OSD([subQ0]),TDD([makeQuery(id+"F3.imprint","IMPRINT",EDGE,{"disambiguationData":[TD([[makeQuery(id+"F3.imprint","INTERSECT",VERTEX,{"derivedFrom":[makeQuery(id+"F1.opExtrude","CAP_EDGE",EDGE,{"disambiguationData":[OSD([sQuery(id+"F0.wireOp",EDGE,"E2.top")])],"isStart":false}),subQ0]}),-1.0]])],"derivedFrom":subQ0})])],"isStart":false});}
            var Q137;
            {var subQ0=sQuery(id+"F3.wireOp",EDGE,"E4.30.0.1");Q137=makeQuery(id+"F4.opExtrude","CAP_EDGE",EDGE,{"disambiguationData":[OSD([subQ0]),TDD([makeQuery(id+"F3.imprint","IMPRINT",EDGE,{"disambiguationData":[TD([[makeQuery(id+"F3.imprint","INTERSECT",VERTEX,{"derivedFrom":[makeQuery(id+"F1.opExtrude","CAP_EDGE",EDGE,{"disambiguationData":[OSD([sQuery(id+"F0.wireOp",EDGE,"E2.top")])],"isStart":false}),subQ0]}),-1.0]])],"derivedFrom":subQ0})])],"isStart":false});}
            var Q138;
            {var subQ0=sQuery(id+"F3.wireOp",EDGE,"E4.31.0.0");Q138=makeQuery(id+"F4.opExtrude","CAP_EDGE",EDGE,{"disambiguationData":[OSD([subQ0]),TDD([makeQuery(id+"F3.imprint","IMPRINT",EDGE,{"disambiguationData":[TD([[makeQuery(id+"F3.imprint","INTERSECT",VERTEX,{"derivedFrom":[makeQuery(id+"F1.opExtrude","CAP_EDGE",EDGE,{"disambiguationData":[OSD([sQuery(id+"F0.wireOp",EDGE,"E2.top")])],"isStart":false}),subQ0]}),-1.0]])],"derivedFrom":subQ0})])],"isStart":false});}
            var Q139;
            {var subQ0=sQuery(id+"F3.wireOp",EDGE,"E4.31.0.1");Q139=makeQuery(id+"F4.opExtrude","CAP_EDGE",EDGE,{"disambiguationData":[OSD([subQ0]),TDD([makeQuery(id+"F3.imprint","IMPRINT",EDGE,{"disambiguationData":[TD([[makeQuery(id+"F3.imprint","INTERSECT",VERTEX,{"derivedFrom":[makeQuery(id+"F1.opExtrude","CAP_EDGE",EDGE,{"disambiguationData":[OSD([sQuery(id+"F0.wireOp",EDGE,"E2.top")])],"isStart":false}),subQ0]}),-1.0]])],"derivedFrom":subQ0})])],"isStart":false});}
            var Q140;
            {var subQ0=sQuery(id+"F3.wireOp",EDGE,"E4.32.0.0");Q140=makeQuery(id+"F4.opExtrude","CAP_EDGE",EDGE,{"disambiguationData":[OSD([subQ0]),TDD([makeQuery(id+"F3.imprint","IMPRINT",EDGE,{"disambiguationData":[TD([[makeQuery(id+"F3.imprint","INTERSECT",VERTEX,{"derivedFrom":[makeQuery(id+"F1.opExtrude","CAP_EDGE",EDGE,{"disambiguationData":[OSD([sQuery(id+"F0.wireOp",EDGE,"E2.top")])],"isStart":false}),subQ0]}),-1.0]])],"derivedFrom":subQ0})])],"isStart":false});}
            var Q141;
            {var subQ0=sQuery(id+"F3.wireOp",EDGE,"E4.32.0.1");Q141=makeQuery(id+"F4.opExtrude","CAP_EDGE",EDGE,{"disambiguationData":[OSD([subQ0]),TDD([makeQuery(id+"F3.imprint","IMPRINT",EDGE,{"disambiguationData":[TD([[makeQuery(id+"F3.imprint","INTERSECT",VERTEX,{"derivedFrom":[makeQuery(id+"F1.opExtrude","CAP_EDGE",EDGE,{"disambiguationData":[OSD([sQuery(id+"F0.wireOp",EDGE,"E2.top")])],"isStart":false}),subQ0]}),-1.0]])],"derivedFrom":subQ0})])],"isStart":false});}
            var Q142;
            {var subQ0=sQuery(id+"F3.wireOp",EDGE,"E4.33.0.0");Q142=makeQuery(id+"F4.opExtrude","CAP_EDGE",EDGE,{"disambiguationData":[OSD([subQ0]),TDD([makeQuery(id+"F3.imprint","IMPRINT",EDGE,{"disambiguationData":[TD([[makeQuery(id+"F3.imprint","INTERSECT",VERTEX,{"derivedFrom":[makeQuery(id+"F1.opExtrude","CAP_EDGE",EDGE,{"disambiguationData":[OSD([sQuery(id+"F0.wireOp",EDGE,"E2.top")])],"isStart":false}),subQ0]}),-1.0]])],"derivedFrom":subQ0})])],"isStart":false});}
            var Q143;
            {var subQ0=sQuery(id+"F3.wireOp",EDGE,"E4.33.0.1");Q143=makeQuery(id+"F4.opExtrude","CAP_EDGE",EDGE,{"disambiguationData":[OSD([subQ0]),TDD([makeQuery(id+"F3.imprint","IMPRINT",EDGE,{"disambiguationData":[TD([[makeQuery(id+"F3.imprint","INTERSECT",VERTEX,{"derivedFrom":[makeQuery(id+"F1.opExtrude","CAP_EDGE",EDGE,{"disambiguationData":[OSD([sQuery(id+"F0.wireOp",EDGE,"E2.top")])],"isStart":false}),subQ0]}),-1.0]])],"derivedFrom":subQ0})])],"isStart":false});}
            var Q144;
            {var subQ0=sQuery(id+"F3.wireOp",EDGE,"E4.34.0.0");Q144=makeQuery(id+"F4.opExtrude","CAP_EDGE",EDGE,{"disambiguationData":[OSD([subQ0]),TDD([makeQuery(id+"F3.imprint","IMPRINT",EDGE,{"disambiguationData":[TD([[makeQuery(id+"F3.imprint","INTERSECT",VERTEX,{"derivedFrom":[makeQuery(id+"F1.opExtrude","CAP_EDGE",EDGE,{"disambiguationData":[OSD([sQuery(id+"F0.wireOp",EDGE,"E2.top")])],"isStart":false}),subQ0]}),-1.0]])],"derivedFrom":subQ0})])],"isStart":false});}
            var Q145;
            {var subQ0=sQuery(id+"F3.wireOp",EDGE,"E4.34.0.1");Q145=makeQuery(id+"F4.opExtrude","CAP_EDGE",EDGE,{"disambiguationData":[OSD([subQ0]),TDD([makeQuery(id+"F3.imprint","IMPRINT",EDGE,{"disambiguationData":[TD([[makeQuery(id+"F3.imprint","INTERSECT",VERTEX,{"derivedFrom":[makeQuery(id+"F1.opExtrude","CAP_EDGE",EDGE,{"disambiguationData":[OSD([sQuery(id+"F0.wireOp",EDGE,"E2.top")])],"isStart":false}),subQ0]}),-1.0]])],"derivedFrom":subQ0})])],"isStart":false});}
            var Q146;
            {var subQ0=sQuery(id+"F3.wireOp",EDGE,"E4.35.0.0");Q146=makeQuery(id+"F4.opExtrude","CAP_EDGE",EDGE,{"disambiguationData":[OSD([subQ0]),TDD([makeQuery(id+"F3.imprint","IMPRINT",EDGE,{"disambiguationData":[TD([[makeQuery(id+"F3.imprint","INTERSECT",VERTEX,{"derivedFrom":[makeQuery(id+"F1.opExtrude","CAP_EDGE",EDGE,{"disambiguationData":[OSD([sQuery(id+"F0.wireOp",EDGE,"E2.top")])],"isStart":false}),subQ0]}),-1.0]])],"derivedFrom":subQ0})])],"isStart":false});}
            var Q147;
            {var subQ0=sQuery(id+"F3.wireOp",EDGE,"E4.35.0.1");Q147=makeQuery(id+"F4.opExtrude","CAP_EDGE",EDGE,{"disambiguationData":[OSD([subQ0]),TDD([makeQuery(id+"F3.imprint","IMPRINT",EDGE,{"disambiguationData":[TD([[makeQuery(id+"F3.imprint","INTERSECT",VERTEX,{"derivedFrom":[makeQuery(id+"F1.opExtrude","CAP_EDGE",EDGE,{"disambiguationData":[OSD([sQuery(id+"F0.wireOp",EDGE,"E2.top")])],"isStart":false}),subQ0]}),-1.0]])],"derivedFrom":subQ0})])],"isStart":false});}
            var Q148;
            {var subQ0=sQuery(id+"F3.wireOp",EDGE,"E4.36.0.0");Q148=makeQuery(id+"F4.opExtrude","CAP_EDGE",EDGE,{"disambiguationData":[OSD([subQ0]),TDD([makeQuery(id+"F3.imprint","IMPRINT",EDGE,{"disambiguationData":[TD([[makeQuery(id+"F3.imprint","INTERSECT",VERTEX,{"derivedFrom":[makeQuery(id+"F1.opExtrude","CAP_EDGE",EDGE,{"disambiguationData":[OSD([sQuery(id+"F0.wireOp",EDGE,"E2.top")])],"isStart":false}),subQ0]}),-1.0]])],"derivedFrom":subQ0})])],"isStart":false});}
            var Q149;
            {var subQ0=sQuery(id+"F3.wireOp",EDGE,"E4.36.0.1");Q149=makeQuery(id+"F4.opExtrude","CAP_EDGE",EDGE,{"disambiguationData":[OSD([subQ0]),TDD([makeQuery(id+"F3.imprint","IMPRINT",EDGE,{"disambiguationData":[TD([[makeQuery(id+"F3.imprint","INTERSECT",VERTEX,{"derivedFrom":[makeQuery(id+"F1.opExtrude","CAP_EDGE",EDGE,{"disambiguationData":[OSD([sQuery(id+"F0.wireOp",EDGE,"E2.top")])],"isStart":false}),subQ0]}),-1.0]])],"derivedFrom":subQ0})])],"isStart":false});}
            var Q150;
            {var subQ0=sQuery(id+"F3.wireOp",EDGE,"E4.37.0.0");Q150=makeQuery(id+"F4.opExtrude","CAP_EDGE",EDGE,{"disambiguationData":[OSD([subQ0]),TDD([makeQuery(id+"F3.imprint","IMPRINT",EDGE,{"disambiguationData":[TD([[makeQuery(id+"F3.imprint","INTERSECT",VERTEX,{"derivedFrom":[makeQuery(id+"F1.opExtrude","CAP_EDGE",EDGE,{"disambiguationData":[OSD([sQuery(id+"F0.wireOp",EDGE,"E2.top")])],"isStart":false}),subQ0]}),-1.0]])],"derivedFrom":subQ0})])],"isStart":false});}
            var Q151;
            {var subQ0=sQuery(id+"F3.wireOp",EDGE,"E4.37.0.1");var subQ1=sQuery(id+"F0.wireOp",EDGE,"E2.top");Q151=makeQuery(id+"F4.opExtrude","CAP_EDGE",EDGE,{"disambiguationData":[OSD([subQ0]),TDD([makeQuery(id+"F3.imprint","IMPRINT",EDGE,{"disambiguationData":[TD([[makeQuery(id+"F3.imprint","INTERSECT",VERTEX,{"derivedFrom":[makeQuery(id+"F1.opExtrude","CAP_EDGE",EDGE,{"disambiguationData":[OSD([subQ1])],"isStart":false}),subQ0]}),-1.0]])],"derivedFrom":subQ0})])],"isStart":false});}
            var Q152;
            Q152=makeQuery(id+"F4.opExtrude","CAP_EDGE",EDGE,{"disambiguationData":[OSD([sQuery(id+"F3.wireOp",EDGE,"E4.38.0.0")])],"isStart":false});
            var Q153;
            Q153=makeQuery(id+"F4.opExtrude","CAP_EDGE",EDGE,{"disambiguationData":[OSD([sQuery(id+"F3.wireOp",EDGE,"E4.38.0.1")])],"isStart":false});
            var Q154;
            Q154=makeQuery(id+"F4.opExtrude","CAP_EDGE",EDGE,{"disambiguationData":[OSD([sQuery(id+"F3.wireOp",EDGE,"E4.39.0.0")])],"isStart":false});
            var Q155;
            Q155=makeQuery(id+"F4.opExtrude","CAP_EDGE",EDGE,{"disambiguationData":[OSD([sQuery(id+"F3.wireOp",EDGE,"E4.40.0.1")])],"isStart":false});
            var Q156;
            Q156=makeQuery(id+"F4.opExtrude","CAP_EDGE",EDGE,{"disambiguationData":[OSD([sQuery(id+"F3.wireOp",EDGE,"E4.40.0.0")])],"isStart":false});
            var Q157;
            Q157=makeQuery(id+"F4.opExtrude","CAP_EDGE",EDGE,{"disambiguationData":[OSD([sQuery(id+"F3.wireOp",EDGE,"E4.41.0.0")])],"isStart":false});
            var Q158;
            Q158=makeQuery(id+"F4.opExtrude","CAP_EDGE",EDGE,{"disambiguationData":[OSD([sQuery(id+"F3.wireOp",EDGE,"E4.41.0.1")])],"isStart":false});
            var Q159;
            Q159=makeQuery(id+"F4.opExtrude","CAP_EDGE",EDGE,{"disambiguationData":[OSD([sQuery(id+"F3.wireOp",EDGE,"E4.42.0.0")])],"isStart":false});
            var Q160;
            Q160=makeQuery(id+"F4.opExtrude","CAP_EDGE",EDGE,{"disambiguationData":[OSD([sQuery(id+"F3.wireOp",EDGE,"E4.42.0.1")])],"isStart":false});
            var Q161;
            Q161=makeQuery(id+"F4.opExtrude","CAP_EDGE",EDGE,{"disambiguationData":[OSD([sQuery(id+"F3.wireOp",EDGE,"E4.43.0.0")])],"isStart":false});
            var Q162;
            Q162=makeQuery(id+"F4.opExtrude","CAP_EDGE",EDGE,{"disambiguationData":[OSD([sQuery(id+"F3.wireOp",EDGE,"E4.43.0.1")])],"isStart":false});
            var Q163;
            Q163=makeQuery(id+"F4.opExtrude","CAP_EDGE",EDGE,{"disambiguationData":[OSD([sQuery(id+"F3.wireOp",EDGE,"E4.44.0.0")])],"isStart":false});
            var Q164;
            Q164=makeQuery(id+"F4.opExtrude","CAP_EDGE",EDGE,{"disambiguationData":[OSD([sQuery(id+"F3.wireOp",EDGE,"E4.44.0.1")])],"isStart":false});
            var Q165;
            Q165=makeQuery(id+"F4.opExtrude","CAP_EDGE",EDGE,{"disambiguationData":[OSD([sQuery(id+"F3.wireOp",EDGE,"E4.45.0.0")])],"isStart":false});
            var Q166;
            Q166=makeQuery(id+"F4.opExtrude","CAP_EDGE",EDGE,{"disambiguationData":[OSD([sQuery(id+"F3.wireOp",EDGE,"E4.45.0.1")])],"isStart":false});
            var Q167;
            Q167=makeQuery(id+"F4.opExtrude","CAP_EDGE",EDGE,{"disambiguationData":[OSD([sQuery(id+"F3.wireOp",EDGE,"E4.46.0.0")])],"isStart":false});
            var Q168;
            Q168=makeQuery(id+"F4.opExtrude","CAP_EDGE",EDGE,{"disambiguationData":[OSD([sQuery(id+"F3.wireOp",EDGE,"E4.46.0.1")])],"isStart":false});
            var Q169;
            Q169=makeQuery(id+"F4.opExtrude","CAP_EDGE",EDGE,{"disambiguationData":[OSD([sQuery(id+"F3.wireOp",EDGE,"E4.47.0.0")])],"isStart":false});
            var Q170;
            Q170=makeQuery(id+"F4.opExtrude","CAP_EDGE",EDGE,{"disambiguationData":[OSD([sQuery(id+"F3.wireOp",EDGE,"E4.47.0.1")])],"isStart":false});
            var Q171;
            Q171=makeQuery(id+"F4.opExtrude","CAP_EDGE",EDGE,{"disambiguationData":[OSD([sQuery(id+"F3.wireOp",EDGE,"E4.48.0.0")])],"isStart":false});
            var Q172;
            Q172=makeQuery(id+"F4.opExtrude","CAP_EDGE",EDGE,{"disambiguationData":[OSD([sQuery(id+"F3.wireOp",EDGE,"E4.48.0.1")])],"isStart":false});
            var Q173;
            Q173=makeQuery(id+"F4.opExtrude","CAP_EDGE",EDGE,{"disambiguationData":[OSD([sQuery(id+"F3.wireOp",EDGE,"E4.49.0.0")])],"isStart":false});
            var Q174;
            Q174=makeQuery(id+"F4.opExtrude","CAP_EDGE",EDGE,{"disambiguationData":[OSD([sQuery(id+"F3.wireOp",EDGE,"E4.49.0.1")])],"isStart":false});
            var Q175;
            Q175=makeQuery(id+"F4.opExtrude","CAP_EDGE",EDGE,{"disambiguationData":[OSD([sQuery(id+"F3.wireOp",EDGE,"E4.39.0.1")])],"isStart":false});
            chamfer(context, id + "F6", {"entities" : qUnion([Q0, Q1, Q2, Q3, Q4, Q5, Q6, Q7, Q8, Q9, Q10, Q11, Q12, Q13, Q14, Q15, Q16, Q17, Q18, Q19, Q20, Q21, Q22, Q23, Q24, Q25, Q26, Q27, Q28, Q29, Q30, Q31, Q32, Q33, Q34, Q35, Q36, Q37, Q38, Q39, Q40, Q41, Q42, Q43, Q44, Q45, Q46, Q47, Q48, Q49, Q50, Q51, Q52, Q53, Q54, Q55, Q56, Q57, Q58, Q59, Q60, Q61, Q62, Q63, Q64, Q65, Q66, Q67, Q68, Q69, Q70, Q71, Q72, Q73, Q74, Q75, Q76, Q77, Q78, Q79, Q80, Q81, Q82, Q83, Q84, Q85, Q86, Q87, Q88, Q89, Q90, Q91, Q92, Q93, Q94, Q95, Q96, Q97, Q98, Q99, Q100, Q101, Q102, Q103, Q104, Q105, Q106, Q107, Q108, Q109, Q110, Q111, Q112, Q113, Q114, Q115, Q116, Q117, Q118, Q119, Q120, Q121, Q122, Q123, Q124, Q125, Q126, Q127, Q128, Q129, Q130, Q131, Q132, Q133, Q134, Q135, Q136, Q137, Q138, Q139, Q140, Q141, Q142, Q143, Q144, Q145, Q146, Q147, Q148, Q149, Q150, Q151, Q152, Q153, Q154, Q155, Q156, Q157, Q158, Q159, Q160, Q161, Q162, Q163, Q164, Q165, Q166, Q167, Q168, Q169, Q170, Q171, Q172, Q173, Q174, Q175]), "width" : 0.6 * mm, "tangentPropagation" : true});
        }
    });
